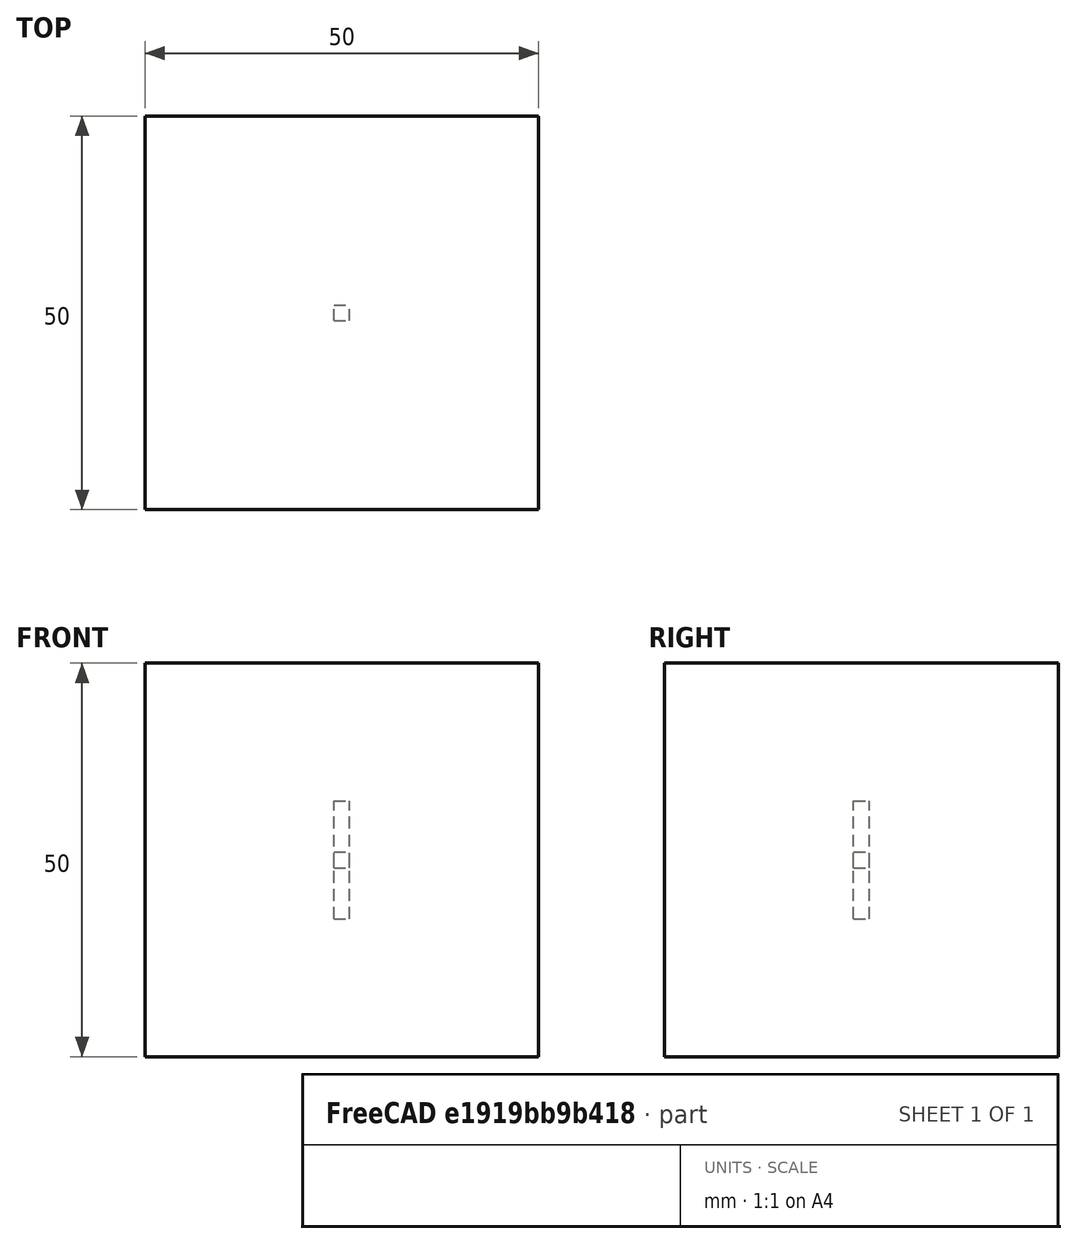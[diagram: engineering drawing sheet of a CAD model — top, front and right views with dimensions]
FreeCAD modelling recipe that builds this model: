
FCSTD DOCUMENT  (FreeCAD 0.20R29177 (Git))
Label: simple_array_expanded
License: All rights reserved
LicenseURL: http://en.wikipedia.org/wiki/All_rights_reserved
objects: App::DocumentObjectGroupPython×1269, App::Part×10, App::Link×6, App::FeaturePython×4, Part::FeaturePython×3
note: 3 computed .brp shape members not serialized (recipe doc carries the construction recipe); baked Part::Feature solids carry a one-line shape summary decoded from their .brp

FEATURE [App::DocumentObjectGroupPython] Constants  # scripted group (container) (typed FeaturePython)
FEATURE [App::DocumentObjectGroupPython] Variables  # scripted group (container) (typed FeaturePython)
FEATURE [App::DocumentObjectGroupPython] Quantities  # scripted group (container) (typed FeaturePython)
FEATURE [App::DocumentObjectGroupPython] Isotopes  # scripted group (container) (typed FeaturePython)
FEATURE [App::DocumentObjectGroupPython] Elements  # scripted group (container) (typed FeaturePython)
FEATURE [App::DocumentObjectGroupPython] G4_CESIUM_IODIDE  label="G4_CESIUM_IODIDE : 1.000"  # scripted group (container) (typed FeaturePython)
  n = 1
FEATURE [App::DocumentObjectGroupPython] LYSO  # scripted group (container) (typed FeaturePython)
  ABSLENGTH = ABSLENGTHLAR
  Dunit = g/cm3
  Dvalue = 7.1
  FASTCOMPONENT = SCINTLAR
  Group = -> [G4_CESIUM_IODIDE]
  RAYLEIGH = RAYLEIGHLAR
  REEMISSIONPROB = SCINTLAR
  RESOLUTIONSCALE = RS
  RINDEX = RINDEXLAR
  SCINTILLATIONCOMPONENT1 = SCINTLAR
  SCINTILLATIONCOMPONENT2 = SCINTLAR
  SCINTILLATIONTIMECONSTANT1 = FTC
  SCINTILLATIONTIMECONSTANT2 = STC
  SCINTILLATIONYIELD = SY
  SCINTILLATIONYIELD1 = RY1
  SCINTILLATIONYIELD2 = RY2
  SLOWCOMPONENT = SCINTLAR
  YIELDRATIO = YR
  conduct = 2
  density = 1
  expand = 3
  name = LYSO
  specific = 4
FEATURE [App::DocumentObjectGroupPython] G4_AIR  label="G4_AIR : 1.000"  # scripted group (container) (typed FeaturePython)
  n = 1
FEATURE [App::DocumentObjectGroupPython] Air  # scripted group (container) (typed FeaturePython)
  Dunit = mg/cm3
  Dvalue = 1.29
  Group = -> [G4_AIR]
  RINDEX = AirRINDEX
  conduct = 2
  density = 1
  expand = 3
  name = Air
  specific = 4
FEATURE [App::DocumentObjectGroupPython] G4_SILICON_DIOXIDE  label="G4_SILICON_DIOXIDE : 1.000"  # scripted group (container) (typed FeaturePython)
  n = 1
FEATURE [App::DocumentObjectGroupPython] Glass  # scripted group (container) (typed FeaturePython)
  Dunit = g/cm3
  Dvalue = 2.32
  Group = -> [G4_SILICON_DIOXIDE]
  RINDEX = RINDEXLAR
  conduct = 2
  density = 1
  expand = 3
  name = Glass
  specific = 4
FEATURE [App::DocumentObjectGroupPython] SY  # scripted group (container) (typed FeaturePython)
  coldim = 1
  values = 100000
FEATURE [App::DocumentObjectGroupPython] RS  # scripted group (container) (typed FeaturePython)
  coldim = 1
  values = 1
FEATURE [App::DocumentObjectGroupPython] FTC  # scripted group (container) (typed FeaturePython)
  coldim = 1
  values = 21.5*ns
FEATURE [App::DocumentObjectGroupPython] STC  # scripted group (container) (typed FeaturePython)
  coldim = 1
  values = 43.8*ns
FEATURE [App::DocumentObjectGroupPython] RY1  # scripted group (container) (typed FeaturePython)
  coldim = 1
  values = 95
FEATURE [App::DocumentObjectGroupPython] RY2  # scripted group (container) (typed FeaturePython)
  coldim = 1
  values = 5
FEATURE [App::DocumentObjectGroupPython] YR  # scripted group (container) (typed FeaturePython)
  coldim = 1
  values = 0.8
FEATURE [App::DocumentObjectGroupPython] SCINTLAR  # scripted group (container) (typed FeaturePython)
  coldim = 2
  values = <blob: 2358 chars omitted>
FEATURE [App::DocumentObjectGroupPython] RINDEXLAR  # scripted group (container) (typed FeaturePython)
  coldim = 2
  values = <blob: 9384 chars omitted>
FEATURE [App::DocumentObjectGroupPython] ABSLENGTHLAR  # scripted group (container) (typed FeaturePython)
  coldim = 2
  values = 7.74901*eV 10.0*m 7.77525*eV 10.0*m 7.80167*eV 10.0*m 7.82827*eV 10.0*m 7.85506*eV 10.0*m 7.88202*eV 10.0*m 7.90917*eV 10.0*m 7.93651*eV 10.0*m 7.96404*eV 10.0*m 7.99176*eV 10.0*m 8.01968*eV 10.0*m 8.04779*eV 10.0*m 8.07609*eV 10.0*m 8.1046*eV 10.0*m 8.13331*eV 10.0*m 8.16222*eV 10.0*m 8.19134*eV 10.0*m 8.22067*eV 10.0*m 8.25021*eV 10.0*m 8.27996*eV 10.0*m 8.30993*eV 10.0*m 8.34012*eV 10.0*m 8.37052*eV 10.0*m 8.40115*eV 10.0*m 8.432*eV 10.0*m 8.46308*eV 10.0*m 8.4944*eV 10.0*m 8.52594*eV 10.0*m 8.55772*eV 10.0*m 8.58973*eV 10.0*m 8.62199*eV 10.0*m 8.65449*eV 10.0*m 8.68723*eV 10.0*m 8.72023*eV 10.0*m 8.75347*eV 10.0*m 8.78697*eV 10.0*m 8.82073*eV 10.0*m 8.85475*eV 10.0*m 8.88903*eV 10.0*m 8.92358*eV 10.0*m 8.9584*eV 10.0*m 8.99349*eV 10.0*m 9.02885*eV 10.0*m 9.0645*eV 10.0*m 9.10043*eV 10.0*m 9.13664*eV 10.0*m 9.17314*eV 10.0*m 9.20994*eV 10.0*m 9.24703*eV 10.0*m 9.28442*eV 10.0*m 9.32212*eV 10.0*m 9.36012*eV 10.0*m 9.39844*eV 10.0*m 9.43707*eV 10.0*m 9.47602*eV 10.0*m 9.51529*eV 10.0*m 9.55489*eV 10.0*m 9.59481*eV 10.0*m 9.63508*eV 10.0*m 9.67568*eV 10.0*m 9.71663*eV 10.0*m 9.75792*eV 10.0*m 9.79957*eV 10.0*m 9.84158*eV 10.0*m 9.88394*eV 10.0*m 9.92668*eV 10.0*m 9.96978*eV 10.0*m 10.0133*eV 10.0*m 10.0571*eV 10.0*m 10.1014*eV 10.0*m 10.146*eV 10.0*m 10.191*eV 10.0*m 10.2365*eV 10.0*m 10.2823*eV 10.0*m 10.3286*eV 10.0*m 10.3752*eV 10.0*m 10.4223*eV 10.0*m 10.4699*eV 10.0*m 10.5178*eV 10.0*m 10.5662*eV 10.0*m 10.6151*eV 10.0*m 10.6644*eV 10.0*m 10.7142*eV 10.0*m 10.7644*eV 10.0*m 10.8151*eV 10.0*m 10.8663*eV 10.0*m 10.9179*eV 10.0*m 10.9701*eV 10.0*m 11.0228*eV 10.0*m 11.076*eV 10.0*m 11.1296*eV 10.0*m 11.1839*eV 10.0*m 11.2386*eV 10.0*m 11.2939*eV 10.0*m 11.3497*eV 10.0*m 11.4061*eV 10.0*m 11.463*eV 10.0*m 11.5206*eV 10.0*m 11.5787*eV 10.0*m 11.6373*eV 10.0*m
FEATURE [App::DocumentObjectGroupPython] RAYLEIGHLAR  # scripted group (container) (typed FeaturePython)
  coldim = 2
  values = 7.74901*eV 90.0*cm 7.77525*eV 90.0*cm 7.80167*eV 90.0*cm 7.82827*eV 90.0*cm 7.85506*eV 90.0*cm 7.88202*eV 90.0*cm 7.90917*eV 90.0*cm 7.93651*eV 90.0*cm 7.96404*eV 90.0*cm 7.99176*eV 90.0*cm 8.01968*eV 90.0*cm 8.04779*eV 90.0*cm 8.07609*eV 90.0*cm 8.1046*eV 90.0*cm 8.13331*eV 90.0*cm 8.16222*eV 90.0*cm 8.19134*eV 90.0*cm 8.22067*eV 90.0*cm 8.25021*eV 90.0*cm 8.27996*eV 90.0*cm 8.30993*eV 90.0*cm 8.34012*eV 90.0*cm 8.37052*eV 90.0*cm 8.40115*eV 90.0*cm 8.432*eV 90.0*cm 8.46308*eV 90.0*cm 8.4944*eV 90.0*cm 8.52594*eV 90.0*cm 8.55772*eV 90.0*cm 8.58973*eV 90.0*cm 8.62199*eV 90.0*cm 8.65449*eV 90.0*cm 8.68723*eV 90.0*cm 8.72023*eV 90.0*cm 8.75347*eV 90.0*cm 8.78697*eV 90.0*cm 8.82073*eV 90.0*cm 8.85475*eV 90.0*cm 8.88903*eV 90.0*cm 8.92358*eV 90.0*cm 8.9584*eV 90.0*cm 8.99349*eV 90.0*cm 9.02885*eV 90.0*cm 9.0645*eV 90.0*cm 9.10043*eV 90.0*cm 9.13664*eV 90.0*cm 9.17314*eV 90.0*cm 9.20994*eV 90.0*cm 9.24703*eV 90.0*cm 9.28442*eV 90.0*cm 9.32212*eV 90.0*cm 9.36012*eV 90.0*cm 9.39844*eV 90.0*cm 9.43707*eV 90.0*cm 9.47602*eV 90.0*cm 9.51529*eV 90.0*cm 9.55489*eV 90.0*cm 9.59481*eV 90.0*cm 9.63508*eV 90.0*cm 9.67568*eV 90.0*cm 9.71663*eV 90.0*cm 9.75792*eV 90.0*cm 9.79957*eV 90.0*cm 9.84158*eV 90.0*cm 9.88394*eV 90.0*cm 9.92668*eV 90.0*cm 9.96978*eV 90.0*cm 10.0133*eV 90.0*cm 10.0571*eV 90.0*cm 10.1014*eV 90.0*cm 10.146*eV 90.0*cm 10.191*eV 90.0*cm 10.2365*eV 90.0*cm 10.2823*eV 90.0*cm 10.3286*eV 90.0*cm 10.3752*eV 90.0*cm 10.4223*eV 90.0*cm 10.4699*eV 90.0*cm 10.5178*eV 90.0*cm 10.5662*eV 90.0*cm 10.6151*eV 90.0*cm 10.6644*eV 90.0*cm 10.7142*eV 90.0*cm 10.7644*eV 90.0*cm 10.8151*eV 90.0*cm 10.8663*eV 90.0*cm 10.9179*eV 90.0*cm 10.9701*eV 90.0*cm 11.0228*eV 90.0*cm 11.076*eV 90.0*cm 11.1296*eV 90.0*cm 11.1839*eV 90.0*cm 11.2386*eV 90.0*cm 11.2939*eV 90.0*cm 11.3497*eV 90.0*cm 11.4061*eV 90.0*cm 11.463*eV 90.0*cm 11.5206*eV 90.0*cm 11.5787*eV 90.0*cm 11.6373*eV 90.0*cm
FEATURE [App::DocumentObjectGroupPython] REFLECTIVITY  # scripted group (container) (typed FeaturePython)
  coldim = 2
  values = 2.034*eV 0.98 2.068*eV 0.98 2.103*eV 0.98 2.139*eV 0.98 2.177*eV 0.98 2.216*eV 0.98 2.256*eV 0.98 2.298*eV 0.98 2.341*eV 0.98 2.386*eV 0.98 2.433*eV 0.98 2.481*eV 0.98 2.532*eV 0.98 2.585*eV 0.98 2.64*eV 0.98 2.697*eV 0.98 2.757*eV 0.98 2.82*eV 0.98 2.885*eV 0.98 2.954*eV 0.98 3.026*eV 0.98 3.102*eV 0.98 3.181*eV 0.98 3.265*eV 0.98 3.353*eV 0.98 3.446*eV 0.98 3.545*eV 0.98 3.649*eV 0.98 3.76*eV 0.98 3.877*eV 0.98 4.002*eV 0.98 4.136*eV 0.98 5.0*eV 0.98 6.0*eV 0.98 7.0*eV 0.98 8.0*eV 0.98 9.0*eV 0.98 9.0*eV 0.98 10.0*eV 0.98 11.0*eV 0.98 11.6*eV 0.98
FEATURE [App::DocumentObjectGroupPython] EFFICIENCY  # scripted group (container) (typed FeaturePython)
  coldim = 2
  values = 2.034*eV 1 2.068*eV 1 2.103*eV 1 2.139*eV 1 2.177*eV 1 2.216*eV 1 2.256*eV 1 2.298*eV 1 2.341*eV 1 2.386*eV 1 2.433*eV 1 2.481*eV 1 2.532*eV 1 2.585*eV 1 2.64*eV 1 2.697*eV 1 2.757*eV 1 2.82*eV 1 2.885*eV 1 2.954*eV 1 3.026*eV 1 3.102*eV 1 3.181*eV  1 3.265*eV 1 3.353*eV 1 3.446*eV 1 3.545*eV 1 3.649*eV 1 3.76*eV 1 3.877*eV 1 4.002*eV 1 4.136*eV 1 5.0*eV 1 6.0*eV 1 7.0*eV 1 8.0*eV 1 9.0*eV 1 9.0*eV 1 10.0*eV 1 11.0*eV 1 11.6*eV 1
FEATURE [App::DocumentObjectGroupPython] AirRINDEX  # scripted group (container) (typed FeaturePython)
  coldim = 2
  values = 2.034*eV 1 2.068*eV 1 2.103*eV 1 2.139*eV 1 2.177*eV 1 2.216*eV 1 2.256*eV 1 2.298*eV 1 2.341*eV 1 2.386*eV 1 2.433*eV 1 2.481*eV 1 2.532*eV 1 2.585*eV 1 2.64*eV 1 2.697*eV 1 2.757*eV 1 2.82*eV 1 2.885*eV 1 2.954*eV 1 3.026*eV 1 3.102*eV 1 3.181*eV 1 3.265*eV 1 3.353*eV 1 3.446*eV 1 3.545*eV 1 3.649*eV 1 3.76*eV 1 3.877*eV 1 4.002*eV 1 4.136*eV 1 5.0*eV 1 6.0*eV 1 7.0*eV 1 8.0*eV 1 9.0*eV 1 10.0*eV 1 11.0*eV 1 11.6*eV 1
FEATURE [App::DocumentObjectGroupPython] Matrix  # scripted group (container) (typed FeaturePython)
  Group = -> [SY,RS,FTC,STC,RY1,RY2,YR,SCINTLAR,RINDEXLAR,ABSLENGTHLAR,RAYLEIGHLAR,REFLECTIVITY,EFFICIENCY,AirRINDEX]
FEATURE [App::DocumentObjectGroupPython] ScintWrap  # scripted group (container) (typed FeaturePython)
  EFFICIENCY = EFFICIENCY
  REFLECTIVITY = REFLECTIVITY
  finish = 39
  model = 0
  type = 2
  value = 1
FEATURE [App::DocumentObjectGroupPython] Surfaces  # scripted group (container) (typed FeaturePython)
  Group = -> [ScintWrap]
FEATURE [App::DocumentObjectGroupPython] Opticals  # scripted group (container) (typed FeaturePython)
  Group = -> [Matrix,Surfaces]
FEATURE [App::DocumentObjectGroupPython] G4Isotopes  # scripted group (container) (typed FeaturePython)
FEATURE [App::DocumentObjectGroupPython] H_element  # scripted group (container) (typed FeaturePython)
  Z = 1
  atom_value = 1.008
  formula = H
  name = H_element
FEATURE [App::DocumentObjectGroupPython] He_element  # scripted group (container) (typed FeaturePython)
  Z = 2
  atom_value = 4.0026
  formula = He
  name = He_element
FEATURE [App::DocumentObjectGroupPython] Li_element  # scripted group (container) (typed FeaturePython)
  Z = 3
  atom_value = 6.94
  formula = Li
  name = Li_element
FEATURE [App::DocumentObjectGroupPython] Be_element  # scripted group (container) (typed FeaturePython)
  Z = 4
  atom_value = 9.01218
  formula = Be
  name = Be_element
FEATURE [App::DocumentObjectGroupPython] B_element  # scripted group (container) (typed FeaturePython)
  Z = 5
  atom_value = 10.81
  formula = B
  name = B_element
FEATURE [App::DocumentObjectGroupPython] C_element  # scripted group (container) (typed FeaturePython)
  Z = 6
  atom_value = 12.011
  formula = C
  name = C_element
FEATURE [App::DocumentObjectGroupPython] N_element  # scripted group (container) (typed FeaturePython)
  Z = 7
  atom_value = 14.007
  formula = N
  name = N_element
FEATURE [App::DocumentObjectGroupPython] O_element  # scripted group (container) (typed FeaturePython)
  Z = 8
  atom_value = 15.999
  formula = O
  name = O_element
FEATURE [App::DocumentObjectGroupPython] F_element  # scripted group (container) (typed FeaturePython)
  Z = 9
  atom_value = 18.9984
  formula = F
  name = F_element
FEATURE [App::DocumentObjectGroupPython] Ne_element  # scripted group (container) (typed FeaturePython)
  Z = 10
  atom_value = 20.1797
  formula = Ne
  name = Ne_element
FEATURE [App::DocumentObjectGroupPython] Na_element  # scripted group (container) (typed FeaturePython)
  Z = 11
  atom_value = 22.9898
  formula = Na
  name = Na_element
FEATURE [App::DocumentObjectGroupPython] Mg_element  # scripted group (container) (typed FeaturePython)
  Z = 12
  atom_value = 24.305
  formula = Mg
  name = Mg_element
FEATURE [App::DocumentObjectGroupPython] Al_element  # scripted group (container) (typed FeaturePython)
  Z = 13
  atom_value = 26.9815
  formula = Al
  name = Al_element
FEATURE [App::DocumentObjectGroupPython] Si_element  # scripted group (container) (typed FeaturePython)
  Z = 14
  atom_value = 28.085
  formula = Si
  name = Si_element
FEATURE [App::DocumentObjectGroupPython] P_element  # scripted group (container) (typed FeaturePython)
  Z = 15
  atom_value = 30.9738
  formula = P
  name = P_element
FEATURE [App::DocumentObjectGroupPython] S_element  # scripted group (container) (typed FeaturePython)
  Z = 16
  atom_value = 32.06
  formula = S
  name = S_element
FEATURE [App::DocumentObjectGroupPython] Cl_element  # scripted group (container) (typed FeaturePython)
  Z = 17
  atom_value = 35.45
  formula = Cl
  name = Cl_element
FEATURE [App::DocumentObjectGroupPython] Ar_element  # scripted group (container) (typed FeaturePython)
  Z = 18
  atom_value = 39.95
  formula = Ar
  name = Ar_element
FEATURE [App::DocumentObjectGroupPython] K_element  # scripted group (container) (typed FeaturePython)
  Z = 19
  atom_value = 39.0983
  formula = K
  name = K_element
FEATURE [App::DocumentObjectGroupPython] Ca_element  # scripted group (container) (typed FeaturePython)
  Z = 20
  atom_value = 40.078
  formula = Ca
  name = Ca_element
FEATURE [App::DocumentObjectGroupPython] Sc_element  # scripted group (container) (typed FeaturePython)
  Z = 21
  atom_value = 44.9559
  formula = Sc
  name = Sc_element
FEATURE [App::DocumentObjectGroupPython] Ti_element  # scripted group (container) (typed FeaturePython)
  Z = 22
  atom_value = 47.867
  formula = Ti
  name = Ti_element
FEATURE [App::DocumentObjectGroupPython] V_element  # scripted group (container) (typed FeaturePython)
  Z = 23
  atom_value = 50.9415
  formula = V
  name = V_element
FEATURE [App::DocumentObjectGroupPython] Cr_element  # scripted group (container) (typed FeaturePython)
  Z = 24
  atom_value = 51.9961
  formula = Cr
  name = Cr_element
FEATURE [App::DocumentObjectGroupPython] Mn_element  # scripted group (container) (typed FeaturePython)
  Z = 25
  atom_value = 54.938
  formula = Mn
  name = Mn_element
FEATURE [App::DocumentObjectGroupPython] Fe_element  # scripted group (container) (typed FeaturePython)
  Z = 26
  atom_value = 55.845
  formula = Fe
  name = Fe_element
FEATURE [App::DocumentObjectGroupPython] Co_element  # scripted group (container) (typed FeaturePython)
  Z = 27
  atom_value = 58.9332
  formula = Co
  name = Co_element
FEATURE [App::DocumentObjectGroupPython] Ni_element  # scripted group (container) (typed FeaturePython)
  Z = 28
  atom_value = 58.6934
  formula = Ni
  name = Ni_element
FEATURE [App::DocumentObjectGroupPython] Cu_element  # scripted group (container) (typed FeaturePython)
  Z = 29
  atom_value = 63.546
  formula = Cu
  name = Cu_element
FEATURE [App::DocumentObjectGroupPython] Zn_element  # scripted group (container) (typed FeaturePython)
  Z = 30
  atom_value = 65.38
  formula = Zn
  name = Zn_element
FEATURE [App::DocumentObjectGroupPython] Ga_element  # scripted group (container) (typed FeaturePython)
  Z = 31
  atom_value = 69.723
  formula = Ga
  name = Ga_element
FEATURE [App::DocumentObjectGroupPython] Ge_element  # scripted group (container) (typed FeaturePython)
  Z = 32
  atom_value = 72.63
  formula = Ge
  name = Ge_element
FEATURE [App::DocumentObjectGroupPython] As_element  # scripted group (container) (typed FeaturePython)
  Z = 33
  atom_value = 74.9216
  formula = As
  name = As_element
FEATURE [App::DocumentObjectGroupPython] Se_element  # scripted group (container) (typed FeaturePython)
  Z = 34
  atom_value = 78.971
  formula = Se
  name = Se_element
FEATURE [App::DocumentObjectGroupPython] Br_element  # scripted group (container) (typed FeaturePython)
  Z = 35
  atom_value = 79.904
  formula = Br
  name = Br_element
FEATURE [App::DocumentObjectGroupPython] Kr_element  # scripted group (container) (typed FeaturePython)
  Z = 36
  atom_value = 83.798
  formula = Kr
  name = Kr_element
FEATURE [App::DocumentObjectGroupPython] Rb_element  # scripted group (container) (typed FeaturePython)
  Z = 37
  atom_value = 85.4678
  formula = Rb
  name = Rb_element
FEATURE [App::DocumentObjectGroupPython] Sr_element  # scripted group (container) (typed FeaturePython)
  Z = 38
  atom_value = 87.62
  formula = Sr
  name = Sr_element
FEATURE [App::DocumentObjectGroupPython] Y_element  # scripted group (container) (typed FeaturePython)
  Z = 39
  atom_value = 88.9058
  formula = Y
  name = Y_element
FEATURE [App::DocumentObjectGroupPython] Zr_element  # scripted group (container) (typed FeaturePython)
  Z = 40
  atom_value = 91.224
  formula = Zr
  name = Zr_element
FEATURE [App::DocumentObjectGroupPython] Nb_element  # scripted group (container) (typed FeaturePython)
  Z = 41
  atom_value = 92.9064
  formula = Nb
  name = Nb_element
FEATURE [App::DocumentObjectGroupPython] Mo_element  # scripted group (container) (typed FeaturePython)
  Z = 42
  atom_value = 95.95
  formula = Mo
  name = Mo_element
FEATURE [App::DocumentObjectGroupPython] Tc_element  # scripted group (container) (typed FeaturePython)
  Z = 43
  atom_value = 97
  formula = Tc
  name = Tc_element
FEATURE [App::DocumentObjectGroupPython] Ru_element  # scripted group (container) (typed FeaturePython)
  Z = 44
  atom_value = 101.07
  formula = Ru
  name = Ru_element
FEATURE [App::DocumentObjectGroupPython] Rh_element  # scripted group (container) (typed FeaturePython)
  Z = 45
  atom_value = 102.905
  formula = Rh
  name = Rh_element
FEATURE [App::DocumentObjectGroupPython] Pd_element  # scripted group (container) (typed FeaturePython)
  Z = 46
  atom_value = 106.42
  formula = Pd
  name = Pd_element
FEATURE [App::DocumentObjectGroupPython] Ag_element  # scripted group (container) (typed FeaturePython)
  Z = 47
  atom_value = 107.868
  formula = Ag
  name = Ag_element
FEATURE [App::DocumentObjectGroupPython] Cd_element  # scripted group (container) (typed FeaturePython)
  Z = 48
  atom_value = 112.414
  formula = Cd
  name = Cd_element
FEATURE [App::DocumentObjectGroupPython] In_element  # scripted group (container) (typed FeaturePython)
  Z = 49
  atom_value = 114.818
  formula = In
  name = In_element
FEATURE [App::DocumentObjectGroupPython] Sn_element  # scripted group (container) (typed FeaturePython)
  Z = 50
  atom_value = 118.71
  formula = Sn
  name = Sn_element
FEATURE [App::DocumentObjectGroupPython] Sb_element  # scripted group (container) (typed FeaturePython)
  Z = 51
  atom_value = 121.76
  formula = Sb
  name = Sb_element
FEATURE [App::DocumentObjectGroupPython] Te_element  # scripted group (container) (typed FeaturePython)
  Z = 52
  atom_value = 127.6
  formula = Te
  name = Te_element
FEATURE [App::DocumentObjectGroupPython] I_element  # scripted group (container) (typed FeaturePython)
  Z = 53
  atom_value = 126.904
  formula = I
  name = I_element
FEATURE [App::DocumentObjectGroupPython] Xe_element  # scripted group (container) (typed FeaturePython)
  Z = 54
  atom_value = 131.293
  formula = Xe
  name = Xe_element
FEATURE [App::DocumentObjectGroupPython] Cs_element  # scripted group (container) (typed FeaturePython)
  Z = 55
  atom_value = 132.905
  formula = Cs
  name = Cs_element
FEATURE [App::DocumentObjectGroupPython] Ba_element  # scripted group (container) (typed FeaturePython)
  Z = 56
  atom_value = 137.327
  formula = Ba
  name = Ba_element
FEATURE [App::DocumentObjectGroupPython] La_element  # scripted group (container) (typed FeaturePython)
  Z = 57
  atom_value = 138.905
  formula = La
  name = La_element
FEATURE [App::DocumentObjectGroupPython] Ce_element  # scripted group (container) (typed FeaturePython)
  Z = 58
  atom_value = 140.116
  formula = Ce
  name = Ce_element
FEATURE [App::DocumentObjectGroupPython] Pr_element  # scripted group (container) (typed FeaturePython)
  Z = 59
  atom_value = 140.908
  formula = Pr
  name = Pr_element
FEATURE [App::DocumentObjectGroupPython] Nd_element  # scripted group (container) (typed FeaturePython)
  Z = 60
  atom_value = 144.242
  formula = Nd
  name = Nd_element
FEATURE [App::DocumentObjectGroupPython] Pm_element  # scripted group (container) (typed FeaturePython)
  Z = 61
  atom_value = 145
  formula = Pm
  name = Pm_element
FEATURE [App::DocumentObjectGroupPython] Sm_element  # scripted group (container) (typed FeaturePython)
  Z = 62
  atom_value = 150.36
  formula = Sm
  name = Sm_element
FEATURE [App::DocumentObjectGroupPython] Eu_element  # scripted group (container) (typed FeaturePython)
  Z = 63
  atom_value = 151.964
  formula = Eu
  name = Eu_element
FEATURE [App::DocumentObjectGroupPython] Gd_element  # scripted group (container) (typed FeaturePython)
  Z = 64
  atom_value = 157.25
  formula = Gd
  name = Gd_element
FEATURE [App::DocumentObjectGroupPython] Tb_element  # scripted group (container) (typed FeaturePython)
  Z = 65
  atom_value = 158.925
  formula = Tb
  name = Tb_element
FEATURE [App::DocumentObjectGroupPython] Dy_element  # scripted group (container) (typed FeaturePython)
  Z = 66
  atom_value = 162.5
  formula = Dy
  name = Dy_element
FEATURE [App::DocumentObjectGroupPython] Ho_element  # scripted group (container) (typed FeaturePython)
  Z = 67
  atom_value = 164.93
  formula = Ho
  name = Ho_element
FEATURE [App::DocumentObjectGroupPython] Er_element  # scripted group (container) (typed FeaturePython)
  Z = 68
  atom_value = 167.259
  formula = Er
  name = Er_element
FEATURE [App::DocumentObjectGroupPython] Tm_element  # scripted group (container) (typed FeaturePython)
  Z = 69
  atom_value = 168.934
  formula = Tm
  name = Tm_element
FEATURE [App::DocumentObjectGroupPython] Yb_element  # scripted group (container) (typed FeaturePython)
  Z = 70
  atom_value = 173.045
  formula = Yb
  name = Yb_element
FEATURE [App::DocumentObjectGroupPython] Lu_element  # scripted group (container) (typed FeaturePython)
  Z = 71
  atom_value = 174.967
  formula = Lu
  name = Lu_element
FEATURE [App::DocumentObjectGroupPython] Hf_element  # scripted group (container) (typed FeaturePython)
  Z = 72
  atom_value = 178.49
  formula = Hf
  name = Hf_element
FEATURE [App::DocumentObjectGroupPython] Ta_element  # scripted group (container) (typed FeaturePython)
  Z = 73
  atom_value = 180.948
  formula = Ta
  name = Ta_element
FEATURE [App::DocumentObjectGroupPython] W_element  # scripted group (container) (typed FeaturePython)
  Z = 74
  atom_value = 183.84
  formula = W
  name = W_element
FEATURE [App::DocumentObjectGroupPython] Re_element  # scripted group (container) (typed FeaturePython)
  Z = 75
  atom_value = 186.207
  formula = Re
  name = Re_element
FEATURE [App::DocumentObjectGroupPython] Os_element  # scripted group (container) (typed FeaturePython)
  Z = 76
  atom_value = 190.23
  formula = Os
  name = Os_element
FEATURE [App::DocumentObjectGroupPython] Ir_element  # scripted group (container) (typed FeaturePython)
  Z = 77
  atom_value = 192.217
  formula = Ir
  name = Ir_element
FEATURE [App::DocumentObjectGroupPython] Pt_element  # scripted group (container) (typed FeaturePython)
  Z = 78
  atom_value = 195.084
  formula = Pt
  name = Pt_element
FEATURE [App::DocumentObjectGroupPython] Au_element  # scripted group (container) (typed FeaturePython)
  Z = 79
  atom_value = 196.967
  formula = Au
  name = Au_element
FEATURE [App::DocumentObjectGroupPython] Hg_element  # scripted group (container) (typed FeaturePython)
  Z = 80
  atom_value = 200.592
  formula = Hg
  name = Hg_element
FEATURE [App::DocumentObjectGroupPython] Tl_element  # scripted group (container) (typed FeaturePython)
  Z = 81
  atom_value = 204.38
  formula = Tl
  name = Tl_element
FEATURE [App::DocumentObjectGroupPython] Pb_element  # scripted group (container) (typed FeaturePython)
  Z = 82
  atom_value = 207.2
  formula = Pb
  name = Pb_element
FEATURE [App::DocumentObjectGroupPython] Bi_element  # scripted group (container) (typed FeaturePython)
  Z = 83
  atom_value = 208.98
  formula = Bi
  name = Bi_element
FEATURE [App::DocumentObjectGroupPython] Po_element  # scripted group (container) (typed FeaturePython)
  Z = 84
  atom_value = 209
  formula = Po
  name = Po_element
FEATURE [App::DocumentObjectGroupPython] At_element  # scripted group (container) (typed FeaturePython)
  Z = 85
  atom_value = 210
  formula = At
  name = At_element
FEATURE [App::DocumentObjectGroupPython] Rn_element  # scripted group (container) (typed FeaturePython)
  Z = 86
  atom_value = 222
  formula = Rn
  name = Rn_element
FEATURE [App::DocumentObjectGroupPython] Fr_element  # scripted group (container) (typed FeaturePython)
  Z = 87
  atom_value = 223
  formula = Fr
  name = Fr_element
FEATURE [App::DocumentObjectGroupPython] Ra_element  # scripted group (container) (typed FeaturePython)
  Z = 88
  atom_value = 226
  formula = Ra
  name = Ra_element
FEATURE [App::DocumentObjectGroupPython] Ac_element  # scripted group (container) (typed FeaturePython)
  Z = 89
  atom_value = 227
  formula = Ac
  name = Ac_element
FEATURE [App::DocumentObjectGroupPython] Th_element  # scripted group (container) (typed FeaturePython)
  Z = 90
  atom_value = 232.038
  formula = Th
  name = Th_element
FEATURE [App::DocumentObjectGroupPython] Pa_element  # scripted group (container) (typed FeaturePython)
  Z = 91
  atom_value = 231.036
  formula = Pa
  name = Pa_element
FEATURE [App::DocumentObjectGroupPython] U_element  # scripted group (container) (typed FeaturePython)
  Z = 92
  atom_value = 238.029
  formula = U
  name = U_element
FEATURE [App::DocumentObjectGroupPython] Np_element  # scripted group (container) (typed FeaturePython)
  Z = 93
  atom_value = 237
  formula = Np
  name = Np_element
FEATURE [App::DocumentObjectGroupPython] Pu_element  # scripted group (container) (typed FeaturePython)
  Z = 94
  atom_value = 244
  formula = Pu
  name = Pu_element
FEATURE [App::DocumentObjectGroupPython] Am_element  # scripted group (container) (typed FeaturePython)
  Z = 95
  atom_value = 243
  formula = Am
  name = Am_element
FEATURE [App::DocumentObjectGroupPython] Cm_element  # scripted group (container) (typed FeaturePython)
  Z = 96
  atom_value = 247
  formula = Cm
  name = Cm_element
FEATURE [App::DocumentObjectGroupPython] Bk_element  # scripted group (container) (typed FeaturePython)
  Z = 97
  atom_value = 247
  formula = Bk
  name = Bk_element
FEATURE [App::DocumentObjectGroupPython] Cf_element  # scripted group (container) (typed FeaturePython)
  Z = 98
  atom_value = 251
  formula = Cf
  name = Cf_element
FEATURE [App::DocumentObjectGroupPython] G4Elements  # scripted group (container) (typed FeaturePython)
  Group = -> [H_element,He_element,Li_element,Be_element,B_element,C_element,N_element,O_element,F_element,Ne_element,Na_element,Mg_element,Al_element,Si_element,P_element,S_element,Cl_element,Ar_element,K_element,Ca_element,Sc_element,Ti_element,V_element,Cr_element,Mn_element,Fe_element,Co_element,Ni_element,Cu_element,Zn_element,Ga_element,Ge_element,As_element,Se_element,Br_element,Kr_element,Rb_element,+61 more]
FEATURE [App::DocumentObjectGroupPython] H_element001  label="H_element : 0.101"  # scripted group (container) (typed FeaturePython)
  n = 0.101327
FEATURE [App::DocumentObjectGroupPython] C_element001  label="C_element : 0.775"  # scripted group (container) (typed FeaturePython)
  n = 0.7755
FEATURE [App::DocumentObjectGroupPython] N_element001  label="N_element : 0.035"  # scripted group (container) (typed FeaturePython)
  n = 0.035057
FEATURE [App::DocumentObjectGroupPython] O_element001  label="O_element : 0.052"  # scripted group (container) (typed FeaturePython)
  n = 0.0523159
FEATURE [App::DocumentObjectGroupPython] F_element001  label="F_element : 0.017"  # scripted group (container) (typed FeaturePython)
  n = 0.017422
FEATURE [App::DocumentObjectGroupPython] Ca_element001  label="Ca_element : 0.018"  # scripted group (container) (typed FeaturePython)
  n = 0.018378
FEATURE [App::DocumentObjectGroupPython] G4_A_150_TISSUE  label="G4_A-150_TISSUE"  # scripted group (container) (typed FeaturePython)
  Dunit = g/cm3
  Dvalue = 1.127
  Group = -> [H_element001,C_element001,N_element001,O_element001,F_element001,Ca_element001]
  conduct = 2
  density = 1
  expand = 3
  formula = G4_A-150_TISSUE
  name = G4_A-150_TISSUE
  specific = 4
FEATURE [App::DocumentObjectGroupPython] C_element002  label="C_element : 3"  # scripted group (container) (typed FeaturePython)
  n = 3
  ref = C_element
FEATURE [App::DocumentObjectGroupPython] H_element002  label="H_element : 6"  # scripted group (container) (typed FeaturePython)
  n = 6
  ref = H_element
FEATURE [App::DocumentObjectGroupPython] O_element002  label="O_element : 1"  # scripted group (container) (typed FeaturePython)
  n = 1
  ref = O_element
FEATURE [App::DocumentObjectGroupPython] G4_ACETONE  # scripted group (container) (typed FeaturePython)
  Dunit = g/cm3
  Dvalue = 0.7899
  Group = -> [C_element002,H_element002,O_element002]
  conduct = 2
  density = 1
  expand = 3
  formula = G4_ACETONE
  name = G4_ACETONE
  specific = 4
FEATURE [App::DocumentObjectGroupPython] C_element003  label="C_element : 2"  # scripted group (container) (typed FeaturePython)
  n = 2
  ref = C_element
FEATURE [App::DocumentObjectGroupPython] H_element003  label="H_element : 2"  # scripted group (container) (typed FeaturePython)
  n = 2
  ref = H_element
FEATURE [App::DocumentObjectGroupPython] G4_ACETYLENE  # scripted group (container) (typed FeaturePython)
  Dunit = g/cm3
  Dvalue = 0.0010967
  Group = -> [C_element003,H_element003]
  conduct = 2
  density = 1
  expand = 3
  formula = G4_ACETYLENE
  name = G4_ACETYLENE
  specific = 4
FEATURE [App::DocumentObjectGroupPython] C_element004  label="C_element : 5"  # scripted group (container) (typed FeaturePython)
  n = 5
  ref = C_element
FEATURE [App::DocumentObjectGroupPython] H_element004  label="H_element : 5"  # scripted group (container) (typed FeaturePython)
  n = 5
  ref = H_element
FEATURE [App::DocumentObjectGroupPython] N_element002  label="N_element : 5"  # scripted group (container) (typed FeaturePython)
  n = 5
  ref = N_element
FEATURE [App::DocumentObjectGroupPython] G4_ADENINE  # scripted group (container) (typed FeaturePython)
  Dunit = g/cm3
  Dvalue = 1.6
  Group = -> [C_element004,H_element004,N_element002]
  conduct = 2
  density = 1
  expand = 3
  formula = G4_ADENINE
  name = G4_ADENINE
  specific = 4
FEATURE [App::DocumentObjectGroupPython] H_element005  label="H_element : 0.114"  # scripted group (container) (typed FeaturePython)
  n = 0.114
FEATURE [App::DocumentObjectGroupPython] C_element005  label="C_element : 0.598"  # scripted group (container) (typed FeaturePython)
  n = 0.598
FEATURE [App::DocumentObjectGroupPython] N_element003  label="N_element : 0.007"  # scripted group (container) (typed FeaturePython)
  n = 0.007
FEATURE [App::DocumentObjectGroupPython] O_element003  label="O_element : 0.278"  # scripted group (container) (typed FeaturePython)
  n = 0.278
FEATURE [App::DocumentObjectGroupPython] Na_element001  label="Na_element : 0.001"  # scripted group (container) (typed FeaturePython)
  n = 0.001
FEATURE [App::DocumentObjectGroupPython] S_element001  label="S_element : 0.001"  # scripted group (container) (typed FeaturePython)
  n = 0.001
FEATURE [App::DocumentObjectGroupPython] Cl_element001  label="Cl_element : 0.001"  # scripted group (container) (typed FeaturePython)
  n = 0.001
FEATURE [App::DocumentObjectGroupPython] G4_ADIPOSE_TISSUE_ICRP  # scripted group (container) (typed FeaturePython)
  Dunit = g/cm3
  Dvalue = 0.95
  Group = -> [H_element005,C_element005,N_element003,O_element003,Na_element001,S_element001,Cl_element001]
  conduct = 2
  density = 1
  expand = 3
  formula = G4_ADIPOSE_TISSUE_ICRP
  name = G4_ADIPOSE_TISSUE_ICRP
  specific = 4
FEATURE [App::DocumentObjectGroupPython] C_element006  label="C_element : 0.000"  # scripted group (container) (typed FeaturePython)
  n = 0.000124
FEATURE [App::DocumentObjectGroupPython] N_element004  label="N_element : 0.755"  # scripted group (container) (typed FeaturePython)
  n = 0.755268
FEATURE [App::DocumentObjectGroupPython] O_element004  label="O_element : 0.232"  # scripted group (container) (typed FeaturePython)
  n = 0.231781
FEATURE [App::DocumentObjectGroupPython] Ar_element001  label="Ar_element : 0.013"  # scripted group (container) (typed FeaturePython)
  n = 0.012827
FEATURE [App::DocumentObjectGroupPython] G4_AIR001  label="G4_AIR"  # scripted group (container) (typed FeaturePython)
  Dunit = g/cm3
  Dvalue = 0.00120479
  Group = -> [C_element006,N_element004,O_element004,Ar_element001]
  conduct = 2
  density = 1
  expand = 3
  formula = G4_AIR
  name = G4_AIR
  specific = 4
FEATURE [App::DocumentObjectGroupPython] C_element007  label="C_element : 006"  # scripted group (container) (typed FeaturePython)
  n = 3
  ref = C_element
FEATURE [App::DocumentObjectGroupPython] H_element006  label="H_element : 7"  # scripted group (container) (typed FeaturePython)
  n = 7
  ref = H_element
FEATURE [App::DocumentObjectGroupPython] N_element005  label="N_element : 1"  # scripted group (container) (typed FeaturePython)
  n = 1
  ref = N_element
FEATURE [App::DocumentObjectGroupPython] O_element005  label="O_element : 2"  # scripted group (container) (typed FeaturePython)
  n = 2
  ref = O_element
FEATURE [App::DocumentObjectGroupPython] G4_ALANINE  # scripted group (container) (typed FeaturePython)
  Dunit = g/cm3
  Dvalue = 1.42
  Group = -> [C_element007,H_element006,N_element005,O_element005]
  conduct = 2
  density = 1
  expand = 3
  formula = G4_ALANINE
  name = G4_ALANINE
  specific = 4
FEATURE [App::DocumentObjectGroupPython] Al_element001  label="Al_element : 2"  # scripted group (container) (typed FeaturePython)
  n = 2
  ref = Al_element
FEATURE [App::DocumentObjectGroupPython] O_element006  label="O_element : 3"  # scripted group (container) (typed FeaturePython)
  n = 3
  ref = O_element
FEATURE [App::DocumentObjectGroupPython] G4_ALUMINUM_OXIDE  # scripted group (container) (typed FeaturePython)
  Dunit = g/cm3
  Dvalue = 3.97
  Group = -> [Al_element001,O_element006]
  conduct = 2
  density = 1
  expand = 3
  formula = G4_ALUMINUM_OXIDE
  name = G4_ALUMINUM_OXIDE
  specific = 4
FEATURE [App::DocumentObjectGroupPython] H_element007  label="H_element : 0.106"  # scripted group (container) (typed FeaturePython)
  n = 0.10593
FEATURE [App::DocumentObjectGroupPython] C_element008  label="C_element : 0.789"  # scripted group (container) (typed FeaturePython)
  n = 0.788974
FEATURE [App::DocumentObjectGroupPython] O_element007  label="O_element : 0.105"  # scripted group (container) (typed FeaturePython)
  n = 0.105096
FEATURE [App::DocumentObjectGroupPython] G4_AMBER  # scripted group (container) (typed FeaturePython)
  Dunit = g/cm3
  Dvalue = 1.1
  Group = -> [H_element007,C_element008,O_element007]
  conduct = 2
  density = 1
  expand = 3
  formula = G4_AMBER
  name = G4_AMBER
  specific = 4
FEATURE [App::DocumentObjectGroupPython] N_element006  label="N_element : 006"  # scripted group (container) (typed FeaturePython)
  n = 1
  ref = N_element
FEATURE [App::DocumentObjectGroupPython] H_element008  label="H_element : 3"  # scripted group (container) (typed FeaturePython)
  n = 3
  ref = H_element
FEATURE [App::DocumentObjectGroupPython] G4_AMMONIA  # scripted group (container) (typed FeaturePython)
  Dunit = g/cm3
  Dvalue = 0.000826019
  Group = -> [N_element006,H_element008]
  conduct = 2
  density = 1
  expand = 3
  formula = G4_AMMONIA
  name = G4_AMMONIA
  specific = 4
FEATURE [App::DocumentObjectGroupPython] C_element009  label="C_element : 6"  # scripted group (container) (typed FeaturePython)
  n = 6
  ref = C_element
FEATURE [App::DocumentObjectGroupPython] H_element009  label="H_element : 008"  # scripted group (container) (typed FeaturePython)
  n = 7
  ref = H_element
FEATURE [App::DocumentObjectGroupPython] N_element007  label="N_element : 007"  # scripted group (container) (typed FeaturePython)
  n = 1
  ref = N_element
FEATURE [App::DocumentObjectGroupPython] G4_ANILINE  # scripted group (container) (typed FeaturePython)
  Dunit = g/cm3
  Dvalue = 1.0235
  Group = -> [C_element009,H_element009,N_element007]
  conduct = 2
  density = 1
  expand = 3
  formula = G4_ANILINE
  name = G4_ANILINE
  specific = 4
FEATURE [App::DocumentObjectGroupPython] C_element010  label="C_element : 14"  # scripted group (container) (typed FeaturePython)
  n = 14
  ref = C_element
FEATURE [App::DocumentObjectGroupPython] H_element010  label="H_element : 10"  # scripted group (container) (typed FeaturePython)
  n = 10
  ref = H_element
FEATURE [App::DocumentObjectGroupPython] G4_ANTHRACENE  # scripted group (container) (typed FeaturePython)
  Dunit = g/cm3
  Dvalue = 1.283
  Group = -> [C_element010,H_element010]
  conduct = 2
  density = 1
  expand = 3
  formula = G4_ANTHRACENE
  name = G4_ANTHRACENE
  specific = 4
FEATURE [App::DocumentObjectGroupPython] H_element011  label="H_element : 0.065"  # scripted group (container) (typed FeaturePython)
  n = 0.0654709
FEATURE [App::DocumentObjectGroupPython] C_element011  label="C_element : 0.537"  # scripted group (container) (typed FeaturePython)
  n = 0.536944
FEATURE [App::DocumentObjectGroupPython] N_element008  label="N_element : 0.021"  # scripted group (container) (typed FeaturePython)
  n = 0.0215
FEATURE [App::DocumentObjectGroupPython] O_element008  label="O_element : 0.032"  # scripted group (container) (typed FeaturePython)
  n = 0.032085
FEATURE [App::DocumentObjectGroupPython] F_element002  label="F_element : 0.167"  # scripted group (container) (typed FeaturePython)
  n = 0.167411
FEATURE [App::DocumentObjectGroupPython] Ca_element002  label="Ca_element : 0.177"  # scripted group (container) (typed FeaturePython)
  n = 0.176589
FEATURE [App::DocumentObjectGroupPython] G4_B_100_BONE  label="G4_B-100_BONE"  # scripted group (container) (typed FeaturePython)
  Dunit = g/cm3
  Dvalue = 1.45
  Group = -> [H_element011,C_element011,N_element008,O_element008,F_element002,Ca_element002]
  conduct = 2
  density = 1
  expand = 3
  formula = G4_B-100_BONE
  name = G4_B-100_BONE
  specific = 4
FEATURE [App::DocumentObjectGroupPython] H_element012  label="H_element : 0.057"  # scripted group (container) (typed FeaturePython)
  n = 0.057441
FEATURE [App::DocumentObjectGroupPython] C_element012  label="C_element : 0.790"  # scripted group (container) (typed FeaturePython)
  n = 0.774591
FEATURE [App::DocumentObjectGroupPython] O_element009  label="O_element : 0.168"  # scripted group (container) (typed FeaturePython)
  n = 0.167968
FEATURE [App::DocumentObjectGroupPython] G4_BAKELITE  # scripted group (container) (typed FeaturePython)
  Dunit = g/cm3
  Dvalue = 1.25
  Group = -> [H_element012,C_element012,O_element009]
  conduct = 2
  density = 1
  expand = 3
  formula = G4_BAKELITE
  name = G4_BAKELITE
  specific = 4
FEATURE [App::DocumentObjectGroupPython] Ba_element001  label="Ba_element : 1"  # scripted group (container) (typed FeaturePython)
  n = 1
  ref = Ba_element
FEATURE [App::DocumentObjectGroupPython] F_element003  label="F_element : 2"  # scripted group (container) (typed FeaturePython)
  n = 2
  ref = F_element
FEATURE [App::DocumentObjectGroupPython] G4_BARIUM_FLUORIDE  # scripted group (container) (typed FeaturePython)
  Dunit = g/cm3
  Dvalue = 4.89
  Group = -> [Ba_element001,F_element003]
  conduct = 2
  density = 1
  expand = 3
  formula = G4_BARIUM_FLUORIDE
  name = G4_BARIUM_FLUORIDE
  specific = 4
FEATURE [App::DocumentObjectGroupPython] Ba_element002  label="Ba_element : 002"  # scripted group (container) (typed FeaturePython)
  n = 1
  ref = Ba_element
FEATURE [App::DocumentObjectGroupPython] S_element002  label="S_element : 1"  # scripted group (container) (typed FeaturePython)
  n = 1
  ref = S_element
FEATURE [App::DocumentObjectGroupPython] O_element010  label="O_element : 4"  # scripted group (container) (typed FeaturePython)
  n = 4
  ref = O_element
FEATURE [App::DocumentObjectGroupPython] G4_BARIUM_SULFATE  # scripted group (container) (typed FeaturePython)
  Dunit = g/cm3
  Dvalue = 4.5
  Group = -> [Ba_element002,S_element002,O_element010]
  conduct = 2
  density = 1
  expand = 3
  formula = G4_BARIUM_SULFATE
  name = G4_BARIUM_SULFATE
  specific = 4
FEATURE [App::DocumentObjectGroupPython] C_element013  label="C_element : 007"  # scripted group (container) (typed FeaturePython)
  n = 6
  ref = C_element
FEATURE [App::DocumentObjectGroupPython] H_element013  label="H_element : 009"  # scripted group (container) (typed FeaturePython)
  n = 6
  ref = H_element
FEATURE [App::DocumentObjectGroupPython] G4_BENZENE  # scripted group (container) (typed FeaturePython)
  Dunit = g/cm3
  Dvalue = 0.87865
  Group = -> [C_element013,H_element013]
  conduct = 2
  density = 1
  expand = 3
  formula = G4_BENZENE
  name = G4_BENZENE
  specific = 4
FEATURE [App::DocumentObjectGroupPython] Be_element001  label="Be_element : 1"  # scripted group (container) (typed FeaturePython)
  n = 1
  ref = Be_element
FEATURE [App::DocumentObjectGroupPython] O_element011  label="O_element : 005"  # scripted group (container) (typed FeaturePython)
  n = 1
  ref = O_element
FEATURE [App::DocumentObjectGroupPython] G4_BERYLLIUM_OXIDE  # scripted group (container) (typed FeaturePython)
  Dunit = g/cm3
  Dvalue = 3.01
  Group = -> [Be_element001,O_element011]
  conduct = 2
  density = 1
  expand = 3
  formula = G4_BERYLLIUM_OXIDE
  name = G4_BERYLLIUM_OXIDE
  specific = 4
FEATURE [App::DocumentObjectGroupPython] Bi_element001  label="Bi_element : 4"  # scripted group (container) (typed FeaturePython)
  n = 4
  ref = Bi_element
FEATURE [App::DocumentObjectGroupPython] Ge_element001  label="Ge_element : 3"  # scripted group (container) (typed FeaturePython)
  n = 3
  ref = Ge_element
FEATURE [App::DocumentObjectGroupPython] O_element012  label="O_element : 12"  # scripted group (container) (typed FeaturePython)
  n = 12
  ref = O_element
FEATURE [App::DocumentObjectGroupPython] G4_BGO  # scripted group (container) (typed FeaturePython)
  Dunit = g/cm3
  Dvalue = 7.13
  Group = -> [Bi_element001,Ge_element001,O_element012]
  conduct = 2
  density = 1
  expand = 3
  formula = G4_BGO
  name = G4_BGO
  specific = 4
FEATURE [App::DocumentObjectGroupPython] H_element014  label="H_element : 0.102"  # scripted group (container) (typed FeaturePython)
  n = 0.102
FEATURE [App::DocumentObjectGroupPython] C_element014  label="C_element : 0.110"  # scripted group (container) (typed FeaturePython)
  n = 0.11
FEATURE [App::DocumentObjectGroupPython] N_element009  label="N_element : 0.033"  # scripted group (container) (typed FeaturePython)
  n = 0.033
FEATURE [App::DocumentObjectGroupPython] O_element013  label="O_element : 0.745"  # scripted group (container) (typed FeaturePython)
  n = 0.745
FEATURE [App::DocumentObjectGroupPython] Na_element002  label="Na_element : 0.002"  # scripted group (container) (typed FeaturePython)
  n = 0.001
FEATURE [App::DocumentObjectGroupPython] P_element001  label="P_element : 0.001"  # scripted group (container) (typed FeaturePython)
  n = 0.001
FEATURE [App::DocumentObjectGroupPython] S_element003  label="S_element : 0.002"  # scripted group (container) (typed FeaturePython)
  n = 0.002
FEATURE [App::DocumentObjectGroupPython] Cl_element002  label="Cl_element : 0.003"  # scripted group (container) (typed FeaturePython)
  n = 0.003
FEATURE [App::DocumentObjectGroupPython] K_element001  label="K_element : 0.002"  # scripted group (container) (typed FeaturePython)
  n = 0.002
FEATURE [App::DocumentObjectGroupPython] Fe_element001  label="Fe_element : 0.001"  # scripted group (container) (typed FeaturePython)
  n = 0.001
FEATURE [App::DocumentObjectGroupPython] G4_BLOOD_ICRP  # scripted group (container) (typed FeaturePython)
  Dunit = g/cm3
  Dvalue = 1.06
  Group = -> [H_element014,C_element014,N_element009,O_element013,Na_element002,P_element001,S_element003,Cl_element002,K_element001,Fe_element001]
  conduct = 2
  density = 1
  expand = 3
  formula = G4_BLOOD_ICRP
  name = G4_BLOOD_ICRP
  specific = 4
FEATURE [App::DocumentObjectGroupPython] H_element015  label="H_element : 0.064"  # scripted group (container) (typed FeaturePython)
  n = 0.064
FEATURE [App::DocumentObjectGroupPython] C_element015  label="C_element : 0.278"  # scripted group (container) (typed FeaturePython)
  n = 0.278
FEATURE [App::DocumentObjectGroupPython] N_element010  label="N_element : 0.027"  # scripted group (container) (typed FeaturePython)
  n = 0.027
FEATURE [App::DocumentObjectGroupPython] O_element014  label="O_element : 0.410"  # scripted group (container) (typed FeaturePython)
  n = 0.41
FEATURE [App::DocumentObjectGroupPython] Mg_element001  label="Mg_element : 0.002"  # scripted group (container) (typed FeaturePython)
  n = 0.002
FEATURE [App::DocumentObjectGroupPython] P_element002  label="P_element : 0.070"  # scripted group (container) (typed FeaturePython)
  n = 0.07
FEATURE [App::DocumentObjectGroupPython] S_element004  label="S_element : 0.003"  # scripted group (container) (typed FeaturePython)
  n = 0.002
FEATURE [App::DocumentObjectGroupPython] Ca_element003  label="Ca_element : 0.147"  # scripted group (container) (typed FeaturePython)
  n = 0.147
FEATURE [App::DocumentObjectGroupPython] G4_BONE_COMPACT_ICRU  # scripted group (container) (typed FeaturePython)
  Dunit = g/cm3
  Dvalue = 1.85
  Group = -> [H_element015,C_element015,N_element010,O_element014,Mg_element001,P_element002,S_element004,Ca_element003]
  conduct = 2
  density = 1
  expand = 3
  formula = G4_BONE_COMPACT_ICRU
  name = G4_BONE_COMPACT_ICRU
  specific = 4
FEATURE [App::DocumentObjectGroupPython] H_element016  label="H_element : 0.034"  # scripted group (container) (typed FeaturePython)
  n = 0.034
FEATURE [App::DocumentObjectGroupPython] C_element016  label="C_element : 0.155"  # scripted group (container) (typed FeaturePython)
  n = 0.155
FEATURE [App::DocumentObjectGroupPython] N_element011  label="N_element : 0.042"  # scripted group (container) (typed FeaturePython)
  n = 0.042
FEATURE [App::DocumentObjectGroupPython] O_element015  label="O_element : 0.435"  # scripted group (container) (typed FeaturePython)
  n = 0.435
FEATURE [App::DocumentObjectGroupPython] Na_element003  label="Na_element : 0.003"  # scripted group (container) (typed FeaturePython)
  n = 0.001
FEATURE [App::DocumentObjectGroupPython] Mg_element002  label="Mg_element : 0.003"  # scripted group (container) (typed FeaturePython)
  n = 0.002
FEATURE [App::DocumentObjectGroupPython] P_element003  label="P_element : 0.103"  # scripted group (container) (typed FeaturePython)
  n = 0.103
FEATURE [App::DocumentObjectGroupPython] S_element005  label="S_element : 0.004"  # scripted group (container) (typed FeaturePython)
  n = 0.003
FEATURE [App::DocumentObjectGroupPython] Ca_element004  label="Ca_element : 0.225"  # scripted group (container) (typed FeaturePython)
  n = 0.225
FEATURE [App::DocumentObjectGroupPython] G4_BONE_CORTICAL_ICRP  # scripted group (container) (typed FeaturePython)
  Dunit = g/cm3
  Dvalue = 1.92
  Group = -> [H_element016,C_element016,N_element011,O_element015,Na_element003,Mg_element002,P_element003,S_element005,Ca_element004]
  conduct = 2
  density = 1
  expand = 3
  formula = G4_BONE_CORTICAL_ICRP
  name = G4_BONE_CORTICAL_ICRP
  specific = 4
FEATURE [App::DocumentObjectGroupPython] B_element001  label="B_element : 4"  # scripted group (container) (typed FeaturePython)
  n = 4
  ref = B_element
FEATURE [App::DocumentObjectGroupPython] C_element017  label="C_element : 1"  # scripted group (container) (typed FeaturePython)
  n = 1
  ref = C_element
FEATURE [App::DocumentObjectGroupPython] G4_BORON_CARBIDE  # scripted group (container) (typed FeaturePython)
  Dunit = g/cm3
  Dvalue = 2.52
  Group = -> [B_element001,C_element017]
  conduct = 2
  density = 1
  expand = 3
  formula = G4_BORON_CARBIDE
  name = G4_BORON_CARBIDE
  specific = 4
FEATURE [App::DocumentObjectGroupPython] B_element002  label="B_element : 2"  # scripted group (container) (typed FeaturePython)
  n = 2
  ref = B_element
FEATURE [App::DocumentObjectGroupPython] O_element016  label="O_element : 006"  # scripted group (container) (typed FeaturePython)
  n = 3
  ref = O_element
FEATURE [App::DocumentObjectGroupPython] G4_BORON_OXIDE  # scripted group (container) (typed FeaturePython)
  Dunit = g/cm3
  Dvalue = 1.812
  Group = -> [B_element002,O_element016]
  conduct = 2
  density = 1
  expand = 3
  formula = G4_BORON_OXIDE
  name = G4_BORON_OXIDE
  specific = 4
FEATURE [App::DocumentObjectGroupPython] H_element017  label="H_element : 0.107"  # scripted group (container) (typed FeaturePython)
  n = 0.107
FEATURE [App::DocumentObjectGroupPython] C_element018  label="C_element : 0.145"  # scripted group (container) (typed FeaturePython)
  n = 0.145
FEATURE [App::DocumentObjectGroupPython] N_element012  label="N_element : 0.022"  # scripted group (container) (typed FeaturePython)
  n = 0.022
FEATURE [App::DocumentObjectGroupPython] O_element017  label="O_element : 0.712"  # scripted group (container) (typed FeaturePython)
  n = 0.712
FEATURE [App::DocumentObjectGroupPython] Na_element004  label="Na_element : 0.004"  # scripted group (container) (typed FeaturePython)
  n = 0.002
FEATURE [App::DocumentObjectGroupPython] P_element004  label="P_element : 0.004"  # scripted group (container) (typed FeaturePython)
  n = 0.004
FEATURE [App::DocumentObjectGroupPython] S_element006  label="S_element : 0.005"  # scripted group (container) (typed FeaturePython)
  n = 0.002
FEATURE [App::DocumentObjectGroupPython] Cl_element003  label="Cl_element : 0.004"  # scripted group (container) (typed FeaturePython)
  n = 0.003
FEATURE [App::DocumentObjectGroupPython] K_element002  label="K_element : 0.003"  # scripted group (container) (typed FeaturePython)
  n = 0.003
FEATURE [App::DocumentObjectGroupPython] G4_BRAIN_ICRP  # scripted group (container) (typed FeaturePython)
  Dunit = g/cm3
  Dvalue = 1.04
  Group = -> [H_element017,C_element018,N_element012,O_element017,Na_element004,P_element004,S_element006,Cl_element003,K_element002]
  conduct = 2
  density = 1
  expand = 3
  formula = G4_BRAIN_ICRP
  name = G4_BRAIN_ICRP
  specific = 4
FEATURE [App::DocumentObjectGroupPython] C_element019  label="C_element : 4"  # scripted group (container) (typed FeaturePython)
  n = 4
  ref = C_element
FEATURE [App::DocumentObjectGroupPython] H_element018  label="H_element : 010"  # scripted group (container) (typed FeaturePython)
  n = 10
  ref = H_element
FEATURE [App::DocumentObjectGroupPython] G4_BUTANE  # scripted group (container) (typed FeaturePython)
  Dunit = g/cm3
  Dvalue = 0.00249343
  Group = -> [C_element019,H_element018]
  conduct = 2
  density = 1
  expand = 3
  formula = G4_BUTANE
  name = G4_BUTANE
  specific = 4
FEATURE [App::DocumentObjectGroupPython] C_element020  label="C_element : 008"  # scripted group (container) (typed FeaturePython)
  n = 4
  ref = C_element
FEATURE [App::DocumentObjectGroupPython] H_element019  label="H_element : 011"  # scripted group (container) (typed FeaturePython)
  n = 10
  ref = H_element
FEATURE [App::DocumentObjectGroupPython] O_element018  label="O_element : 007"  # scripted group (container) (typed FeaturePython)
  n = 1
  ref = O_element
FEATURE [App::DocumentObjectGroupPython] G4_N_BUTYL_ALCOHOL  label="G4_N-BUTYL_ALCOHOL"  # scripted group (container) (typed FeaturePython)
  Dunit = g/cm3
  Dvalue = 0.8098
  Group = -> [C_element020,H_element019,O_element018]
  conduct = 2
  density = 1
  expand = 3
  formula = G4_N-BUTYL_ALCOHOL
  name = G4_N-BUTYL_ALCOHOL
  specific = 4
FEATURE [App::DocumentObjectGroupPython] H_element020  label="H_element : 0.025"  # scripted group (container) (typed FeaturePython)
  n = 0.02468
FEATURE [App::DocumentObjectGroupPython] C_element021  label="C_element : 0.502"  # scripted group (container) (typed FeaturePython)
  n = 0.501611
FEATURE [App::DocumentObjectGroupPython] O_element019  label="O_element : 0.005"  # scripted group (container) (typed FeaturePython)
  n = 0.004527
FEATURE [App::DocumentObjectGroupPython] F_element004  label="F_element : 0.465"  # scripted group (container) (typed FeaturePython)
  n = 0.465209
FEATURE [App::DocumentObjectGroupPython] Si_element001  label="Si_element : 0.004"  # scripted group (container) (typed FeaturePython)
  n = 0.003973
FEATURE [App::DocumentObjectGroupPython] G4_C_552  label="G4_C-552"  # scripted group (container) (typed FeaturePython)
  Dunit = g/cm3
  Dvalue = 1.76
  Group = -> [H_element020,C_element021,O_element019,F_element004,Si_element001]
  conduct = 2
  density = 1
  expand = 3
  formula = G4_C-552
  name = G4_C-552
  specific = 4
FEATURE [App::DocumentObjectGroupPython] Cd_element001  label="Cd_element : 1"  # scripted group (container) (typed FeaturePython)
  n = 1
  ref = Cd_element
FEATURE [App::DocumentObjectGroupPython] Te_element001  label="Te_element : 1"  # scripted group (container) (typed FeaturePython)
  n = 1
  ref = Te_element
FEATURE [App::DocumentObjectGroupPython] G4_CADMIUM_TELLURIDE  # scripted group (container) (typed FeaturePython)
  Dunit = g/cm3
  Dvalue = 6.2
  Group = -> [Cd_element001,Te_element001]
  conduct = 2
  density = 1
  expand = 3
  formula = G4_CADMIUM_TELLURIDE
  name = G4_CADMIUM_TELLURIDE
  specific = 4
FEATURE [App::DocumentObjectGroupPython] Cd_element002  label="Cd_element : 002"  # scripted group (container) (typed FeaturePython)
  n = 1
  ref = Cd_element
FEATURE [App::DocumentObjectGroupPython] W_element001  label="W_element : 1"  # scripted group (container) (typed FeaturePython)
  n = 1
  ref = W_element
FEATURE [App::DocumentObjectGroupPython] O_element020  label="O_element : 008"  # scripted group (container) (typed FeaturePython)
  n = 4
  ref = O_element
FEATURE [App::DocumentObjectGroupPython] G4_CADMIUM_TUNGSTATE  # scripted group (container) (typed FeaturePython)
  Dunit = g/cm3
  Dvalue = 7.9
  Group = -> [Cd_element002,W_element001,O_element020]
  conduct = 2
  density = 1
  expand = 3
  formula = G4_CADMIUM_TUNGSTATE
  name = G4_CADMIUM_TUNGSTATE
  specific = 4
FEATURE [App::DocumentObjectGroupPython] Ca_element005  label="Ca_element : 1"  # scripted group (container) (typed FeaturePython)
  n = 1
  ref = Ca_element
FEATURE [App::DocumentObjectGroupPython] C_element022  label="C_element : 009"  # scripted group (container) (typed FeaturePython)
  n = 1
  ref = C_element
FEATURE [App::DocumentObjectGroupPython] O_element021  label="O_element : 009"  # scripted group (container) (typed FeaturePython)
  n = 3
  ref = O_element
FEATURE [App::DocumentObjectGroupPython] G4_CALCIUM_CARBONATE  # scripted group (container) (typed FeaturePython)
  Dunit = g/cm3
  Dvalue = 2.8
  Group = -> [Ca_element005,C_element022,O_element021]
  conduct = 2
  density = 1
  expand = 3
  formula = G4_CALCIUM_CARBONATE
  name = G4_CALCIUM_CARBONATE
  specific = 4
FEATURE [App::DocumentObjectGroupPython] Ca_element006  label="Ca_element : 002"  # scripted group (container) (typed FeaturePython)
  n = 1
  ref = Ca_element
FEATURE [App::DocumentObjectGroupPython] F_element005  label="F_element : 003"  # scripted group (container) (typed FeaturePython)
  n = 2
  ref = F_element
FEATURE [App::DocumentObjectGroupPython] G4_CALCIUM_FLUORIDE  # scripted group (container) (typed FeaturePython)
  Dunit = g/cm3
  Dvalue = 3.18
  Group = -> [Ca_element006,F_element005]
  conduct = 2
  density = 1
  expand = 3
  formula = G4_CALCIUM_FLUORIDE
  name = G4_CALCIUM_FLUORIDE
  specific = 4
FEATURE [App::DocumentObjectGroupPython] Ca_element007  label="Ca_element : 003"  # scripted group (container) (typed FeaturePython)
  n = 1
  ref = Ca_element
FEATURE [App::DocumentObjectGroupPython] O_element022  label="O_element : 010"  # scripted group (container) (typed FeaturePython)
  n = 1
  ref = O_element
FEATURE [App::DocumentObjectGroupPython] G4_CALCIUM_OXIDE  # scripted group (container) (typed FeaturePython)
  Dunit = g/cm3
  Dvalue = 3.3
  Group = -> [Ca_element007,O_element022]
  conduct = 2
  density = 1
  expand = 3
  formula = G4_CALCIUM_OXIDE
  name = G4_CALCIUM_OXIDE
  specific = 4
FEATURE [App::DocumentObjectGroupPython] Ca_element008  label="Ca_element : 004"  # scripted group (container) (typed FeaturePython)
  n = 1
  ref = Ca_element
FEATURE [App::DocumentObjectGroupPython] S_element007  label="S_element : 002"  # scripted group (container) (typed FeaturePython)
  n = 1
  ref = S_element
FEATURE [App::DocumentObjectGroupPython] O_element023  label="O_element : 011"  # scripted group (container) (typed FeaturePython)
  n = 4
  ref = O_element
FEATURE [App::DocumentObjectGroupPython] G4_CALCIUM_SULFATE  # scripted group (container) (typed FeaturePython)
  Dunit = g/cm3
  Dvalue = 2.96
  Group = -> [Ca_element008,S_element007,O_element023]
  conduct = 2
  density = 1
  expand = 3
  formula = G4_CALCIUM_SULFATE
  name = G4_CALCIUM_SULFATE
  specific = 4
FEATURE [App::DocumentObjectGroupPython] Ca_element009  label="Ca_element : 005"  # scripted group (container) (typed FeaturePython)
  n = 1
  ref = Ca_element
FEATURE [App::DocumentObjectGroupPython] W_element002  label="W_element : 002"  # scripted group (container) (typed FeaturePython)
  n = 1
  ref = W_element
FEATURE [App::DocumentObjectGroupPython] O_element024  label="O_element : 012"  # scripted group (container) (typed FeaturePython)
  n = 4
  ref = O_element
FEATURE [App::DocumentObjectGroupPython] G4_CALCIUM_TUNGSTATE  # scripted group (container) (typed FeaturePython)
  Dunit = g/cm3
  Dvalue = 6.062
  Group = -> [Ca_element009,W_element002,O_element024]
  conduct = 2
  density = 1
  expand = 3
  formula = G4_CALCIUM_TUNGSTATE
  name = G4_CALCIUM_TUNGSTATE
  specific = 4
FEATURE [App::DocumentObjectGroupPython] C_element023  label="C_element : 010"  # scripted group (container) (typed FeaturePython)
  n = 1
  ref = C_element
FEATURE [App::DocumentObjectGroupPython] O_element025  label="O_element : 013"  # scripted group (container) (typed FeaturePython)
  n = 2
  ref = O_element
FEATURE [App::DocumentObjectGroupPython] G4_CARBON_DIOXIDE  # scripted group (container) (typed FeaturePython)
  Dunit = g/cm3
  Dvalue = 0.00184212
  Group = -> [C_element023,O_element025]
  conduct = 2
  density = 1
  expand = 3
  formula = G4_CARBON_DIOXIDE
  name = G4_CARBON_DIOXIDE
  specific = 4
FEATURE [App::DocumentObjectGroupPython] C_element024  label="C_element : 011"  # scripted group (container) (typed FeaturePython)
  n = 1
  ref = C_element
FEATURE [App::DocumentObjectGroupPython] Cl_element004  label="Cl_element : 4"  # scripted group (container) (typed FeaturePython)
  n = 4
  ref = Cl_element
FEATURE [App::DocumentObjectGroupPython] G4_CARBON_TETRACHLORIDE  # scripted group (container) (typed FeaturePython)
  Dunit = g/cm3
  Dvalue = 1.594
  Group = -> [C_element024,Cl_element004]
  conduct = 2
  density = 1
  expand = 3
  formula = G4_CARBON_TETRACHLORIDE
  name = G4_CARBON_TETRACHLORIDE
  specific = 4
FEATURE [App::DocumentObjectGroupPython] C_element025  label="C_element : 012"  # scripted group (container) (typed FeaturePython)
  n = 6
  ref = C_element
FEATURE [App::DocumentObjectGroupPython] H_element021  label="H_element : 012"  # scripted group (container) (typed FeaturePython)
  n = 10
  ref = H_element
FEATURE [App::DocumentObjectGroupPython] O_element026  label="O_element : 5"  # scripted group (container) (typed FeaturePython)
  n = 5
  ref = O_element
FEATURE [App::DocumentObjectGroupPython] G4_CELLULOSE_CELLOPHANE  # scripted group (container) (typed FeaturePython)
  Dunit = g/cm3
  Dvalue = 1.42
  Group = -> [C_element025,H_element021,O_element026]
  conduct = 2
  density = 1
  expand = 3
  formula = G4_CELLULOSE_CELLOPHANE
  name = G4_CELLULOSE_CELLOPHANE
  specific = 4
FEATURE [App::DocumentObjectGroupPython] H_element022  label="H_element : 0.067"  # scripted group (container) (typed FeaturePython)
  n = 0.067125
FEATURE [App::DocumentObjectGroupPython] C_element026  label="C_element : 0.545"  # scripted group (container) (typed FeaturePython)
  n = 0.545403
FEATURE [App::DocumentObjectGroupPython] O_element027  label="O_element : 0.387"  # scripted group (container) (typed FeaturePython)
  n = 0.387472
FEATURE [App::DocumentObjectGroupPython] G4_CELLULOSE_BUTYRATE  # scripted group (container) (typed FeaturePython)
  Dunit = g/cm3
  Dvalue = 1.2
  Group = -> [H_element022,C_element026,O_element027]
  conduct = 2
  density = 1
  expand = 3
  formula = G4_CELLULOSE_BUTYRATE
  name = G4_CELLULOSE_BUTYRATE
  specific = 4
FEATURE [App::DocumentObjectGroupPython] H_element023  label="H_element : 0.029"  # scripted group (container) (typed FeaturePython)
  n = 0.029216
FEATURE [App::DocumentObjectGroupPython] C_element027  label="C_element : 0.271"  # scripted group (container) (typed FeaturePython)
  n = 0.271296
FEATURE [App::DocumentObjectGroupPython] N_element013  label="N_element : 0.121"  # scripted group (container) (typed FeaturePython)
  n = 0.121276
FEATURE [App::DocumentObjectGroupPython] O_element028  label="O_element : 0.578"  # scripted group (container) (typed FeaturePython)
  n = 0.578212
FEATURE [App::DocumentObjectGroupPython] G4_CELLULOSE_NITRATE  # scripted group (container) (typed FeaturePython)
  Dunit = g/cm3
  Dvalue = 1.49
  Group = -> [H_element023,C_element027,N_element013,O_element028]
  conduct = 2
  density = 1
  expand = 3
  formula = G4_CELLULOSE_NITRATE
  name = G4_CELLULOSE_NITRATE
  specific = 4
FEATURE [App::DocumentObjectGroupPython] H_element024  label="H_element : 0.108"  # scripted group (container) (typed FeaturePython)
  n = 0.107596
FEATURE [App::DocumentObjectGroupPython] N_element014  label="N_element : 0.001"  # scripted group (container) (typed FeaturePython)
  n = 0.0008
FEATURE [App::DocumentObjectGroupPython] O_element029  label="O_element : 0.875"  # scripted group (container) (typed FeaturePython)
  n = 0.874976
FEATURE [App::DocumentObjectGroupPython] S_element008  label="S_element : 0.015"  # scripted group (container) (typed FeaturePython)
  n = 0.014627
FEATURE [App::DocumentObjectGroupPython] Ce_element001  label="Ce_element : 0.002"  # scripted group (container) (typed FeaturePython)
  n = 0.002001
FEATURE [App::DocumentObjectGroupPython] G4_CERIC_SULFATE  # scripted group (container) (typed FeaturePython)
  Dunit = g/cm3
  Dvalue = 1.03
  Group = -> [H_element024,N_element014,O_element029,S_element008,Ce_element001]
  conduct = 2
  density = 1
  expand = 3
  formula = G4_CERIC_SULFATE
  name = G4_CERIC_SULFATE
  specific = 4
FEATURE [App::DocumentObjectGroupPython] Cs_element001  label="Cs_element : 1"  # scripted group (container) (typed FeaturePython)
  n = 1
  ref = Cs_element
FEATURE [App::DocumentObjectGroupPython] F_element006  label="F_element : 1"  # scripted group (container) (typed FeaturePython)
  n = 1
  ref = F_element
FEATURE [App::DocumentObjectGroupPython] G4_CESIUM_FLUORIDE  # scripted group (container) (typed FeaturePython)
  Dunit = g/cm3
  Dvalue = 4.115
  Group = -> [Cs_element001,F_element006]
  conduct = 2
  density = 1
  expand = 3
  formula = G4_CESIUM_FLUORIDE
  name = G4_CESIUM_FLUORIDE
  specific = 4
FEATURE [App::DocumentObjectGroupPython] Cs_element002  label="Cs_element : 002"  # scripted group (container) (typed FeaturePython)
  n = 1
  ref = Cs_element
FEATURE [App::DocumentObjectGroupPython] I_element001  label="I_element : 1"  # scripted group (container) (typed FeaturePython)
  n = 1
  ref = I_element
FEATURE [App::DocumentObjectGroupPython] G4_CESIUM_IODIDE001  label="G4_CESIUM_IODIDE"  # scripted group (container) (typed FeaturePython)
  Dunit = g/cm3
  Dvalue = 4.51
  Group = -> [Cs_element002,I_element001]
  conduct = 2
  density = 1
  expand = 3
  formula = G4_CESIUM_IODIDE
  name = G4_CESIUM_IODIDE
  specific = 4
FEATURE [App::DocumentObjectGroupPython] C_element028  label="C_element : 013"  # scripted group (container) (typed FeaturePython)
  n = 6
  ref = C_element
FEATURE [App::DocumentObjectGroupPython] H_element025  label="H_element : 013"  # scripted group (container) (typed FeaturePython)
  n = 5
  ref = H_element
FEATURE [App::DocumentObjectGroupPython] Cl_element005  label="Cl_element : 1"  # scripted group (container) (typed FeaturePython)
  n = 1
  ref = Cl_element
FEATURE [App::DocumentObjectGroupPython] G4_CHLOROBENZENE  # scripted group (container) (typed FeaturePython)
  Dunit = g/cm3
  Dvalue = 1.1058
  Group = -> [C_element028,H_element025,Cl_element005]
  conduct = 2
  density = 1
  expand = 3
  formula = G4_CHLOROBENZENE
  name = G4_CHLOROBENZENE
  specific = 4
FEATURE [App::DocumentObjectGroupPython] C_element029  label="C_element : 014"  # scripted group (container) (typed FeaturePython)
  n = 1
  ref = C_element
FEATURE [App::DocumentObjectGroupPython] H_element026  label="H_element : 1"  # scripted group (container) (typed FeaturePython)
  n = 1
  ref = H_element
FEATURE [App::DocumentObjectGroupPython] Cl_element006  label="Cl_element : 3"  # scripted group (container) (typed FeaturePython)
  n = 3
  ref = Cl_element
FEATURE [App::DocumentObjectGroupPython] G4_CHLOROFORM  # scripted group (container) (typed FeaturePython)
  Dunit = g/cm3
  Dvalue = 1.4832
  Group = -> [C_element029,H_element026,Cl_element006]
  conduct = 2
  density = 1
  expand = 3
  formula = G4_CHLOROFORM
  name = G4_CHLOROFORM
  specific = 4
FEATURE [App::DocumentObjectGroupPython] H_element027  label="H_element : 0.010"  # scripted group (container) (typed FeaturePython)
  n = 0.01
FEATURE [App::DocumentObjectGroupPython] C_element030  label="C_element : 0.001"  # scripted group (container) (typed FeaturePython)
  n = 0.001
FEATURE [App::DocumentObjectGroupPython] O_element030  label="O_element : 0.529"  # scripted group (container) (typed FeaturePython)
  n = 0.529107
FEATURE [App::DocumentObjectGroupPython] Na_element005  label="Na_element : 0.016"  # scripted group (container) (typed FeaturePython)
  n = 0.016
FEATURE [App::DocumentObjectGroupPython] Mg_element003  label="Mg_element : 0.004"  # scripted group (container) (typed FeaturePython)
  n = 0.002
FEATURE [App::DocumentObjectGroupPython] Al_element002  label="Al_element : 0.034"  # scripted group (container) (typed FeaturePython)
  n = 0.033872
FEATURE [App::DocumentObjectGroupPython] Si_element002  label="Si_element : 0.337"  # scripted group (container) (typed FeaturePython)
  n = 0.337021
FEATURE [App::DocumentObjectGroupPython] K_element003  label="K_element : 0.013"  # scripted group (container) (typed FeaturePython)
  n = 0.013
FEATURE [App::DocumentObjectGroupPython] Ca_element010  label="Ca_element : 0.044"  # scripted group (container) (typed FeaturePython)
  n = 0.044
FEATURE [App::DocumentObjectGroupPython] Fe_element002  label="Fe_element : 0.014"  # scripted group (container) (typed FeaturePython)
  n = 0.014
FEATURE [App::DocumentObjectGroupPython] G4_CONCRETE  # scripted group (container) (typed FeaturePython)
  Dunit = g/cm3
  Dvalue = 2.3
  Group = -> [H_element027,C_element030,O_element030,Na_element005,Mg_element003,Al_element002,Si_element002,K_element003,Ca_element010,Fe_element002]
  conduct = 2
  density = 1
  expand = 3
  formula = G4_CONCRETE
  name = G4_CONCRETE
  specific = 4
FEATURE [App::DocumentObjectGroupPython] C_element031  label="C_element : 015"  # scripted group (container) (typed FeaturePython)
  n = 6
  ref = C_element
FEATURE [App::DocumentObjectGroupPython] H_element028  label="H_element : 12"  # scripted group (container) (typed FeaturePython)
  n = 12
  ref = H_element
FEATURE [App::DocumentObjectGroupPython] G4_CYCLOHEXANE  # scripted group (container) (typed FeaturePython)
  Dunit = g/cm3
  Dvalue = 0.779
  Group = -> [C_element031,H_element028]
  conduct = 2
  density = 1
  expand = 3
  formula = G4_CYCLOHEXANE
  name = G4_CYCLOHEXANE
  specific = 4
FEATURE [App::DocumentObjectGroupPython] C_element032  label="C_element : 016"  # scripted group (container) (typed FeaturePython)
  n = 6
  ref = C_element
FEATURE [App::DocumentObjectGroupPython] H_element029  label="H_element : 4"  # scripted group (container) (typed FeaturePython)
  n = 4
  ref = H_element
FEATURE [App::DocumentObjectGroupPython] Cl_element007  label="Cl_element : 2"  # scripted group (container) (typed FeaturePython)
  n = 2
  ref = Cl_element
FEATURE [App::DocumentObjectGroupPython] G4_1_2_DICHLOROBENZENE  label="G4_1.2-DICHLOROBENZENE"  # scripted group (container) (typed FeaturePython)
  Dunit = g/cm3
  Dvalue = 1.3048
  Group = -> [C_element032,H_element029,Cl_element007]
  conduct = 2
  density = 1
  expand = 3
  formula = G4_1.2-DICHLOROBENZENE
  name = G4_1.2-DICHLOROBENZENE
  specific = 4
FEATURE [App::DocumentObjectGroupPython] C_element033  label="C_element : 017"  # scripted group (container) (typed FeaturePython)
  n = 4
  ref = C_element
FEATURE [App::DocumentObjectGroupPython] H_element030  label="H_element : 8"  # scripted group (container) (typed FeaturePython)
  n = 8
  ref = H_element
FEATURE [App::DocumentObjectGroupPython] O_element031  label="O_element : 014"  # scripted group (container) (typed FeaturePython)
  n = 1
  ref = O_element
FEATURE [App::DocumentObjectGroupPython] Cl_element008  label="Cl_element : 005"  # scripted group (container) (typed FeaturePython)
  n = 2
  ref = Cl_element
FEATURE [App::DocumentObjectGroupPython] G4_DICHLORODIETHYL_ETHER  # scripted group (container) (typed FeaturePython)
  Dunit = g/cm3
  Dvalue = 1.2199
  Group = -> [C_element033,H_element030,O_element031,Cl_element008]
  conduct = 2
  density = 1
  expand = 3
  formula = G4_DICHLORODIETHYL_ETHER
  name = G4_DICHLORODIETHYL_ETHER
  specific = 4
FEATURE [App::DocumentObjectGroupPython] C_element034  label="C_element : 018"  # scripted group (container) (typed FeaturePython)
  n = 2
  ref = C_element
FEATURE [App::DocumentObjectGroupPython] H_element031  label="H_element : 014"  # scripted group (container) (typed FeaturePython)
  n = 4
  ref = H_element
FEATURE [App::DocumentObjectGroupPython] Cl_element009  label="Cl_element : 006"  # scripted group (container) (typed FeaturePython)
  n = 2
  ref = Cl_element
FEATURE [App::DocumentObjectGroupPython] G4_1_2_DICHLOROETHANE  label="G4_1.2-DICHLOROETHANE"  # scripted group (container) (typed FeaturePython)
  Dunit = g/cm3
  Dvalue = 1.2351
  Group = -> [C_element034,H_element031,Cl_element009]
  conduct = 2
  density = 1
  expand = 3
  formula = G4_1.2-DICHLOROETHANE
  name = G4_1.2-DICHLOROETHANE
  specific = 4
FEATURE [App::DocumentObjectGroupPython] C_element035  label="C_element : 019"  # scripted group (container) (typed FeaturePython)
  n = 4
  ref = C_element
FEATURE [App::DocumentObjectGroupPython] H_element032  label="H_element : 015"  # scripted group (container) (typed FeaturePython)
  n = 10
  ref = H_element
FEATURE [App::DocumentObjectGroupPython] O_element032  label="O_element : 015"  # scripted group (container) (typed FeaturePython)
  n = 1
  ref = O_element
FEATURE [App::DocumentObjectGroupPython] G4_DIETHYL_ETHER  # scripted group (container) (typed FeaturePython)
  Dunit = g/cm3
  Dvalue = 0.71378
  Group = -> [C_element035,H_element032,O_element032]
  conduct = 2
  density = 1
  expand = 3
  formula = G4_DIETHYL_ETHER
  name = G4_DIETHYL_ETHER
  specific = 4
FEATURE [App::DocumentObjectGroupPython] C_element036  label="C_element : 020"  # scripted group (container) (typed FeaturePython)
  n = 3
  ref = C_element
FEATURE [App::DocumentObjectGroupPython] H_element033  label="H_element : 016"  # scripted group (container) (typed FeaturePython)
  n = 7
  ref = H_element
FEATURE [App::DocumentObjectGroupPython] N_element015  label="N_element : 008"  # scripted group (container) (typed FeaturePython)
  n = 1
  ref = N_element
FEATURE [App::DocumentObjectGroupPython] O_element033  label="O_element : 016"  # scripted group (container) (typed FeaturePython)
  n = 1
  ref = O_element
FEATURE [App::DocumentObjectGroupPython] G4_N_N_DIMETHYL_FORMAMIDE  label="G4_N.N-DIMETHYL_FORMAMIDE"  # scripted group (container) (typed FeaturePython)
  Dunit = g/cm3
  Dvalue = 0.9487
  Group = -> [C_element036,H_element033,N_element015,O_element033]
  conduct = 2
  density = 1
  expand = 3
  formula = G4_N.N-DIMETHYL_FORMAMIDE
  name = G4_N.N-DIMETHYL_FORMAMIDE
  specific = 4
FEATURE [App::DocumentObjectGroupPython] C_element037  label="C_element : 021"  # scripted group (container) (typed FeaturePython)
  n = 2
  ref = C_element
FEATURE [App::DocumentObjectGroupPython] H_element034  label="H_element : 017"  # scripted group (container) (typed FeaturePython)
  n = 6
  ref = H_element
FEATURE [App::DocumentObjectGroupPython] O_element034  label="O_element : 017"  # scripted group (container) (typed FeaturePython)
  n = 1
  ref = O_element
FEATURE [App::DocumentObjectGroupPython] S_element009  label="S_element : 003"  # scripted group (container) (typed FeaturePython)
  n = 1
  ref = S_element
FEATURE [App::DocumentObjectGroupPython] G4_DIMETHYL_SULFOXIDE  # scripted group (container) (typed FeaturePython)
  Dunit = g/cm3
  Dvalue = 1.1014
  Group = -> [C_element037,H_element034,O_element034,S_element009]
  conduct = 2
  density = 1
  expand = 3
  formula = G4_DIMETHYL_SULFOXIDE
  name = G4_DIMETHYL_SULFOXIDE
  specific = 4
FEATURE [App::DocumentObjectGroupPython] C_element038  label="C_element : 022"  # scripted group (container) (typed FeaturePython)
  n = 2
  ref = C_element
FEATURE [App::DocumentObjectGroupPython] H_element035  label="H_element : 018"  # scripted group (container) (typed FeaturePython)
  n = 6
  ref = H_element
FEATURE [App::DocumentObjectGroupPython] G4_ETHANE  # scripted group (container) (typed FeaturePython)
  Dunit = g/cm3
  Dvalue = 0.00125324
  Group = -> [C_element038,H_element035]
  conduct = 2
  density = 1
  expand = 3
  formula = G4_ETHANE
  name = G4_ETHANE
  specific = 4
FEATURE [App::DocumentObjectGroupPython] C_element039  label="C_element : 023"  # scripted group (container) (typed FeaturePython)
  n = 2
  ref = C_element
FEATURE [App::DocumentObjectGroupPython] H_element036  label="H_element : 019"  # scripted group (container) (typed FeaturePython)
  n = 6
  ref = H_element
FEATURE [App::DocumentObjectGroupPython] O_element035  label="O_element : 018"  # scripted group (container) (typed FeaturePython)
  n = 1
  ref = O_element
FEATURE [App::DocumentObjectGroupPython] G4_ETHYL_ALCOHOL  # scripted group (container) (typed FeaturePython)
  Dunit = g/cm3
  Dvalue = 0.7893
  Group = -> [C_element039,H_element036,O_element035]
  conduct = 2
  density = 1
  expand = 3
  formula = G4_ETHYL_ALCOHOL
  name = G4_ETHYL_ALCOHOL
  specific = 4
FEATURE [App::DocumentObjectGroupPython] H_element037  label="H_element : 0.090"  # scripted group (container) (typed FeaturePython)
  n = 0.090027
FEATURE [App::DocumentObjectGroupPython] C_element040  label="C_element : 0.585"  # scripted group (container) (typed FeaturePython)
  n = 0.585182
FEATURE [App::DocumentObjectGroupPython] O_element036  label="O_element : 0.325"  # scripted group (container) (typed FeaturePython)
  n = 0.324791
FEATURE [App::DocumentObjectGroupPython] G4_ETHYL_CELLULOSE  # scripted group (container) (typed FeaturePython)
  Dunit = g/cm3
  Dvalue = 1.13
  Group = -> [H_element037,C_element040,O_element036]
  conduct = 2
  density = 1
  expand = 3
  formula = G4_ETHYL_CELLULOSE
  name = G4_ETHYL_CELLULOSE
  specific = 4
FEATURE [App::DocumentObjectGroupPython] C_element041  label="C_element : 024"  # scripted group (container) (typed FeaturePython)
  n = 2
  ref = C_element
FEATURE [App::DocumentObjectGroupPython] H_element038  label="H_element : 020"  # scripted group (container) (typed FeaturePython)
  n = 4
  ref = H_element
FEATURE [App::DocumentObjectGroupPython] G4_ETHYLENE  # scripted group (container) (typed FeaturePython)
  Dunit = g/cm3
  Dvalue = 0.00117497
  Group = -> [C_element041,H_element038]
  conduct = 2
  density = 1
  expand = 3
  formula = G4_ETHYLENE
  name = G4_ETHYLENE
  specific = 4
FEATURE [App::DocumentObjectGroupPython] H_element039  label="H_element : 0.096"  # scripted group (container) (typed FeaturePython)
  n = 0.096
FEATURE [App::DocumentObjectGroupPython] C_element042  label="C_element : 0.195"  # scripted group (container) (typed FeaturePython)
  n = 0.195
FEATURE [App::DocumentObjectGroupPython] N_element016  label="N_element : 0.057"  # scripted group (container) (typed FeaturePython)
  n = 0.057
FEATURE [App::DocumentObjectGroupPython] O_element037  label="O_element : 0.646"  # scripted group (container) (typed FeaturePython)
  n = 0.646
FEATURE [App::DocumentObjectGroupPython] Na_element006  label="Na_element : 0.017"  # scripted group (container) (typed FeaturePython)
  n = 0.001
FEATURE [App::DocumentObjectGroupPython] P_element005  label="P_element : 0.104"  # scripted group (container) (typed FeaturePython)
  n = 0.001
FEATURE [App::DocumentObjectGroupPython] S_element010  label="S_element : 0.016"  # scripted group (container) (typed FeaturePython)
  n = 0.003
FEATURE [App::DocumentObjectGroupPython] Cl_element010  label="Cl_element : 0.005"  # scripted group (container) (typed FeaturePython)
  n = 0.001
FEATURE [App::DocumentObjectGroupPython] G4_EYE_LENS_ICRP  # scripted group (container) (typed FeaturePython)
  Dunit = g/cm3
  Dvalue = 1.07
  Group = -> [H_element039,C_element042,N_element016,O_element037,Na_element006,P_element005,S_element010,Cl_element010]
  conduct = 2
  density = 1
  expand = 3
  formula = G4_EYE_LENS_ICRP
  name = G4_EYE_LENS_ICRP
  specific = 4
FEATURE [App::DocumentObjectGroupPython] Fe_element003  label="Fe_element : 2"  # scripted group (container) (typed FeaturePython)
  n = 2
  ref = Fe_element
FEATURE [App::DocumentObjectGroupPython] O_element038  label="O_element : 019"  # scripted group (container) (typed FeaturePython)
  n = 3
  ref = O_element
FEATURE [App::DocumentObjectGroupPython] G4_FERRIC_OXIDE  # scripted group (container) (typed FeaturePython)
  Dunit = g/cm3
  Dvalue = 5.2
  Group = -> [Fe_element003,O_element038]
  conduct = 2
  density = 1
  expand = 3
  formula = G4_FERRIC_OXIDE
  name = G4_FERRIC_OXIDE
  specific = 4
FEATURE [App::DocumentObjectGroupPython] Fe_element004  label="Fe_element : 1"  # scripted group (container) (typed FeaturePython)
  n = 1
  ref = Fe_element
FEATURE [App::DocumentObjectGroupPython] B_element003  label="B_element : 1"  # scripted group (container) (typed FeaturePython)
  n = 1
  ref = B_element
FEATURE [App::DocumentObjectGroupPython] G4_FERROBORIDE  # scripted group (container) (typed FeaturePython)
  Dunit = g/cm3
  Dvalue = 7.15
  Group = -> [Fe_element004,B_element003]
  conduct = 2
  density = 1
  expand = 3
  formula = G4_FERROBORIDE
  name = G4_FERROBORIDE
  specific = 4
FEATURE [App::DocumentObjectGroupPython] Fe_element005  label="Fe_element : 003"  # scripted group (container) (typed FeaturePython)
  n = 1
  ref = Fe_element
FEATURE [App::DocumentObjectGroupPython] O_element039  label="O_element : 020"  # scripted group (container) (typed FeaturePython)
  n = 1
  ref = O_element
FEATURE [App::DocumentObjectGroupPython] G4_FERROUS_OXIDE  # scripted group (container) (typed FeaturePython)
  Dunit = g/cm3
  Dvalue = 5.7
  Group = -> [Fe_element005,O_element039]
  conduct = 2
  density = 1
  expand = 3
  formula = G4_FERROUS_OXIDE
  name = G4_FERROUS_OXIDE
  specific = 4
FEATURE [App::DocumentObjectGroupPython] H_element040  label="H_element : 0.115"  # scripted group (container) (typed FeaturePython)
  n = 0.108259
FEATURE [App::DocumentObjectGroupPython] N_element017  label="N_element : 0.000"  # scripted group (container) (typed FeaturePython)
  n = 2.7e-05
FEATURE [App::DocumentObjectGroupPython] O_element040  label="O_element : 0.879"  # scripted group (container) (typed FeaturePython)
  n = 0.878636
FEATURE [App::DocumentObjectGroupPython] Na_element007  label="Na_element : 0.000"  # scripted group (container) (typed FeaturePython)
  n = 2.2e-05
FEATURE [App::DocumentObjectGroupPython] S_element011  label="S_element : 0.013"  # scripted group (container) (typed FeaturePython)
  n = 0.012968
FEATURE [App::DocumentObjectGroupPython] Cl_element011  label="Cl_element : 0.000"  # scripted group (container) (typed FeaturePython)
  n = 3.4e-05
FEATURE [App::DocumentObjectGroupPython] Fe_element006  label="Fe_element : 0.000"  # scripted group (container) (typed FeaturePython)
  n = 5.4e-05
FEATURE [App::DocumentObjectGroupPython] G4_FERROUS_SULFATE  # scripted group (container) (typed FeaturePython)
  Dunit = g/cm3
  Dvalue = 1.024
  Group = -> [H_element040,N_element017,O_element040,Na_element007,S_element011,Cl_element011,Fe_element006]
  conduct = 2
  density = 1
  expand = 3
  formula = G4_FERROUS_SULFATE
  name = G4_FERROUS_SULFATE
  specific = 4
FEATURE [App::DocumentObjectGroupPython] C_element043  label="C_element : 0.099"  # scripted group (container) (typed FeaturePython)
  n = 0.099335
FEATURE [App::DocumentObjectGroupPython] F_element007  label="F_element : 0.314"  # scripted group (container) (typed FeaturePython)
  n = 0.314247
FEATURE [App::DocumentObjectGroupPython] Cl_element012  label="Cl_element : 0.586"  # scripted group (container) (typed FeaturePython)
  n = 0.586418
FEATURE [App::DocumentObjectGroupPython] G4_FREON_12  label="G4_FREON-12"  # scripted group (container) (typed FeaturePython)
  Dunit = g/cm3
  Dvalue = 1.12
  Group = -> [C_element043,F_element007,Cl_element012]
  conduct = 2
  density = 1
  expand = 3
  formula = G4_FREON-12
  name = G4_FREON-12
  specific = 4
FEATURE [App::DocumentObjectGroupPython] C_element044  label="C_element : 0.057"  # scripted group (container) (typed FeaturePython)
  n = 0.057245
FEATURE [App::DocumentObjectGroupPython] F_element008  label="F_element : 0.181"  # scripted group (container) (typed FeaturePython)
  n = 0.181096
FEATURE [App::DocumentObjectGroupPython] Br_element001  label="Br_element : 0.762"  # scripted group (container) (typed FeaturePython)
  n = 0.761659
FEATURE [App::DocumentObjectGroupPython] G4_FREON_12B2  label="G4_FREON-12B2"  # scripted group (container) (typed FeaturePython)
  Dunit = g/cm3
  Dvalue = 1.8
  Group = -> [C_element044,F_element008,Br_element001]
  conduct = 2
  density = 1
  expand = 3
  formula = G4_FREON-12B2
  name = G4_FREON-12B2
  specific = 4
FEATURE [App::DocumentObjectGroupPython] C_element045  label="C_element : 0.115"  # scripted group (container) (typed FeaturePython)
  n = 0.114983
FEATURE [App::DocumentObjectGroupPython] F_element009  label="F_element : 0.546"  # scripted group (container) (typed FeaturePython)
  n = 0.545621
FEATURE [App::DocumentObjectGroupPython] Cl_element013  label="Cl_element : 0.339"  # scripted group (container) (typed FeaturePython)
  n = 0.339396
FEATURE [App::DocumentObjectGroupPython] G4_FREON_13  label="G4_FREON-13"  # scripted group (container) (typed FeaturePython)
  Dunit = g/cm3
  Dvalue = 0.95
  Group = -> [C_element045,F_element009,Cl_element013]
  conduct = 2
  density = 1
  expand = 3
  formula = G4_FREON-13
  name = G4_FREON-13
  specific = 4
FEATURE [App::DocumentObjectGroupPython] C_element046  label="C_element : 025"  # scripted group (container) (typed FeaturePython)
  n = 1
  ref = C_element
FEATURE [App::DocumentObjectGroupPython] F_element010  label="F_element : 3"  # scripted group (container) (typed FeaturePython)
  n = 3
  ref = F_element
FEATURE [App::DocumentObjectGroupPython] Br_element002  label="Br_element : 1"  # scripted group (container) (typed FeaturePython)
  n = 1
  ref = Br_element
FEATURE [App::DocumentObjectGroupPython] G4_FREON_13B1  label="G4_FREON-13B1"  # scripted group (container) (typed FeaturePython)
  Dunit = g/cm3
  Dvalue = 1.5
  Group = -> [C_element046,F_element010,Br_element002]
  conduct = 2
  density = 1
  expand = 3
  formula = G4_FREON-13B1
  name = G4_FREON-13B1
  specific = 4
FEATURE [App::DocumentObjectGroupPython] C_element047  label="C_element : 0.061"  # scripted group (container) (typed FeaturePython)
  n = 0.061309
FEATURE [App::DocumentObjectGroupPython] F_element011  label="F_element : 0.291"  # scripted group (container) (typed FeaturePython)
  n = 0.290924
FEATURE [App::DocumentObjectGroupPython] I_element002  label="I_element : 0.648"  # scripted group (container) (typed FeaturePython)
  n = 0.647767
FEATURE [App::DocumentObjectGroupPython] G4_FREON_13I1  label="G4_FREON-13I1"  # scripted group (container) (typed FeaturePython)
  Dunit = g/cm3
  Dvalue = 1.8
  Group = -> [C_element047,F_element011,I_element002]
  conduct = 2
  density = 1
  expand = 3
  formula = G4_FREON-13I1
  name = G4_FREON-13I1
  specific = 4
FEATURE [App::DocumentObjectGroupPython] Gd_element001  label="Gd_element : 2"  # scripted group (container) (typed FeaturePython)
  n = 2
  ref = Gd_element
FEATURE [App::DocumentObjectGroupPython] O_element041  label="O_element : 021"  # scripted group (container) (typed FeaturePython)
  n = 2
  ref = O_element
FEATURE [App::DocumentObjectGroupPython] S_element012  label="S_element : 004"  # scripted group (container) (typed FeaturePython)
  n = 1
  ref = S_element
FEATURE [App::DocumentObjectGroupPython] G4_GADOLINIUM_OXYSULFIDE  # scripted group (container) (typed FeaturePython)
  Dunit = g/cm3
  Dvalue = 7.44
  Group = -> [Gd_element001,O_element041,S_element012]
  conduct = 2
  density = 1
  expand = 3
  formula = G4_GADOLINIUM_OXYSULFIDE
  name = G4_GADOLINIUM_OXYSULFIDE
  specific = 4
FEATURE [App::DocumentObjectGroupPython] Ga_element001  label="Ga_element : 1"  # scripted group (container) (typed FeaturePython)
  n = 1
  ref = Ga_element
FEATURE [App::DocumentObjectGroupPython] As_element001  label="As_element : 1"  # scripted group (container) (typed FeaturePython)
  n = 1
  ref = As_element
FEATURE [App::DocumentObjectGroupPython] G4_GALLIUM_ARSENIDE  # scripted group (container) (typed FeaturePython)
  Dunit = g/cm3
  Dvalue = 5.31
  Group = -> [Ga_element001,As_element001]
  conduct = 2
  density = 1
  expand = 3
  formula = G4_GALLIUM_ARSENIDE
  name = G4_GALLIUM_ARSENIDE
  specific = 4
FEATURE [App::DocumentObjectGroupPython] H_element041  label="H_element : 0.081"  # scripted group (container) (typed FeaturePython)
  n = 0.08118
FEATURE [App::DocumentObjectGroupPython] C_element048  label="C_element : 0.416"  # scripted group (container) (typed FeaturePython)
  n = 0.41606
FEATURE [App::DocumentObjectGroupPython] N_element018  label="N_element : 0.111"  # scripted group (container) (typed FeaturePython)
  n = 0.11124
FEATURE [App::DocumentObjectGroupPython] O_element042  label="O_element : 0.381"  # scripted group (container) (typed FeaturePython)
  n = 0.38064
FEATURE [App::DocumentObjectGroupPython] S_element013  label="S_element : 0.011"  # scripted group (container) (typed FeaturePython)
  n = 0.01088
FEATURE [App::DocumentObjectGroupPython] G4_GEL_PHOTO_EMULSION  # scripted group (container) (typed FeaturePython)
  Dunit = g/cm3
  Dvalue = 1.2914
  Group = -> [H_element041,C_element048,N_element018,O_element042,S_element013]
  conduct = 2
  density = 1
  expand = 3
  formula = G4_GEL_PHOTO_EMULSION
  name = G4_GEL_PHOTO_EMULSION
  specific = 4
FEATURE [App::DocumentObjectGroupPython] B_element004  label="B_element : 0.040"  # scripted group (container) (typed FeaturePython)
  n = 0.0400639
FEATURE [App::DocumentObjectGroupPython] O_element043  label="O_element : 0.540"  # scripted group (container) (typed FeaturePython)
  n = 0.539561
FEATURE [App::DocumentObjectGroupPython] Na_element008  label="Na_element : 0.028"  # scripted group (container) (typed FeaturePython)
  n = 0.0281909
FEATURE [App::DocumentObjectGroupPython] Al_element003  label="Al_element : 0.012"  # scripted group (container) (typed FeaturePython)
  n = 0.011644
FEATURE [App::DocumentObjectGroupPython] Si_element003  label="Si_element : 0.377"  # scripted group (container) (typed FeaturePython)
  n = 0.377219
FEATURE [App::DocumentObjectGroupPython] K_element004  label="K_element : 0.014"  # scripted group (container) (typed FeaturePython)
  n = 0.00332099
FEATURE [App::DocumentObjectGroupPython] G4_Pyrex_Glass  # scripted group (container) (typed FeaturePython)
  Dunit = g/cm3
  Dvalue = 2.23
  Group = -> [B_element004,O_element043,Na_element008,Al_element003,Si_element003,K_element004]
  conduct = 2
  density = 1
  expand = 3
  formula = G4_Pyrex_Glass
  name = G4_Pyrex_Glass
  specific = 4
FEATURE [App::DocumentObjectGroupPython] O_element044  label="O_element : 0.156"  # scripted group (container) (typed FeaturePython)
  n = 0.156453
FEATURE [App::DocumentObjectGroupPython] Si_element004  label="Si_element : 0.081"  # scripted group (container) (typed FeaturePython)
  n = 0.080866
FEATURE [App::DocumentObjectGroupPython] Ti_element001  label="Ti_element : 0.008"  # scripted group (container) (typed FeaturePython)
  n = 0.008092
FEATURE [App::DocumentObjectGroupPython] As_element002  label="As_element : 0.003"  # scripted group (container) (typed FeaturePython)
  n = 0.002651
FEATURE [App::DocumentObjectGroupPython] Pb_element001  label="Pb_element : 0.752"  # scripted group (container) (typed FeaturePython)
  n = 0.751938
FEATURE [App::DocumentObjectGroupPython] G4_GLASS_LEAD  # scripted group (container) (typed FeaturePython)
  Dunit = g/cm3
  Dvalue = 6.22
  Group = -> [O_element044,Si_element004,Ti_element001,As_element002,Pb_element001]
  conduct = 2
  density = 1
  expand = 3
  formula = G4_GLASS_LEAD
  name = G4_GLASS_LEAD
  specific = 4
FEATURE [App::DocumentObjectGroupPython] O_element045  label="O_element : 0.460"  # scripted group (container) (typed FeaturePython)
  n = 0.4598
FEATURE [App::DocumentObjectGroupPython] Na_element009  label="Na_element : 0.096"  # scripted group (container) (typed FeaturePython)
  n = 0.0964411
FEATURE [App::DocumentObjectGroupPython] Si_element005  label="Si_element : 0.378"  # scripted group (container) (typed FeaturePython)
  n = 0.336553
FEATURE [App::DocumentObjectGroupPython] Ca_element011  label="Ca_element : 0.107"  # scripted group (container) (typed FeaturePython)
  n = 0.107205
FEATURE [App::DocumentObjectGroupPython] G4_GLASS_PLATE  # scripted group (container) (typed FeaturePython)
  Dunit = g/cm3
  Dvalue = 2.4
  Group = -> [O_element045,Na_element009,Si_element005,Ca_element011]
  conduct = 2
  density = 1
  expand = 3
  formula = G4_GLASS_PLATE
  name = G4_GLASS_PLATE
  specific = 4
FEATURE [App::DocumentObjectGroupPython] C_element049  label="C_element : 026"  # scripted group (container) (typed FeaturePython)
  n = 5
  ref = C_element
FEATURE [App::DocumentObjectGroupPython] H_element042  label="H_element : 021"  # scripted group (container) (typed FeaturePython)
  n = 10
  ref = H_element
FEATURE [App::DocumentObjectGroupPython] N_element019  label="N_element : 2"  # scripted group (container) (typed FeaturePython)
  n = 2
  ref = N_element
FEATURE [App::DocumentObjectGroupPython] O_element046  label="O_element : 022"  # scripted group (container) (typed FeaturePython)
  n = 3
  ref = O_element
FEATURE [App::DocumentObjectGroupPython] G4_GLUTAMINE  # scripted group (container) (typed FeaturePython)
  Dunit = g/cm3
  Dvalue = 1.46
  Group = -> [C_element049,H_element042,N_element019,O_element046]
  conduct = 2
  density = 1
  expand = 3
  formula = G4_GLUTAMINE
  name = G4_GLUTAMINE
  specific = 4
FEATURE [App::DocumentObjectGroupPython] C_element050  label="C_element : 027"  # scripted group (container) (typed FeaturePython)
  n = 3
  ref = C_element
FEATURE [App::DocumentObjectGroupPython] H_element043  label="H_element : 022"  # scripted group (container) (typed FeaturePython)
  n = 8
  ref = H_element
FEATURE [App::DocumentObjectGroupPython] O_element047  label="O_element : 023"  # scripted group (container) (typed FeaturePython)
  n = 3
  ref = O_element
FEATURE [App::DocumentObjectGroupPython] G4_GLYCEROL  # scripted group (container) (typed FeaturePython)
  Dunit = g/cm3
  Dvalue = 1.2613
  Group = -> [C_element050,H_element043,O_element047]
  conduct = 2
  density = 1
  expand = 3
  formula = G4_GLYCEROL
  name = G4_GLYCEROL
  specific = 4
FEATURE [App::DocumentObjectGroupPython] C_element051  label="C_element : 028"  # scripted group (container) (typed FeaturePython)
  n = 5
  ref = C_element
FEATURE [App::DocumentObjectGroupPython] H_element044  label="H_element : 023"  # scripted group (container) (typed FeaturePython)
  n = 5
  ref = H_element
FEATURE [App::DocumentObjectGroupPython] N_element020  label="N_element : 009"  # scripted group (container) (typed FeaturePython)
  n = 5
  ref = N_element
FEATURE [App::DocumentObjectGroupPython] O_element048  label="O_element : 024"  # scripted group (container) (typed FeaturePython)
  n = 1
  ref = O_element
FEATURE [App::DocumentObjectGroupPython] G4_GUANINE  # scripted group (container) (typed FeaturePython)
  Dunit = g/cm3
  Dvalue = 2.2
  Group = -> [C_element051,H_element044,N_element020,O_element048]
  conduct = 2
  density = 1
  expand = 3
  formula = G4_GUANINE
  name = G4_GUANINE
  specific = 4
FEATURE [App::DocumentObjectGroupPython] Ca_element012  label="Ca_element : 006"  # scripted group (container) (typed FeaturePython)
  n = 1
  ref = Ca_element
FEATURE [App::DocumentObjectGroupPython] S_element014  label="S_element : 005"  # scripted group (container) (typed FeaturePython)
  n = 1
  ref = S_element
FEATURE [App::DocumentObjectGroupPython] O_element049  label="O_element : 6"  # scripted group (container) (typed FeaturePython)
  n = 6
  ref = O_element
FEATURE [App::DocumentObjectGroupPython] H_element045  label="H_element : 024"  # scripted group (container) (typed FeaturePython)
  n = 4
  ref = H_element
FEATURE [App::DocumentObjectGroupPython] G4_GYPSUM  # scripted group (container) (typed FeaturePython)
  Dunit = g/cm3
  Dvalue = 2.32
  Group = -> [Ca_element012,S_element014,O_element049,H_element045]
  conduct = 2
  density = 1
  expand = 3
  formula = G4_GYPSUM
  name = G4_GYPSUM
  specific = 4
FEATURE [App::DocumentObjectGroupPython] C_element052  label="C_element : 7"  # scripted group (container) (typed FeaturePython)
  n = 7
  ref = C_element
FEATURE [App::DocumentObjectGroupPython] H_element046  label="H_element : 16"  # scripted group (container) (typed FeaturePython)
  n = 16
  ref = H_element
FEATURE [App::DocumentObjectGroupPython] G4_N_HEPTANE  label="G4_N-HEPTANE"  # scripted group (container) (typed FeaturePython)
  Dunit = g/cm3
  Dvalue = 0.68376
  Group = -> [C_element052,H_element046]
  conduct = 2
  density = 1
  expand = 3
  formula = G4_N-HEPTANE
  name = G4_N-HEPTANE
  specific = 4
FEATURE [App::DocumentObjectGroupPython] C_element053  label="C_element : 029"  # scripted group (container) (typed FeaturePython)
  n = 6
  ref = C_element
FEATURE [App::DocumentObjectGroupPython] H_element047  label="H_element : 14"  # scripted group (container) (typed FeaturePython)
  n = 14
  ref = H_element
FEATURE [App::DocumentObjectGroupPython] G4_N_HEXANE  label="G4_N-HEXANE"  # scripted group (container) (typed FeaturePython)
  Dunit = g/cm3
  Dvalue = 0.6603
  Group = -> [C_element053,H_element047]
  conduct = 2
  density = 1
  expand = 3
  formula = G4_N-HEXANE
  name = G4_N-HEXANE
  specific = 4
FEATURE [App::DocumentObjectGroupPython] C_element054  label="C_element : 22"  # scripted group (container) (typed FeaturePython)
  n = 22
  ref = C_element
FEATURE [App::DocumentObjectGroupPython] H_element048  label="H_element : 025"  # scripted group (container) (typed FeaturePython)
  n = 10
  ref = H_element
FEATURE [App::DocumentObjectGroupPython] N_element021  label="N_element : 010"  # scripted group (container) (typed FeaturePython)
  n = 2
  ref = N_element
FEATURE [App::DocumentObjectGroupPython] O_element050  label="O_element : 025"  # scripted group (container) (typed FeaturePython)
  n = 5
  ref = O_element
FEATURE [App::DocumentObjectGroupPython] G4_KAPTON  # scripted group (container) (typed FeaturePython)
  Dunit = g/cm3
  Dvalue = 1.42
  Group = -> [C_element054,H_element048,N_element021,O_element050]
  conduct = 2
  density = 1
  expand = 3
  formula = G4_KAPTON
  name = G4_KAPTON
  specific = 4
FEATURE [App::DocumentObjectGroupPython] La_element001  label="La_element : 1"  # scripted group (container) (typed FeaturePython)
  n = 1
  ref = La_element
FEATURE [App::DocumentObjectGroupPython] Br_element003  label="Br_element : 002"  # scripted group (container) (typed FeaturePython)
  n = 1
  ref = Br_element
FEATURE [App::DocumentObjectGroupPython] O_element051  label="O_element : 026"  # scripted group (container) (typed FeaturePython)
  n = 1
  ref = O_element
FEATURE [App::DocumentObjectGroupPython] G4_LANTHANUM_OXYBROMIDE  # scripted group (container) (typed FeaturePython)
  Dunit = g/cm3
  Dvalue = 6.28
  Group = -> [La_element001,Br_element003,O_element051]
  conduct = 2
  density = 1
  expand = 3
  formula = G4_LANTHANUM_OXYBROMIDE
  name = G4_LANTHANUM_OXYBROMIDE
  specific = 4
FEATURE [App::DocumentObjectGroupPython] La_element002  label="La_element : 2"  # scripted group (container) (typed FeaturePython)
  n = 2
  ref = La_element
FEATURE [App::DocumentObjectGroupPython] O_element052  label="O_element : 027"  # scripted group (container) (typed FeaturePython)
  n = 2
  ref = O_element
FEATURE [App::DocumentObjectGroupPython] S_element015  label="S_element : 006"  # scripted group (container) (typed FeaturePython)
  n = 1
  ref = S_element
FEATURE [App::DocumentObjectGroupPython] G4_LANTHANUM_OXYSULFIDE  # scripted group (container) (typed FeaturePython)
  Dunit = g/cm3
  Dvalue = 5.86
  Group = -> [La_element002,O_element052,S_element015]
  conduct = 2
  density = 1
  expand = 3
  formula = G4_LANTHANUM_OXYSULFIDE
  name = G4_LANTHANUM_OXYSULFIDE
  specific = 4
FEATURE [App::DocumentObjectGroupPython] O_element053  label="O_element : 0.072"  # scripted group (container) (typed FeaturePython)
  n = 0.071682
FEATURE [App::DocumentObjectGroupPython] Pb_element002  label="Pb_element : 0.928"  # scripted group (container) (typed FeaturePython)
  n = 0.928318
FEATURE [App::DocumentObjectGroupPython] G4_LEAD_OXIDE  # scripted group (container) (typed FeaturePython)
  Dunit = g/cm3
  Dvalue = 9.53
  Group = -> [O_element053,Pb_element002]
  conduct = 2
  density = 1
  expand = 3
  formula = G4_LEAD_OXIDE
  name = G4_LEAD_OXIDE
  specific = 4
FEATURE [App::DocumentObjectGroupPython] Li_element001  label="Li_element : 1"  # scripted group (container) (typed FeaturePython)
  n = 1
  ref = Li_element
FEATURE [App::DocumentObjectGroupPython] N_element022  label="N_element : 011"  # scripted group (container) (typed FeaturePython)
  n = 1
  ref = N_element
FEATURE [App::DocumentObjectGroupPython] H_element049  label="H_element : 026"  # scripted group (container) (typed FeaturePython)
  n = 2
  ref = H_element
FEATURE [App::DocumentObjectGroupPython] G4_LITHIUM_AMIDE  # scripted group (container) (typed FeaturePython)
  Dunit = g/cm3
  Dvalue = 1.178
  Group = -> [Li_element001,N_element022,H_element049]
  conduct = 2
  density = 1
  expand = 3
  formula = G4_LITHIUM_AMIDE
  name = G4_LITHIUM_AMIDE
  specific = 4
FEATURE [App::DocumentObjectGroupPython] Li_element002  label="Li_element : 2"  # scripted group (container) (typed FeaturePython)
  n = 2
  ref = Li_element
FEATURE [App::DocumentObjectGroupPython] C_element055  label="C_element : 030"  # scripted group (container) (typed FeaturePython)
  n = 1
  ref = C_element
FEATURE [App::DocumentObjectGroupPython] O_element054  label="O_element : 028"  # scripted group (container) (typed FeaturePython)
  n = 3
  ref = O_element
FEATURE [App::DocumentObjectGroupPython] G4_LITHIUM_CARBONATE  # scripted group (container) (typed FeaturePython)
  Dunit = g/cm3
  Dvalue = 2.11
  Group = -> [Li_element002,C_element055,O_element054]
  conduct = 2
  density = 1
  expand = 3
  formula = G4_LITHIUM_CARBONATE
  name = G4_LITHIUM_CARBONATE
  specific = 4
FEATURE [App::DocumentObjectGroupPython] Li_element003  label="Li_element : 003"  # scripted group (container) (typed FeaturePython)
  n = 1
  ref = Li_element
FEATURE [App::DocumentObjectGroupPython] F_element012  label="F_element : 004"  # scripted group (container) (typed FeaturePython)
  n = 1
  ref = F_element
FEATURE [App::DocumentObjectGroupPython] G4_LITHIUM_FLUORIDE  # scripted group (container) (typed FeaturePython)
  Dunit = g/cm3
  Dvalue = 2.635
  Group = -> [Li_element003,F_element012]
  conduct = 2
  density = 1
  expand = 3
  formula = G4_LITHIUM_FLUORIDE
  name = G4_LITHIUM_FLUORIDE
  specific = 4
FEATURE [App::DocumentObjectGroupPython] Li_element004  label="Li_element : 004"  # scripted group (container) (typed FeaturePython)
  n = 1
  ref = Li_element
FEATURE [App::DocumentObjectGroupPython] H_element050  label="H_element : 027"  # scripted group (container) (typed FeaturePython)
  n = 1
  ref = H_element
FEATURE [App::DocumentObjectGroupPython] G4_LITHIUM_HYDRIDE  # scripted group (container) (typed FeaturePython)
  Dunit = g/cm3
  Dvalue = 0.82
  Group = -> [Li_element004,H_element050]
  conduct = 2
  density = 1
  expand = 3
  formula = G4_LITHIUM_HYDRIDE
  name = G4_LITHIUM_HYDRIDE
  specific = 4
FEATURE [App::DocumentObjectGroupPython] Li_element005  label="Li_element : 005"  # scripted group (container) (typed FeaturePython)
  n = 1
  ref = Li_element
FEATURE [App::DocumentObjectGroupPython] I_element003  label="I_element : 002"  # scripted group (container) (typed FeaturePython)
  n = 1
  ref = I_element
FEATURE [App::DocumentObjectGroupPython] G4_LITHIUM_IODIDE  # scripted group (container) (typed FeaturePython)
  Dunit = g/cm3
  Dvalue = 3.494
  Group = -> [Li_element005,I_element003]
  conduct = 2
  density = 1
  expand = 3
  formula = G4_LITHIUM_IODIDE
  name = G4_LITHIUM_IODIDE
  specific = 4
FEATURE [App::DocumentObjectGroupPython] Li_element006  label="Li_element : 006"  # scripted group (container) (typed FeaturePython)
  n = 2
  ref = Li_element
FEATURE [App::DocumentObjectGroupPython] O_element055  label="O_element : 029"  # scripted group (container) (typed FeaturePython)
  n = 1
  ref = O_element
FEATURE [App::DocumentObjectGroupPython] G4_LITHIUM_OXIDE  # scripted group (container) (typed FeaturePython)
  Dunit = g/cm3
  Dvalue = 2.013
  Group = -> [Li_element006,O_element055]
  conduct = 2
  density = 1
  expand = 3
  formula = G4_LITHIUM_OXIDE
  name = G4_LITHIUM_OXIDE
  specific = 4
FEATURE [App::DocumentObjectGroupPython] Li_element007  label="Li_element : 007"  # scripted group (container) (typed FeaturePython)
  n = 2
  ref = Li_element
FEATURE [App::DocumentObjectGroupPython] B_element005  label="B_element : 005"  # scripted group (container) (typed FeaturePython)
  n = 4
  ref = B_element
FEATURE [App::DocumentObjectGroupPython] O_element056  label="O_element : 7"  # scripted group (container) (typed FeaturePython)
  n = 7
  ref = O_element
FEATURE [App::DocumentObjectGroupPython] G4_LITHIUM_TETRABORATE  # scripted group (container) (typed FeaturePython)
  Dunit = g/cm3
  Dvalue = 2.44
  Group = -> [Li_element007,B_element005,O_element056]
  conduct = 2
  density = 1
  expand = 3
  formula = G4_LITHIUM_TETRABORATE
  name = G4_LITHIUM_TETRABORATE
  specific = 4
FEATURE [App::DocumentObjectGroupPython] H_element051  label="H_element : 0.105"  # scripted group (container) (typed FeaturePython)
  n = 0.105
FEATURE [App::DocumentObjectGroupPython] C_element056  label="C_element : 0.083"  # scripted group (container) (typed FeaturePython)
  n = 0.083
FEATURE [App::DocumentObjectGroupPython] N_element023  label="N_element : 0.023"  # scripted group (container) (typed FeaturePython)
  n = 0.023
FEATURE [App::DocumentObjectGroupPython] O_element057  label="O_element : 0.779"  # scripted group (container) (typed FeaturePython)
  n = 0.779
FEATURE [App::DocumentObjectGroupPython] Na_element010  label="Na_element : 0.097"  # scripted group (container) (typed FeaturePython)
  n = 0.002
FEATURE [App::DocumentObjectGroupPython] P_element006  label="P_element : 0.105"  # scripted group (container) (typed FeaturePython)
  n = 0.001
FEATURE [App::DocumentObjectGroupPython] S_element016  label="S_element : 0.017"  # scripted group (container) (typed FeaturePython)
  n = 0.002
FEATURE [App::DocumentObjectGroupPython] Cl_element014  label="Cl_element : 0.587"  # scripted group (container) (typed FeaturePython)
  n = 0.003
FEATURE [App::DocumentObjectGroupPython] K_element005  label="K_element : 0.015"  # scripted group (container) (typed FeaturePython)
  n = 0.002
FEATURE [App::DocumentObjectGroupPython] G4_LUNG_ICRP  # scripted group (container) (typed FeaturePython)
  Dunit = g/cm3
  Dvalue = 1.04
  Group = -> [H_element051,C_element056,N_element023,O_element057,Na_element010,P_element006,S_element016,Cl_element014,K_element005]
  conduct = 2
  density = 1
  expand = 3
  formula = G4_LUNG_ICRP
  name = G4_LUNG_ICRP
  specific = 4
FEATURE [App::DocumentObjectGroupPython] H_element052  label="H_element : 0.116"  # scripted group (container) (typed FeaturePython)
  n = 0.114318
FEATURE [App::DocumentObjectGroupPython] C_element057  label="C_element : 0.656"  # scripted group (container) (typed FeaturePython)
  n = 0.655824
FEATURE [App::DocumentObjectGroupPython] O_element058  label="O_element : 0.092"  # scripted group (container) (typed FeaturePython)
  n = 0.0921831
FEATURE [App::DocumentObjectGroupPython] Mg_element004  label="Mg_element : 0.135"  # scripted group (container) (typed FeaturePython)
  n = 0.134792
FEATURE [App::DocumentObjectGroupPython] Ca_element013  label="Ca_element : 0.003"  # scripted group (container) (typed FeaturePython)
  n = 0.002883
FEATURE [App::DocumentObjectGroupPython] G4_M3_WAX  # scripted group (container) (typed FeaturePython)
  Dunit = g/cm3
  Dvalue = 1.05
  Group = -> [H_element052,C_element057,O_element058,Mg_element004,Ca_element013]
  conduct = 2
  density = 1
  expand = 3
  formula = G4_M3_WAX
  name = G4_M3_WAX
  specific = 4
FEATURE [App::DocumentObjectGroupPython] Mg_element005  label="Mg_element : 1"  # scripted group (container) (typed FeaturePython)
  n = 1
  ref = Mg_element
FEATURE [App::DocumentObjectGroupPython] C_element058  label="C_element : 031"  # scripted group (container) (typed FeaturePython)
  n = 1
  ref = C_element
FEATURE [App::DocumentObjectGroupPython] O_element059  label="O_element : 030"  # scripted group (container) (typed FeaturePython)
  n = 3
  ref = O_element
FEATURE [App::DocumentObjectGroupPython] G4_MAGNESIUM_CARBONATE  # scripted group (container) (typed FeaturePython)
  Dunit = g/cm3
  Dvalue = 2.958
  Group = -> [Mg_element005,C_element058,O_element059]
  conduct = 2
  density = 1
  expand = 3
  formula = G4_MAGNESIUM_CARBONATE
  name = G4_MAGNESIUM_CARBONATE
  specific = 4
FEATURE [App::DocumentObjectGroupPython] Mg_element006  label="Mg_element : 002"  # scripted group (container) (typed FeaturePython)
  n = 1
  ref = Mg_element
FEATURE [App::DocumentObjectGroupPython] F_element013  label="F_element : 005"  # scripted group (container) (typed FeaturePython)
  n = 2
  ref = F_element
FEATURE [App::DocumentObjectGroupPython] G4_MAGNESIUM_FLUORIDE  # scripted group (container) (typed FeaturePython)
  Dunit = g/cm3
  Dvalue = 3
  Group = -> [Mg_element006,F_element013]
  conduct = 2
  density = 1
  expand = 3
  formula = G4_MAGNESIUM_FLUORIDE
  name = G4_MAGNESIUM_FLUORIDE
  specific = 4
FEATURE [App::DocumentObjectGroupPython] Mg_element007  label="Mg_element : 003"  # scripted group (container) (typed FeaturePython)
  n = 1
  ref = Mg_element
FEATURE [App::DocumentObjectGroupPython] O_element060  label="O_element : 031"  # scripted group (container) (typed FeaturePython)
  n = 1
  ref = O_element
FEATURE [App::DocumentObjectGroupPython] G4_MAGNESIUM_OXIDE  # scripted group (container) (typed FeaturePython)
  Dunit = g/cm3
  Dvalue = 3.58
  Group = -> [Mg_element007,O_element060]
  conduct = 2
  density = 1
  expand = 3
  formula = G4_MAGNESIUM_OXIDE
  name = G4_MAGNESIUM_OXIDE
  specific = 4
FEATURE [App::DocumentObjectGroupPython] Mg_element008  label="Mg_element : 004"  # scripted group (container) (typed FeaturePython)
  n = 1
  ref = Mg_element
FEATURE [App::DocumentObjectGroupPython] B_element006  label="B_element : 006"  # scripted group (container) (typed FeaturePython)
  n = 4
  ref = B_element
FEATURE [App::DocumentObjectGroupPython] O_element061  label="O_element : 032"  # scripted group (container) (typed FeaturePython)
  n = 7
  ref = O_element
FEATURE [App::DocumentObjectGroupPython] G4_MAGNESIUM_TETRABORATE  # scripted group (container) (typed FeaturePython)
  Dunit = g/cm3
  Dvalue = 2.53
  Group = -> [Mg_element008,B_element006,O_element061]
  conduct = 2
  density = 1
  expand = 3
  formula = G4_MAGNESIUM_TETRABORATE
  name = G4_MAGNESIUM_TETRABORATE
  specific = 4
FEATURE [App::DocumentObjectGroupPython] Hg_element001  label="Hg_element : 1"  # scripted group (container) (typed FeaturePython)
  n = 1
  ref = Hg_element
FEATURE [App::DocumentObjectGroupPython] I_element004  label="I_element : 2"  # scripted group (container) (typed FeaturePython)
  n = 2
  ref = I_element
FEATURE [App::DocumentObjectGroupPython] G4_MERCURIC_IODIDE  # scripted group (container) (typed FeaturePython)
  Dunit = g/cm3
  Dvalue = 6.36
  Group = -> [Hg_element001,I_element004]
  conduct = 2
  density = 1
  expand = 3
  formula = G4_MERCURIC_IODIDE
  name = G4_MERCURIC_IODIDE
  specific = 4
FEATURE [App::DocumentObjectGroupPython] C_element059  label="C_element : 032"  # scripted group (container) (typed FeaturePython)
  n = 1
  ref = C_element
FEATURE [App::DocumentObjectGroupPython] H_element053  label="H_element : 028"  # scripted group (container) (typed FeaturePython)
  n = 4
  ref = H_element
FEATURE [App::DocumentObjectGroupPython] G4_METHANE  # scripted group (container) (typed FeaturePython)
  Dunit = g/cm3
  Dvalue = 0.000667151
  Group = -> [C_element059,H_element053]
  conduct = 2
  density = 1
  expand = 3
  formula = G4_METHANE
  name = G4_METHANE
  specific = 4
FEATURE [App::DocumentObjectGroupPython] C_element060  label="C_element : 033"  # scripted group (container) (typed FeaturePython)
  n = 1
  ref = C_element
FEATURE [App::DocumentObjectGroupPython] H_element054  label="H_element : 029"  # scripted group (container) (typed FeaturePython)
  n = 4
  ref = H_element
FEATURE [App::DocumentObjectGroupPython] O_element062  label="O_element : 033"  # scripted group (container) (typed FeaturePython)
  n = 1
  ref = O_element
FEATURE [App::DocumentObjectGroupPython] G4_METHANOL  # scripted group (container) (typed FeaturePython)
  Dunit = g/cm3
  Dvalue = 0.7914
  Group = -> [C_element060,H_element054,O_element062]
  conduct = 2
  density = 1
  expand = 3
  formula = G4_METHANOL
  name = G4_METHANOL
  specific = 4
FEATURE [App::DocumentObjectGroupPython] H_element055  label="H_element : 0.134"  # scripted group (container) (typed FeaturePython)
  n = 0.13404
FEATURE [App::DocumentObjectGroupPython] C_element061  label="C_element : 0.778"  # scripted group (container) (typed FeaturePython)
  n = 0.77796
FEATURE [App::DocumentObjectGroupPython] O_element063  label="O_element : 0.035"  # scripted group (container) (typed FeaturePython)
  n = 0.03502
FEATURE [App::DocumentObjectGroupPython] Mg_element009  label="Mg_element : 0.039"  # scripted group (container) (typed FeaturePython)
  n = 0.038594
FEATURE [App::DocumentObjectGroupPython] Ti_element002  label="Ti_element : 0.014"  # scripted group (container) (typed FeaturePython)
  n = 0.014386
FEATURE [App::DocumentObjectGroupPython] G4_MIX_D_WAX  # scripted group (container) (typed FeaturePython)
  Dunit = g/cm3
  Dvalue = 0.99
  Group = -> [H_element055,C_element061,O_element063,Mg_element009,Ti_element002]
  conduct = 2
  density = 1
  expand = 3
  formula = G4_MIX_D_WAX
  name = G4_MIX_D_WAX
  specific = 4
FEATURE [App::DocumentObjectGroupPython] H_element056  label="H_element : 0.135"  # scripted group (container) (typed FeaturePython)
  n = 0.081192
FEATURE [App::DocumentObjectGroupPython] C_element062  label="C_element : 0.583"  # scripted group (container) (typed FeaturePython)
  n = 0.583442
FEATURE [App::DocumentObjectGroupPython] N_element024  label="N_element : 0.018"  # scripted group (container) (typed FeaturePython)
  n = 0.017798
FEATURE [App::DocumentObjectGroupPython] O_element064  label="O_element : 0.186"  # scripted group (container) (typed FeaturePython)
  n = 0.186381
FEATURE [App::DocumentObjectGroupPython] Mg_element010  label="Mg_element : 0.130"  # scripted group (container) (typed FeaturePython)
  n = 0.130287
FEATURE [App::DocumentObjectGroupPython] Cl_element015  label="Cl_element : 0.588"  # scripted group (container) (typed FeaturePython)
  n = 0.0009
FEATURE [App::DocumentObjectGroupPython] G4_MS20_TISSUE  # scripted group (container) (typed FeaturePython)
  Dunit = g/cm3
  Dvalue = 1
  Group = -> [H_element056,C_element062,N_element024,O_element064,Mg_element010,Cl_element015]
  conduct = 2
  density = 1
  expand = 3
  formula = G4_MS20_TISSUE
  name = G4_MS20_TISSUE
  specific = 4
FEATURE [App::DocumentObjectGroupPython] H_element057  label="H_element : 0.136"  # scripted group (container) (typed FeaturePython)
  n = 0.102
FEATURE [App::DocumentObjectGroupPython] C_element063  label="C_element : 0.143"  # scripted group (container) (typed FeaturePython)
  n = 0.143
FEATURE [App::DocumentObjectGroupPython] N_element025  label="N_element : 0.034"  # scripted group (container) (typed FeaturePython)
  n = 0.034
FEATURE [App::DocumentObjectGroupPython] O_element065  label="O_element : 0.710"  # scripted group (container) (typed FeaturePython)
  n = 0.71
FEATURE [App::DocumentObjectGroupPython] Na_element011  label="Na_element : 0.098"  # scripted group (container) (typed FeaturePython)
  n = 0.001
FEATURE [App::DocumentObjectGroupPython] P_element007  label="P_element : 0.002"  # scripted group (container) (typed FeaturePython)
  n = 0.002
FEATURE [App::DocumentObjectGroupPython] S_element017  label="S_element : 0.018"  # scripted group (container) (typed FeaturePython)
  n = 0.003
FEATURE [App::DocumentObjectGroupPython] Cl_element016  label="Cl_element : 0.589"  # scripted group (container) (typed FeaturePython)
  n = 0.001
FEATURE [App::DocumentObjectGroupPython] K_element006  label="K_element : 0.004"  # scripted group (container) (typed FeaturePython)
  n = 0.004
FEATURE [App::DocumentObjectGroupPython] G4_MUSCLE_SKELETAL_ICRP  # scripted group (container) (typed FeaturePython)
  Dunit = g/cm3
  Dvalue = 1.05
  Group = -> [H_element057,C_element063,N_element025,O_element065,Na_element011,P_element007,S_element017,Cl_element016,K_element006]
  conduct = 2
  density = 1
  expand = 3
  formula = G4_MUSCLE_SKELETAL_ICRP
  name = G4_MUSCLE_SKELETAL_ICRP
  specific = 4
FEATURE [App::DocumentObjectGroupPython] H_element058  label="H_element : 0.137"  # scripted group (container) (typed FeaturePython)
  n = 0.102102
FEATURE [App::DocumentObjectGroupPython] C_element064  label="C_element : 0.123"  # scripted group (container) (typed FeaturePython)
  n = 0.123123
FEATURE [App::DocumentObjectGroupPython] N_element026  label="N_element : 0.756"  # scripted group (container) (typed FeaturePython)
  n = 0.035035
FEATURE [App::DocumentObjectGroupPython] O_element066  label="O_element : 0.730"  # scripted group (container) (typed FeaturePython)
  n = 0.72973
FEATURE [App::DocumentObjectGroupPython] Na_element012  label="Na_element : 0.099"  # scripted group (container) (typed FeaturePython)
  n = 0.001001
FEATURE [App::DocumentObjectGroupPython] P_element008  label="P_element : 0.106"  # scripted group (container) (typed FeaturePython)
  n = 0.002002
FEATURE [App::DocumentObjectGroupPython] S_element018  label="S_element : 0.019"  # scripted group (container) (typed FeaturePython)
  n = 0.004004
FEATURE [App::DocumentObjectGroupPython] K_element007  label="K_element : 0.016"  # scripted group (container) (typed FeaturePython)
  n = 0.003003
FEATURE [App::DocumentObjectGroupPython] G4_MUSCLE_STRIATED_ICRU  # scripted group (container) (typed FeaturePython)
  Dunit = g/cm3
  Dvalue = 1.04
  Group = -> [H_element058,C_element064,N_element026,O_element066,Na_element012,P_element008,S_element018,K_element007]
  conduct = 2
  density = 1
  expand = 3
  formula = G4_MUSCLE_STRIATED_ICRU
  name = G4_MUSCLE_STRIATED_ICRU
  specific = 4
FEATURE [App::DocumentObjectGroupPython] H_element059  label="H_element : 0.098"  # scripted group (container) (typed FeaturePython)
  n = 0.0982341
FEATURE [App::DocumentObjectGroupPython] C_element065  label="C_element : 0.156"  # scripted group (container) (typed FeaturePython)
  n = 0.156214
FEATURE [App::DocumentObjectGroupPython] N_element027  label="N_element : 0.757"  # scripted group (container) (typed FeaturePython)
  n = 0.035451
FEATURE [App::DocumentObjectGroupPython] O_element067  label="O_element : 0.880"  # scripted group (container) (typed FeaturePython)
  n = 0.710101
FEATURE [App::DocumentObjectGroupPython] G4_MUSCLE_WITH_SUCROSE  # scripted group (container) (typed FeaturePython)
  Dunit = g/cm3
  Dvalue = 1.11
  Group = -> [H_element059,C_element065,N_element027,O_element067]
  conduct = 2
  density = 1
  expand = 3
  formula = G4_MUSCLE_WITH_SUCROSE
  name = G4_MUSCLE_WITH_SUCROSE
  specific = 4
FEATURE [App::DocumentObjectGroupPython] H_element060  label="H_element : 0.138"  # scripted group (container) (typed FeaturePython)
  n = 0.101969
FEATURE [App::DocumentObjectGroupPython] C_element066  label="C_element : 0.120"  # scripted group (container) (typed FeaturePython)
  n = 0.120058
FEATURE [App::DocumentObjectGroupPython] N_element028  label="N_element : 0.758"  # scripted group (container) (typed FeaturePython)
  n = 0.035451
FEATURE [App::DocumentObjectGroupPython] O_element068  label="O_element : 0.743"  # scripted group (container) (typed FeaturePython)
  n = 0.742522
FEATURE [App::DocumentObjectGroupPython] G4_MUSCLE_WITHOUT_SUCROSE  # scripted group (container) (typed FeaturePython)
  Dunit = g/cm3
  Dvalue = 1.07
  Group = -> [H_element060,C_element066,N_element028,O_element068]
  conduct = 2
  density = 1
  expand = 3
  formula = G4_MUSCLE_WITHOUT_SUCROSE
  name = G4_MUSCLE_WITHOUT_SUCROSE
  specific = 4
FEATURE [App::DocumentObjectGroupPython] C_element067  label="C_element : 10"  # scripted group (container) (typed FeaturePython)
  n = 10
  ref = C_element
FEATURE [App::DocumentObjectGroupPython] H_element061  label="H_element : 030"  # scripted group (container) (typed FeaturePython)
  n = 8
  ref = H_element
FEATURE [App::DocumentObjectGroupPython] G4_NAPHTHALENE  # scripted group (container) (typed FeaturePython)
  Dunit = g/cm3
  Dvalue = 1.145
  Group = -> [C_element067,H_element061]
  conduct = 2
  density = 1
  expand = 3
  formula = G4_NAPHTHALENE
  name = G4_NAPHTHALENE
  specific = 4
FEATURE [App::DocumentObjectGroupPython] C_element068  label="C_element : 034"  # scripted group (container) (typed FeaturePython)
  n = 6
  ref = C_element
FEATURE [App::DocumentObjectGroupPython] H_element062  label="H_element : 031"  # scripted group (container) (typed FeaturePython)
  n = 5
  ref = H_element
FEATURE [App::DocumentObjectGroupPython] N_element029  label="N_element : 012"  # scripted group (container) (typed FeaturePython)
  n = 1
  ref = N_element
FEATURE [App::DocumentObjectGroupPython] O_element069  label="O_element : 034"  # scripted group (container) (typed FeaturePython)
  n = 2
  ref = O_element
FEATURE [App::DocumentObjectGroupPython] G4_NITROBENZENE  # scripted group (container) (typed FeaturePython)
  Dunit = g/cm3
  Dvalue = 1.19867
  Group = -> [C_element068,H_element062,N_element029,O_element069]
  conduct = 2
  density = 1
  expand = 3
  formula = G4_NITROBENZENE
  name = G4_NITROBENZENE
  specific = 4
FEATURE [App::DocumentObjectGroupPython] N_element030  label="N_element : 013"  # scripted group (container) (typed FeaturePython)
  n = 2
  ref = N_element
FEATURE [App::DocumentObjectGroupPython] O_element070  label="O_element : 035"  # scripted group (container) (typed FeaturePython)
  n = 1
  ref = O_element
FEATURE [App::DocumentObjectGroupPython] G4_NITROUS_OXIDE  # scripted group (container) (typed FeaturePython)
  Dunit = g/cm3
  Dvalue = 0.00183094
  Group = -> [N_element030,O_element070]
  conduct = 2
  density = 1
  expand = 3
  formula = G4_NITROUS_OXIDE
  name = G4_NITROUS_OXIDE
  specific = 4
FEATURE [App::DocumentObjectGroupPython] H_element063  label="H_element : 0.104"  # scripted group (container) (typed FeaturePython)
  n = 0.103509
FEATURE [App::DocumentObjectGroupPython] C_element069  label="C_element : 0.648"  # scripted group (container) (typed FeaturePython)
  n = 0.648416
FEATURE [App::DocumentObjectGroupPython] N_element031  label="N_element : 0.100"  # scripted group (container) (typed FeaturePython)
  n = 0.0995361
FEATURE [App::DocumentObjectGroupPython] O_element071  label="O_element : 0.149"  # scripted group (container) (typed FeaturePython)
  n = 0.148539
FEATURE [App::DocumentObjectGroupPython] G4_NYLON_8062  label="G4_NYLON-8062"  # scripted group (container) (typed FeaturePython)
  Dunit = g/cm3
  Dvalue = 1.08
  Group = -> [H_element063,C_element069,N_element031,O_element071]
  conduct = 2
  density = 1
  expand = 3
  formula = G4_NYLON-8062
  name = G4_NYLON-8062
  specific = 4
FEATURE [App::DocumentObjectGroupPython] C_element070  label="C_element : 035"  # scripted group (container) (typed FeaturePython)
  n = 6
  ref = C_element
FEATURE [App::DocumentObjectGroupPython] H_element064  label="H_element : 11"  # scripted group (container) (typed FeaturePython)
  n = 11
  ref = H_element
FEATURE [App::DocumentObjectGroupPython] N_element032  label="N_element : 014"  # scripted group (container) (typed FeaturePython)
  n = 1
  ref = N_element
FEATURE [App::DocumentObjectGroupPython] O_element072  label="O_element : 036"  # scripted group (container) (typed FeaturePython)
  n = 1
  ref = O_element
FEATURE [App::DocumentObjectGroupPython] G4_NYLON_6_6  label="G4_NYLON-6-6"  # scripted group (container) (typed FeaturePython)
  Dunit = g/cm3
  Dvalue = 1.14
  Group = -> [C_element070,H_element064,N_element032,O_element072]
  conduct = 2
  density = 1
  expand = 3
  formula = G4_NYLON-6-6
  name = G4_NYLON-6-6
  specific = 4
FEATURE [App::DocumentObjectGroupPython] H_element065  label="H_element : 0.139"  # scripted group (container) (typed FeaturePython)
  n = 0.107062
FEATURE [App::DocumentObjectGroupPython] C_element071  label="C_element : 0.680"  # scripted group (container) (typed FeaturePython)
  n = 0.680449
FEATURE [App::DocumentObjectGroupPython] N_element033  label="N_element : 0.099"  # scripted group (container) (typed FeaturePython)
  n = 0.099189
FEATURE [App::DocumentObjectGroupPython] O_element073  label="O_element : 0.113"  # scripted group (container) (typed FeaturePython)
  n = 0.1133
FEATURE [App::DocumentObjectGroupPython] G4_NYLON_6_10  label="G4_NYLON-6-10"  # scripted group (container) (typed FeaturePython)
  Dunit = g/cm3
  Dvalue = 1.14
  Group = -> [H_element065,C_element071,N_element033,O_element073]
  conduct = 2
  density = 1
  expand = 3
  formula = G4_NYLON-6-10
  name = G4_NYLON-6-10
  specific = 4
FEATURE [App::DocumentObjectGroupPython] H_element066  label="H_element : 0.140"  # scripted group (container) (typed FeaturePython)
  n = 0.115476
FEATURE [App::DocumentObjectGroupPython] C_element072  label="C_element : 0.721"  # scripted group (container) (typed FeaturePython)
  n = 0.720818
FEATURE [App::DocumentObjectGroupPython] N_element034  label="N_element : 0.076"  # scripted group (container) (typed FeaturePython)
  n = 0.0764169
FEATURE [App::DocumentObjectGroupPython] O_element074  label="O_element : 0.087"  # scripted group (container) (typed FeaturePython)
  n = 0.0872889
FEATURE [App::DocumentObjectGroupPython] G4_NYLON_11_RILSAN  label="G4_NYLON-11_RILSAN"  # scripted group (container) (typed FeaturePython)
  Dunit = g/cm3
  Dvalue = 1.425
  Group = -> [H_element066,C_element072,N_element034,O_element074]
  conduct = 2
  density = 1
  expand = 3
  formula = G4_NYLON-11_RILSAN
  name = G4_NYLON-11_RILSAN
  specific = 4
FEATURE [App::DocumentObjectGroupPython] C_element073  label="C_element : 8"  # scripted group (container) (typed FeaturePython)
  n = 8
  ref = C_element
FEATURE [App::DocumentObjectGroupPython] H_element067  label="H_element : 18"  # scripted group (container) (typed FeaturePython)
  n = 18
  ref = H_element
FEATURE [App::DocumentObjectGroupPython] G4_OCTANE  # scripted group (container) (typed FeaturePython)
  Dunit = g/cm3
  Dvalue = 0.7026
  Group = -> [C_element073,H_element067]
  conduct = 2
  density = 1
  expand = 3
  formula = G4_OCTANE
  name = G4_OCTANE
  specific = 4
FEATURE [App::DocumentObjectGroupPython] C_element074  label="C_element : 25"  # scripted group (container) (typed FeaturePython)
  n = 25
  ref = C_element
FEATURE [App::DocumentObjectGroupPython] H_element068  label="H_element : 52"  # scripted group (container) (typed FeaturePython)
  n = 52
  ref = H_element
FEATURE [App::DocumentObjectGroupPython] G4_PARAFFIN  # scripted group (container) (typed FeaturePython)
  Dunit = g/cm3
  Dvalue = 0.93
  Group = -> [C_element074,H_element068]
  conduct = 2
  density = 1
  expand = 3
  formula = G4_PARAFFIN
  name = G4_PARAFFIN
  specific = 4
FEATURE [App::DocumentObjectGroupPython] C_element075  label="C_element : 036"  # scripted group (container) (typed FeaturePython)
  n = 5
  ref = C_element
FEATURE [App::DocumentObjectGroupPython] H_element069  label="H_element : 032"  # scripted group (container) (typed FeaturePython)
  n = 12
  ref = H_element
FEATURE [App::DocumentObjectGroupPython] G4_N_PENTANE  label="G4_N-PENTANE"  # scripted group (container) (typed FeaturePython)
  Dunit = g/cm3
  Dvalue = 0.6262
  Group = -> [C_element075,H_element069]
  conduct = 2
  density = 1
  expand = 3
  formula = G4_N-PENTANE
  name = G4_N-PENTANE
  specific = 4
FEATURE [App::DocumentObjectGroupPython] H_element070  label="H_element : 0.014"  # scripted group (container) (typed FeaturePython)
  n = 0.0141
FEATURE [App::DocumentObjectGroupPython] C_element076  label="C_element : 0.072"  # scripted group (container) (typed FeaturePython)
  n = 0.072261
FEATURE [App::DocumentObjectGroupPython] N_element035  label="N_element : 0.019"  # scripted group (container) (typed FeaturePython)
  n = 0.01932
FEATURE [App::DocumentObjectGroupPython] O_element075  label="O_element : 0.066"  # scripted group (container) (typed FeaturePython)
  n = 0.066101
FEATURE [App::DocumentObjectGroupPython] S_element019  label="S_element : 0.020"  # scripted group (container) (typed FeaturePython)
  n = 0.00189
FEATURE [App::DocumentObjectGroupPython] Br_element004  label="Br_element : 0.349"  # scripted group (container) (typed FeaturePython)
  n = 0.349103
FEATURE [App::DocumentObjectGroupPython] Ag_element001  label="Ag_element : 0.474"  # scripted group (container) (typed FeaturePython)
  n = 0.474105
FEATURE [App::DocumentObjectGroupPython] I_element005  label="I_element : 0.003"  # scripted group (container) (typed FeaturePython)
  n = 0.00312
FEATURE [App::DocumentObjectGroupPython] G4_PHOTO_EMULSION  # scripted group (container) (typed FeaturePython)
  Dunit = g/cm3
  Dvalue = 3.815
  Group = -> [H_element070,C_element076,N_element035,O_element075,S_element019,Br_element004,Ag_element001,I_element005]
  conduct = 2
  density = 1
  expand = 3
  formula = G4_PHOTO_EMULSION
  name = G4_PHOTO_EMULSION
  specific = 4
FEATURE [App::DocumentObjectGroupPython] C_element077  label="C_element : 9"  # scripted group (container) (typed FeaturePython)
  n = 9
  ref = C_element
FEATURE [App::DocumentObjectGroupPython] H_element071  label="H_element : 033"  # scripted group (container) (typed FeaturePython)
  n = 10
  ref = H_element
FEATURE [App::DocumentObjectGroupPython] G4_PLASTIC_SC_VINYLTOLUENE  # scripted group (container) (typed FeaturePython)
  Dunit = g/cm3
  Dvalue = 1.032
  Group = -> [C_element077,H_element071]
  conduct = 2
  density = 1
  expand = 3
  formula = G4_PLASTIC_SC_VINYLTOLUENE
  name = G4_PLASTIC_SC_VINYLTOLUENE
  specific = 4
FEATURE [App::DocumentObjectGroupPython] Pu_element001  label="Pu_element : 1"  # scripted group (container) (typed FeaturePython)
  n = 1
  ref = Pu_element
FEATURE [App::DocumentObjectGroupPython] O_element076  label="O_element : 037"  # scripted group (container) (typed FeaturePython)
  n = 2
  ref = O_element
FEATURE [App::DocumentObjectGroupPython] G4_PLUTONIUM_DIOXIDE  # scripted group (container) (typed FeaturePython)
  Dunit = g/cm3
  Dvalue = 11.46
  Group = -> [Pu_element001,O_element076]
  conduct = 2
  density = 1
  expand = 3
  formula = G4_PLUTONIUM_DIOXIDE
  name = G4_PLUTONIUM_DIOXIDE
  specific = 4
FEATURE [App::DocumentObjectGroupPython] C_element078  label="C_element : 037"  # scripted group (container) (typed FeaturePython)
  n = 3
  ref = C_element
FEATURE [App::DocumentObjectGroupPython] H_element072  label="H_element : 034"  # scripted group (container) (typed FeaturePython)
  n = 3
  ref = H_element
FEATURE [App::DocumentObjectGroupPython] N_element036  label="N_element : 015"  # scripted group (container) (typed FeaturePython)
  n = 1
  ref = N_element
FEATURE [App::DocumentObjectGroupPython] G4_POLYACRYLONITRILE  # scripted group (container) (typed FeaturePython)
  Dunit = g/cm3
  Dvalue = 1.17
  Group = -> [C_element078,H_element072,N_element036]
  conduct = 2
  density = 1
  expand = 3
  formula = G4_POLYACRYLONITRILE
  name = G4_POLYACRYLONITRILE
  specific = 4
FEATURE [App::DocumentObjectGroupPython] C_element079  label="C_element : 16"  # scripted group (container) (typed FeaturePython)
  n = 16
  ref = C_element
FEATURE [App::DocumentObjectGroupPython] H_element073  label="H_element : 035"  # scripted group (container) (typed FeaturePython)
  n = 14
  ref = H_element
FEATURE [App::DocumentObjectGroupPython] O_element077  label="O_element : 038"  # scripted group (container) (typed FeaturePython)
  n = 3
  ref = O_element
FEATURE [App::DocumentObjectGroupPython] G4_POLYCARBONATE  # scripted group (container) (typed FeaturePython)
  Dunit = g/cm3
  Dvalue = 1.2
  Group = -> [C_element079,H_element073,O_element077]
  conduct = 2
  density = 1
  expand = 3
  formula = G4_POLYCARBONATE
  name = G4_POLYCARBONATE
  specific = 4
FEATURE [App::DocumentObjectGroupPython] C_element080  label="C_element : 038"  # scripted group (container) (typed FeaturePython)
  n = 8
  ref = C_element
FEATURE [App::DocumentObjectGroupPython] H_element074  label="H_element : 036"  # scripted group (container) (typed FeaturePython)
  n = 7
  ref = H_element
FEATURE [App::DocumentObjectGroupPython] Cl_element017  label="Cl_element : 007"  # scripted group (container) (typed FeaturePython)
  n = 1
  ref = Cl_element
FEATURE [App::DocumentObjectGroupPython] G4_POLYCHLOROSTYRENE  # scripted group (container) (typed FeaturePython)
  Dunit = g/cm3
  Dvalue = 1.3
  Group = -> [C_element080,H_element074,Cl_element017]
  conduct = 2
  density = 1
  expand = 3
  formula = G4_POLYCHLOROSTYRENE
  name = G4_POLYCHLOROSTYRENE
  specific = 4
FEATURE [App::DocumentObjectGroupPython] C_element081  label="C_element : 039"  # scripted group (container) (typed FeaturePython)
  n = 1
  ref = C_element
FEATURE [App::DocumentObjectGroupPython] H_element075  label="H_element : 037"  # scripted group (container) (typed FeaturePython)
  n = 2
  ref = H_element
FEATURE [App::DocumentObjectGroupPython] G4_POLYETHYLENE  # scripted group (container) (typed FeaturePython)
  Dunit = g/cm3
  Dvalue = 0.94
  Group = -> [C_element081,H_element075]
  conduct = 2
  density = 1
  expand = 3
  formula = G4_POLYETHYLENE
  name = G4_POLYETHYLENE
  specific = 4
FEATURE [App::DocumentObjectGroupPython] C_element082  label="C_element : 040"  # scripted group (container) (typed FeaturePython)
  n = 10
  ref = C_element
FEATURE [App::DocumentObjectGroupPython] H_element076  label="H_element : 038"  # scripted group (container) (typed FeaturePython)
  n = 8
  ref = H_element
FEATURE [App::DocumentObjectGroupPython] O_element078  label="O_element : 039"  # scripted group (container) (typed FeaturePython)
  n = 4
  ref = O_element
FEATURE [App::DocumentObjectGroupPython] G4_MYLAR  # scripted group (container) (typed FeaturePython)
  Dunit = g/cm3
  Dvalue = 1.4
  Group = -> [C_element082,H_element076,O_element078]
  conduct = 2
  density = 1
  expand = 3
  formula = G4_MYLAR
  name = G4_MYLAR
  specific = 4
FEATURE [App::DocumentObjectGroupPython] C_element083  label="C_element : 041"  # scripted group (container) (typed FeaturePython)
  n = 5
  ref = C_element
FEATURE [App::DocumentObjectGroupPython] H_element077  label="H_element : 039"  # scripted group (container) (typed FeaturePython)
  n = 8
  ref = H_element
FEATURE [App::DocumentObjectGroupPython] O_element079  label="O_element : 040"  # scripted group (container) (typed FeaturePython)
  n = 2
  ref = O_element
FEATURE [App::DocumentObjectGroupPython] G4_PLEXIGLASS  # scripted group (container) (typed FeaturePython)
  Dunit = g/cm3
  Dvalue = 1.19
  Group = -> [C_element083,H_element077,O_element079]
  conduct = 2
  density = 1
  expand = 3
  formula = G4_PLEXIGLASS
  name = G4_PLEXIGLASS
  specific = 4
FEATURE [App::DocumentObjectGroupPython] C_element084  label="C_element : 042"  # scripted group (container) (typed FeaturePython)
  n = 1
  ref = C_element
FEATURE [App::DocumentObjectGroupPython] H_element078  label="H_element : 040"  # scripted group (container) (typed FeaturePython)
  n = 2
  ref = H_element
FEATURE [App::DocumentObjectGroupPython] O_element080  label="O_element : 041"  # scripted group (container) (typed FeaturePython)
  n = 1
  ref = O_element
FEATURE [App::DocumentObjectGroupPython] G4_POLYOXYMETHYLENE  # scripted group (container) (typed FeaturePython)
  Dunit = g/cm3
  Dvalue = 1.425
  Group = -> [C_element084,H_element078,O_element080]
  conduct = 2
  density = 1
  expand = 3
  formula = G4_POLYOXYMETHYLENE
  name = G4_POLYOXYMETHYLENE
  specific = 4
FEATURE [App::DocumentObjectGroupPython] C_element085  label="C_element : 043"  # scripted group (container) (typed FeaturePython)
  n = 2
  ref = C_element
FEATURE [App::DocumentObjectGroupPython] H_element079  label="H_element : 041"  # scripted group (container) (typed FeaturePython)
  n = 4
  ref = H_element
FEATURE [App::DocumentObjectGroupPython] G4_POLYPROPYLENE  # scripted group (container) (typed FeaturePython)
  Dunit = g/cm3
  Dvalue = 0.9
  Group = -> [C_element085,H_element079]
  conduct = 2
  density = 1
  expand = 3
  formula = G4_POLYPROPYLENE
  name = G4_POLYPROPYLENE
  specific = 4
FEATURE [App::DocumentObjectGroupPython] C_element086  label="C_element : 044"  # scripted group (container) (typed FeaturePython)
  n = 8
  ref = C_element
FEATURE [App::DocumentObjectGroupPython] H_element080  label="H_element : 042"  # scripted group (container) (typed FeaturePython)
  n = 8
  ref = H_element
FEATURE [App::DocumentObjectGroupPython] G4_POLYSTYRENE  # scripted group (container) (typed FeaturePython)
  Dunit = g/cm3
  Dvalue = 1.06
  Group = -> [C_element086,H_element080]
  conduct = 2
  density = 1
  expand = 3
  formula = G4_POLYSTYRENE
  name = G4_POLYSTYRENE
  specific = 4
FEATURE [App::DocumentObjectGroupPython] C_element087  label="C_element : 045"  # scripted group (container) (typed FeaturePython)
  n = 2
  ref = C_element
FEATURE [App::DocumentObjectGroupPython] F_element014  label="F_element : 4"  # scripted group (container) (typed FeaturePython)
  n = 4
  ref = F_element
FEATURE [App::DocumentObjectGroupPython] G4_TEFLON  # scripted group (container) (typed FeaturePython)
  Dunit = g/cm3
  Dvalue = 2.2
  Group = -> [C_element087,F_element014]
  conduct = 2
  density = 1
  expand = 3
  formula = G4_TEFLON
  name = G4_TEFLON
  specific = 4
FEATURE [App::DocumentObjectGroupPython] C_element088  label="C_element : 046"  # scripted group (container) (typed FeaturePython)
  n = 2
  ref = C_element
FEATURE [App::DocumentObjectGroupPython] F_element015  label="F_element : 006"  # scripted group (container) (typed FeaturePython)
  n = 3
  ref = F_element
FEATURE [App::DocumentObjectGroupPython] Cl_element018  label="Cl_element : 008"  # scripted group (container) (typed FeaturePython)
  n = 1
  ref = Cl_element
FEATURE [App::DocumentObjectGroupPython] G4_POLYTRIFLUOROCHLOROETHYLENE  # scripted group (container) (typed FeaturePython)
  Dunit = g/cm3
  Dvalue = 2.1
  Group = -> [C_element088,F_element015,Cl_element018]
  conduct = 2
  density = 1
  expand = 3
  formula = G4_POLYTRIFLUOROCHLOROETHYLENE
  name = G4_POLYTRIFLUOROCHLOROETHYLENE
  specific = 4
FEATURE [App::DocumentObjectGroupPython] C_element089  label="C_element : 047"  # scripted group (container) (typed FeaturePython)
  n = 4
  ref = C_element
FEATURE [App::DocumentObjectGroupPython] H_element081  label="H_element : 043"  # scripted group (container) (typed FeaturePython)
  n = 6
  ref = H_element
FEATURE [App::DocumentObjectGroupPython] O_element081  label="O_element : 042"  # scripted group (container) (typed FeaturePython)
  n = 2
  ref = O_element
FEATURE [App::DocumentObjectGroupPython] G4_POLYVINYL_ACETATE  # scripted group (container) (typed FeaturePython)
  Dunit = g/cm3
  Dvalue = 1.19
  Group = -> [C_element089,H_element081,O_element081]
  conduct = 2
  density = 1
  expand = 3
  formula = G4_POLYVINYL_ACETATE
  name = G4_POLYVINYL_ACETATE
  specific = 4
FEATURE [App::DocumentObjectGroupPython] C_element090  label="C_element : 048"  # scripted group (container) (typed FeaturePython)
  n = 2
  ref = C_element
FEATURE [App::DocumentObjectGroupPython] H_element082  label="H_element : 044"  # scripted group (container) (typed FeaturePython)
  n = 4
  ref = H_element
FEATURE [App::DocumentObjectGroupPython] O_element082  label="O_element : 043"  # scripted group (container) (typed FeaturePython)
  n = 1
  ref = O_element
FEATURE [App::DocumentObjectGroupPython] G4_POLYVINYL_ALCOHOL  # scripted group (container) (typed FeaturePython)
  Dunit = g/cm3
  Dvalue = 1.3
  Group = -> [C_element090,H_element082,O_element082]
  conduct = 2
  density = 1
  expand = 3
  formula = G4_POLYVINYL_ALCOHOL
  name = G4_POLYVINYL_ALCOHOL
  specific = 4
FEATURE [App::DocumentObjectGroupPython] C_element091  label="C_element : 049"  # scripted group (container) (typed FeaturePython)
  n = 8
  ref = C_element
FEATURE [App::DocumentObjectGroupPython] H_element083  label="H_element : 045"  # scripted group (container) (typed FeaturePython)
  n = 14
  ref = H_element
FEATURE [App::DocumentObjectGroupPython] O_element083  label="O_element : 044"  # scripted group (container) (typed FeaturePython)
  n = 2
  ref = O_element
FEATURE [App::DocumentObjectGroupPython] G4_POLYVINYL_BUTYRAL  # scripted group (container) (typed FeaturePython)
  Dunit = g/cm3
  Dvalue = 1.12
  Group = -> [C_element091,H_element083,O_element083]
  conduct = 2
  density = 1
  expand = 3
  formula = G4_POLYVINYL_BUTYRAL
  name = G4_POLYVINYL_BUTYRAL
  specific = 4
FEATURE [App::DocumentObjectGroupPython] C_element092  label="C_element : 050"  # scripted group (container) (typed FeaturePython)
  n = 2
  ref = C_element
FEATURE [App::DocumentObjectGroupPython] H_element084  label="H_element : 046"  # scripted group (container) (typed FeaturePython)
  n = 3
  ref = H_element
FEATURE [App::DocumentObjectGroupPython] Cl_element019  label="Cl_element : 009"  # scripted group (container) (typed FeaturePython)
  n = 1
  ref = Cl_element
FEATURE [App::DocumentObjectGroupPython] G4_POLYVINYL_CHLORIDE  # scripted group (container) (typed FeaturePython)
  Dunit = g/cm3
  Dvalue = 1.3
  Group = -> [C_element092,H_element084,Cl_element019]
  conduct = 2
  density = 1
  expand = 3
  formula = G4_POLYVINYL_CHLORIDE
  name = G4_POLYVINYL_CHLORIDE
  specific = 4
FEATURE [App::DocumentObjectGroupPython] C_element093  label="C_element : 051"  # scripted group (container) (typed FeaturePython)
  n = 2
  ref = C_element
FEATURE [App::DocumentObjectGroupPython] H_element085  label="H_element : 047"  # scripted group (container) (typed FeaturePython)
  n = 2
  ref = H_element
FEATURE [App::DocumentObjectGroupPython] Cl_element020  label="Cl_element : 010"  # scripted group (container) (typed FeaturePython)
  n = 2
  ref = Cl_element
FEATURE [App::DocumentObjectGroupPython] G4_POLYVINYLIDENE_CHLORIDE  # scripted group (container) (typed FeaturePython)
  Dunit = g/cm3
  Dvalue = 1.7
  Group = -> [C_element093,H_element085,Cl_element020]
  conduct = 2
  density = 1
  expand = 3
  formula = G4_POLYVINYLIDENE_CHLORIDE
  name = G4_POLYVINYLIDENE_CHLORIDE
  specific = 4
FEATURE [App::DocumentObjectGroupPython] C_element094  label="C_element : 052"  # scripted group (container) (typed FeaturePython)
  n = 2
  ref = C_element
FEATURE [App::DocumentObjectGroupPython] H_element086  label="H_element : 048"  # scripted group (container) (typed FeaturePython)
  n = 2
  ref = H_element
FEATURE [App::DocumentObjectGroupPython] F_element016  label="F_element : 007"  # scripted group (container) (typed FeaturePython)
  n = 2
  ref = F_element
FEATURE [App::DocumentObjectGroupPython] G4_POLYVINYLIDENE_FLUORIDE  # scripted group (container) (typed FeaturePython)
  Dunit = g/cm3
  Dvalue = 1.76
  Group = -> [C_element094,H_element086,F_element016]
  conduct = 2
  density = 1
  expand = 3
  formula = G4_POLYVINYLIDENE_FLUORIDE
  name = G4_POLYVINYLIDENE_FLUORIDE
  specific = 4
FEATURE [App::DocumentObjectGroupPython] C_element095  label="C_element : 053"  # scripted group (container) (typed FeaturePython)
  n = 6
  ref = C_element
FEATURE [App::DocumentObjectGroupPython] H_element087  label="H_element : 9"  # scripted group (container) (typed FeaturePython)
  n = 9
  ref = H_element
FEATURE [App::DocumentObjectGroupPython] N_element037  label="N_element : 016"  # scripted group (container) (typed FeaturePython)
  n = 1
  ref = N_element
FEATURE [App::DocumentObjectGroupPython] O_element084  label="O_element : 045"  # scripted group (container) (typed FeaturePython)
  n = 1
  ref = O_element
FEATURE [App::DocumentObjectGroupPython] G4_POLYVINYL_PYRROLIDONE  # scripted group (container) (typed FeaturePython)
  Dunit = g/cm3
  Dvalue = 1.25
  Group = -> [C_element095,H_element087,N_element037,O_element084]
  conduct = 2
  density = 1
  expand = 3
  formula = G4_POLYVINYL_PYRROLIDONE
  name = G4_POLYVINYL_PYRROLIDONE
  specific = 4
FEATURE [App::DocumentObjectGroupPython] K_element008  label="K_element : 1"  # scripted group (container) (typed FeaturePython)
  n = 1
  ref = K_element
FEATURE [App::DocumentObjectGroupPython] I_element006  label="I_element : 003"  # scripted group (container) (typed FeaturePython)
  n = 1
  ref = I_element
FEATURE [App::DocumentObjectGroupPython] G4_POTASSIUM_IODIDE  # scripted group (container) (typed FeaturePython)
  Dunit = g/cm3
  Dvalue = 3.13
  Group = -> [K_element008,I_element006]
  conduct = 2
  density = 1
  expand = 3
  formula = G4_POTASSIUM_IODIDE
  name = G4_POTASSIUM_IODIDE
  specific = 4
FEATURE [App::DocumentObjectGroupPython] K_element009  label="K_element : 2"  # scripted group (container) (typed FeaturePython)
  n = 2
  ref = K_element
FEATURE [App::DocumentObjectGroupPython] O_element085  label="O_element : 046"  # scripted group (container) (typed FeaturePython)
  n = 1
  ref = O_element
FEATURE [App::DocumentObjectGroupPython] G4_POTASSIUM_OXIDE  # scripted group (container) (typed FeaturePython)
  Dunit = g/cm3
  Dvalue = 2.32
  Group = -> [K_element009,O_element085]
  conduct = 2
  density = 1
  expand = 3
  formula = G4_POTASSIUM_OXIDE
  name = G4_POTASSIUM_OXIDE
  specific = 4
FEATURE [App::DocumentObjectGroupPython] C_element096  label="C_element : 054"  # scripted group (container) (typed FeaturePython)
  n = 3
  ref = C_element
FEATURE [App::DocumentObjectGroupPython] H_element088  label="H_element : 049"  # scripted group (container) (typed FeaturePython)
  n = 8
  ref = H_element
FEATURE [App::DocumentObjectGroupPython] G4_PROPANE  # scripted group (container) (typed FeaturePython)
  Dunit = g/cm3
  Dvalue = 0.00187939
  Group = -> [C_element096,H_element088]
  conduct = 2
  density = 1
  expand = 3
  formula = G4_PROPANE
  name = G4_PROPANE
  specific = 4
FEATURE [App::DocumentObjectGroupPython] C_element097  label="C_element : 055"  # scripted group (container) (typed FeaturePython)
  n = 3
  ref = C_element
FEATURE [App::DocumentObjectGroupPython] H_element089  label="H_element : 050"  # scripted group (container) (typed FeaturePython)
  n = 8
  ref = H_element
FEATURE [App::DocumentObjectGroupPython] G4_lPROPANE  # scripted group (container) (typed FeaturePython)
  Dunit = g/cm3
  Dvalue = 0.43
  Group = -> [C_element097,H_element089]
  conduct = 2
  density = 1
  expand = 3
  formula = G4_lPROPANE
  name = G4_lPROPANE
  specific = 4
FEATURE [App::DocumentObjectGroupPython] C_element098  label="C_element : 056"  # scripted group (container) (typed FeaturePython)
  n = 3
  ref = C_element
FEATURE [App::DocumentObjectGroupPython] H_element090  label="H_element : 051"  # scripted group (container) (typed FeaturePython)
  n = 8
  ref = H_element
FEATURE [App::DocumentObjectGroupPython] O_element086  label="O_element : 047"  # scripted group (container) (typed FeaturePython)
  n = 1
  ref = O_element
FEATURE [App::DocumentObjectGroupPython] G4_N_PROPYL_ALCOHOL  label="G4_N-PROPYL_ALCOHOL"  # scripted group (container) (typed FeaturePython)
  Dunit = g/cm3
  Dvalue = 0.8035
  Group = -> [C_element098,H_element090,O_element086]
  conduct = 2
  density = 1
  expand = 3
  formula = G4_N-PROPYL_ALCOHOL
  name = G4_N-PROPYL_ALCOHOL
  specific = 4
FEATURE [App::DocumentObjectGroupPython] C_element099  label="C_element : 057"  # scripted group (container) (typed FeaturePython)
  n = 5
  ref = C_element
FEATURE [App::DocumentObjectGroupPython] H_element091  label="H_element : 052"  # scripted group (container) (typed FeaturePython)
  n = 5
  ref = H_element
FEATURE [App::DocumentObjectGroupPython] N_element038  label="N_element : 017"  # scripted group (container) (typed FeaturePython)
  n = 1
  ref = N_element
FEATURE [App::DocumentObjectGroupPython] G4_PYRIDINE  # scripted group (container) (typed FeaturePython)
  Dunit = g/cm3
  Dvalue = 0.9819
  Group = -> [C_element099,H_element091,N_element038]
  conduct = 2
  density = 1
  expand = 3
  formula = G4_PYRIDINE
  name = G4_PYRIDINE
  specific = 4
FEATURE [App::DocumentObjectGroupPython] H_element092  label="H_element : 0.144"  # scripted group (container) (typed FeaturePython)
  n = 0.143711
FEATURE [App::DocumentObjectGroupPython] C_element100  label="C_element : 0.856"  # scripted group (container) (typed FeaturePython)
  n = 0.856289
FEATURE [App::DocumentObjectGroupPython] G4_RUBBER_BUTYL  # scripted group (container) (typed FeaturePython)
  Dunit = g/cm3
  Dvalue = 0.92
  Group = -> [H_element092,C_element100]
  conduct = 2
  density = 1
  expand = 3
  formula = G4_RUBBER_BUTYL
  name = G4_RUBBER_BUTYL
  specific = 4
FEATURE [App::DocumentObjectGroupPython] H_element093  label="H_element : 0.118"  # scripted group (container) (typed FeaturePython)
  n = 0.118371
FEATURE [App::DocumentObjectGroupPython] C_element101  label="C_element : 0.882"  # scripted group (container) (typed FeaturePython)
  n = 0.881629
FEATURE [App::DocumentObjectGroupPython] G4_RUBBER_NATURAL  # scripted group (container) (typed FeaturePython)
  Dunit = g/cm3
  Dvalue = 0.92
  Group = -> [H_element093,C_element101]
  conduct = 2
  density = 1
  expand = 3
  formula = G4_RUBBER_NATURAL
  name = G4_RUBBER_NATURAL
  specific = 4
FEATURE [App::DocumentObjectGroupPython] H_element094  label="H_element : 0.145"  # scripted group (container) (typed FeaturePython)
  n = 0.05692
FEATURE [App::DocumentObjectGroupPython] C_element102  label="C_element : 0.543"  # scripted group (container) (typed FeaturePython)
  n = 0.542646
FEATURE [App::DocumentObjectGroupPython] Cl_element021  label="Cl_element : 0.400"  # scripted group (container) (typed FeaturePython)
  n = 0.400434
FEATURE [App::DocumentObjectGroupPython] G4_RUBBER_NEOPRENE  # scripted group (container) (typed FeaturePython)
  Dunit = g/cm3
  Dvalue = 1.23
  Group = -> [H_element094,C_element102,Cl_element021]
  conduct = 2
  density = 1
  expand = 3
  formula = G4_RUBBER_NEOPRENE
  name = G4_RUBBER_NEOPRENE
  specific = 4
FEATURE [App::DocumentObjectGroupPython] Si_element006  label="Si_element : 1"  # scripted group (container) (typed FeaturePython)
  n = 1
  ref = Si_element
FEATURE [App::DocumentObjectGroupPython] O_element087  label="O_element : 048"  # scripted group (container) (typed FeaturePython)
  n = 2
  ref = O_element
FEATURE [App::DocumentObjectGroupPython] G4_SILICON_DIOXIDE001  label="G4_SILICON_DIOXIDE"  # scripted group (container) (typed FeaturePython)
  Dunit = g/cm3
  Dvalue = 2.32
  Group = -> [Si_element006,O_element087]
  conduct = 2
  density = 1
  expand = 3
  formula = G4_SILICON_DIOXIDE
  name = G4_SILICON_DIOXIDE
  specific = 4
FEATURE [App::DocumentObjectGroupPython] Ag_element002  label="Ag_element : 1"  # scripted group (container) (typed FeaturePython)
  n = 1
  ref = Ag_element
FEATURE [App::DocumentObjectGroupPython] Br_element005  label="Br_element : 003"  # scripted group (container) (typed FeaturePython)
  n = 1
  ref = Br_element
FEATURE [App::DocumentObjectGroupPython] G4_SILVER_BROMIDE  # scripted group (container) (typed FeaturePython)
  Dunit = g/cm3
  Dvalue = 6.473
  Group = -> [Ag_element002,Br_element005]
  conduct = 2
  density = 1
  expand = 3
  formula = G4_SILVER_BROMIDE
  name = G4_SILVER_BROMIDE
  specific = 4
FEATURE [App::DocumentObjectGroupPython] Ag_element003  label="Ag_element : 002"  # scripted group (container) (typed FeaturePython)
  n = 1
  ref = Ag_element
FEATURE [App::DocumentObjectGroupPython] Cl_element022  label="Cl_element : 011"  # scripted group (container) (typed FeaturePython)
  n = 1
  ref = Cl_element
FEATURE [App::DocumentObjectGroupPython] G4_SILVER_CHLORIDE  # scripted group (container) (typed FeaturePython)
  Dunit = g/cm3
  Dvalue = 5.56
  Group = -> [Ag_element003,Cl_element022]
  conduct = 2
  density = 1
  expand = 3
  formula = G4_SILVER_CHLORIDE
  name = G4_SILVER_CHLORIDE
  specific = 4
FEATURE [App::DocumentObjectGroupPython] Br_element006  label="Br_element : 0.423"  # scripted group (container) (typed FeaturePython)
  n = 0.422895
FEATURE [App::DocumentObjectGroupPython] Ag_element004  label="Ag_element : 0.574"  # scripted group (container) (typed FeaturePython)
  n = 0.573748
FEATURE [App::DocumentObjectGroupPython] I_element007  label="I_element : 0.649"  # scripted group (container) (typed FeaturePython)
  n = 0.003357
FEATURE [App::DocumentObjectGroupPython] G4_SILVER_HALIDES  # scripted group (container) (typed FeaturePython)
  Dunit = g/cm3
  Dvalue = 6.47
  Group = -> [Br_element006,Ag_element004,I_element007]
  conduct = 2
  density = 1
  expand = 3
  formula = G4_SILVER_HALIDES
  name = G4_SILVER_HALIDES
  specific = 4
FEATURE [App::DocumentObjectGroupPython] Ag_element005  label="Ag_element : 003"  # scripted group (container) (typed FeaturePython)
  n = 1
  ref = Ag_element
FEATURE [App::DocumentObjectGroupPython] I_element008  label="I_element : 004"  # scripted group (container) (typed FeaturePython)
  n = 1
  ref = I_element
FEATURE [App::DocumentObjectGroupPython] G4_SILVER_IODIDE  # scripted group (container) (typed FeaturePython)
  Dunit = g/cm3
  Dvalue = 6.01
  Group = -> [Ag_element005,I_element008]
  conduct = 2
  density = 1
  expand = 3
  formula = G4_SILVER_IODIDE
  name = G4_SILVER_IODIDE
  specific = 4
FEATURE [App::DocumentObjectGroupPython] H_element095  label="H_element : 0.100"  # scripted group (container) (typed FeaturePython)
  n = 0.1
FEATURE [App::DocumentObjectGroupPython] C_element103  label="C_element : 0.204"  # scripted group (container) (typed FeaturePython)
  n = 0.204
FEATURE [App::DocumentObjectGroupPython] N_element039  label="N_element : 0.759"  # scripted group (container) (typed FeaturePython)
  n = 0.042
FEATURE [App::DocumentObjectGroupPython] O_element088  label="O_element : 0.645"  # scripted group (container) (typed FeaturePython)
  n = 0.645
FEATURE [App::DocumentObjectGroupPython] Na_element013  label="Na_element : 0.100"  # scripted group (container) (typed FeaturePython)
  n = 0.002
FEATURE [App::DocumentObjectGroupPython] P_element009  label="P_element : 0.107"  # scripted group (container) (typed FeaturePython)
  n = 0.001
FEATURE [App::DocumentObjectGroupPython] S_element020  label="S_element : 0.021"  # scripted group (container) (typed FeaturePython)
  n = 0.002
FEATURE [App::DocumentObjectGroupPython] Cl_element023  label="Cl_element : 0.590"  # scripted group (container) (typed FeaturePython)
  n = 0.003
FEATURE [App::DocumentObjectGroupPython] K_element010  label="K_element : 0.001"  # scripted group (container) (typed FeaturePython)
  n = 0.001
FEATURE [App::DocumentObjectGroupPython] G4_SKIN_ICRP  # scripted group (container) (typed FeaturePython)
  Dunit = g/cm3
  Dvalue = 1.09
  Group = -> [H_element095,C_element103,N_element039,O_element088,Na_element013,P_element009,S_element020,Cl_element023,K_element010]
  conduct = 2
  density = 1
  expand = 3
  formula = G4_SKIN_ICRP
  name = G4_SKIN_ICRP
  specific = 4
FEATURE [App::DocumentObjectGroupPython] Na_element014  label="Na_element : 2"  # scripted group (container) (typed FeaturePython)
  n = 2
  ref = Na_element
FEATURE [App::DocumentObjectGroupPython] C_element104  label="C_element : 058"  # scripted group (container) (typed FeaturePython)
  n = 1
  ref = C_element
FEATURE [App::DocumentObjectGroupPython] O_element089  label="O_element : 049"  # scripted group (container) (typed FeaturePython)
  n = 3
  ref = O_element
FEATURE [App::DocumentObjectGroupPython] G4_SODIUM_CARBONATE  # scripted group (container) (typed FeaturePython)
  Dunit = g/cm3
  Dvalue = 2.532
  Group = -> [Na_element014,C_element104,O_element089]
  conduct = 2
  density = 1
  expand = 3
  formula = G4_SODIUM_CARBONATE
  name = G4_SODIUM_CARBONATE
  specific = 4
FEATURE [App::DocumentObjectGroupPython] Na_element015  label="Na_element : 1"  # scripted group (container) (typed FeaturePython)
  n = 1
  ref = Na_element
FEATURE [App::DocumentObjectGroupPython] I_element009  label="I_element : 005"  # scripted group (container) (typed FeaturePython)
  n = 1
  ref = I_element
FEATURE [App::DocumentObjectGroupPython] G4_SODIUM_IODIDE  # scripted group (container) (typed FeaturePython)
  Dunit = g/cm3
  Dvalue = 3.667
  Group = -> [Na_element015,I_element009]
  conduct = 2
  density = 1
  expand = 3
  formula = G4_SODIUM_IODIDE
  name = G4_SODIUM_IODIDE
  specific = 4
FEATURE [App::DocumentObjectGroupPython] Na_element016  label="Na_element : 003"  # scripted group (container) (typed FeaturePython)
  n = 2
  ref = Na_element
FEATURE [App::DocumentObjectGroupPython] O_element090  label="O_element : 050"  # scripted group (container) (typed FeaturePython)
  n = 1
  ref = O_element
FEATURE [App::DocumentObjectGroupPython] G4_SODIUM_MONOXIDE  # scripted group (container) (typed FeaturePython)
  Dunit = g/cm3
  Dvalue = 2.27
  Group = -> [Na_element016,O_element090]
  conduct = 2
  density = 1
  expand = 3
  formula = G4_SODIUM_MONOXIDE
  name = G4_SODIUM_MONOXIDE
  specific = 4
FEATURE [App::DocumentObjectGroupPython] Na_element017  label="Na_element : 004"  # scripted group (container) (typed FeaturePython)
  n = 1
  ref = Na_element
FEATURE [App::DocumentObjectGroupPython] N_element040  label="N_element : 018"  # scripted group (container) (typed FeaturePython)
  n = 1
  ref = N_element
FEATURE [App::DocumentObjectGroupPython] O_element091  label="O_element : 051"  # scripted group (container) (typed FeaturePython)
  n = 3
  ref = O_element
FEATURE [App::DocumentObjectGroupPython] G4_SODIUM_NITRATE  # scripted group (container) (typed FeaturePython)
  Dunit = g/cm3
  Dvalue = 2.261
  Group = -> [Na_element017,N_element040,O_element091]
  conduct = 2
  density = 1
  expand = 3
  formula = G4_SODIUM_NITRATE
  name = G4_SODIUM_NITRATE
  specific = 4
FEATURE [App::DocumentObjectGroupPython] C_element105  label="C_element : 059"  # scripted group (container) (typed FeaturePython)
  n = 14
  ref = C_element
FEATURE [App::DocumentObjectGroupPython] H_element096  label="H_element : 053"  # scripted group (container) (typed FeaturePython)
  n = 12
  ref = H_element
FEATURE [App::DocumentObjectGroupPython] G4_STILBENE  # scripted group (container) (typed FeaturePython)
  Dunit = g/cm3
  Dvalue = 0.9707
  Group = -> [C_element105,H_element096]
  conduct = 2
  density = 1
  expand = 3
  formula = G4_STILBENE
  name = G4_STILBENE
  specific = 4
FEATURE [App::DocumentObjectGroupPython] C_element106  label="C_element : 12"  # scripted group (container) (typed FeaturePython)
  n = 12
  ref = C_element
FEATURE [App::DocumentObjectGroupPython] H_element097  label="H_element : 22"  # scripted group (container) (typed FeaturePython)
  n = 22
  ref = H_element
FEATURE [App::DocumentObjectGroupPython] O_element092  label="O_element : 11"  # scripted group (container) (typed FeaturePython)
  n = 11
  ref = O_element
FEATURE [App::DocumentObjectGroupPython] G4_SUCROSE  # scripted group (container) (typed FeaturePython)
  Dunit = g/cm3
  Dvalue = 1.5805
  Group = -> [C_element106,H_element097,O_element092]
  conduct = 2
  density = 1
  expand = 3
  formula = G4_SUCROSE
  name = G4_SUCROSE
  specific = 4
FEATURE [App::DocumentObjectGroupPython] C_element107  label="C_element : 18"  # scripted group (container) (typed FeaturePython)
  n = 18
  ref = C_element
FEATURE [App::DocumentObjectGroupPython] H_element098  label="H_element : 054"  # scripted group (container) (typed FeaturePython)
  n = 14
  ref = H_element
FEATURE [App::DocumentObjectGroupPython] G4_TERPHENYL  # scripted group (container) (typed FeaturePython)
  Dunit = g/cm3
  Dvalue = 1.24
  Group = -> [C_element107,H_element098]
  conduct = 2
  density = 1
  expand = 3
  formula = G4_TERPHENYL
  name = G4_TERPHENYL
  specific = 4
FEATURE [App::DocumentObjectGroupPython] H_element099  label="H_element : 0.146"  # scripted group (container) (typed FeaturePython)
  n = 0.106
FEATURE [App::DocumentObjectGroupPython] C_element108  label="C_element : 0.883"  # scripted group (container) (typed FeaturePython)
  n = 0.099
FEATURE [App::DocumentObjectGroupPython] N_element041  label="N_element : 0.020"  # scripted group (container) (typed FeaturePython)
  n = 0.02
FEATURE [App::DocumentObjectGroupPython] O_element093  label="O_element : 0.766"  # scripted group (container) (typed FeaturePython)
  n = 0.766
FEATURE [App::DocumentObjectGroupPython] Na_element018  label="Na_element : 0.101"  # scripted group (container) (typed FeaturePython)
  n = 0.002
FEATURE [App::DocumentObjectGroupPython] P_element010  label="P_element : 0.108"  # scripted group (container) (typed FeaturePython)
  n = 0.001
FEATURE [App::DocumentObjectGroupPython] S_element021  label="S_element : 0.022"  # scripted group (container) (typed FeaturePython)
  n = 0.002
FEATURE [App::DocumentObjectGroupPython] Cl_element024  label="Cl_element : 0.002"  # scripted group (container) (typed FeaturePython)
  n = 0.002
FEATURE [App::DocumentObjectGroupPython] K_element011  label="K_element : 0.017"  # scripted group (container) (typed FeaturePython)
  n = 0.002
FEATURE [App::DocumentObjectGroupPython] G4_TESTIS_ICRP  # scripted group (container) (typed FeaturePython)
  Dunit = g/cm3
  Dvalue = 1.04
  Group = -> [H_element099,C_element108,N_element041,O_element093,Na_element018,P_element010,S_element021,Cl_element024,K_element011]
  conduct = 2
  density = 1
  expand = 3
  formula = G4_TESTIS_ICRP
  name = G4_TESTIS_ICRP
  specific = 4
FEATURE [App::DocumentObjectGroupPython] C_element109  label="C_element : 060"  # scripted group (container) (typed FeaturePython)
  n = 2
  ref = C_element
FEATURE [App::DocumentObjectGroupPython] Cl_element025  label="Cl_element : 012"  # scripted group (container) (typed FeaturePython)
  n = 4
  ref = Cl_element
FEATURE [App::DocumentObjectGroupPython] G4_TETRACHLOROETHYLENE  # scripted group (container) (typed FeaturePython)
  Dunit = g/cm3
  Dvalue = 1.625
  Group = -> [C_element109,Cl_element025]
  conduct = 2
  density = 1
  expand = 3
  formula = G4_TETRACHLOROETHYLENE
  name = G4_TETRACHLOROETHYLENE
  specific = 4
FEATURE [App::DocumentObjectGroupPython] Tl_element001  label="Tl_element : 1"  # scripted group (container) (typed FeaturePython)
  n = 1
  ref = Tl_element
FEATURE [App::DocumentObjectGroupPython] Cl_element026  label="Cl_element : 013"  # scripted group (container) (typed FeaturePython)
  n = 1
  ref = Cl_element
FEATURE [App::DocumentObjectGroupPython] G4_THALLIUM_CHLORIDE  # scripted group (container) (typed FeaturePython)
  Dunit = g/cm3
  Dvalue = 7.004
  Group = -> [Tl_element001,Cl_element026]
  conduct = 2
  density = 1
  expand = 3
  formula = G4_THALLIUM_CHLORIDE
  name = G4_THALLIUM_CHLORIDE
  specific = 4
FEATURE [App::DocumentObjectGroupPython] H_element100  label="H_element : 0.147"  # scripted group (container) (typed FeaturePython)
  n = 0.105
FEATURE [App::DocumentObjectGroupPython] C_element110  label="C_element : 0.256"  # scripted group (container) (typed FeaturePython)
  n = 0.256
FEATURE [App::DocumentObjectGroupPython] N_element042  label="N_element : 0.760"  # scripted group (container) (typed FeaturePython)
  n = 0.027
FEATURE [App::DocumentObjectGroupPython] O_element094  label="O_element : 0.602"  # scripted group (container) (typed FeaturePython)
  n = 0.602
FEATURE [App::DocumentObjectGroupPython] Na_element019  label="Na_element : 0.102"  # scripted group (container) (typed FeaturePython)
  n = 0.001
FEATURE [App::DocumentObjectGroupPython] P_element011  label="P_element : 0.109"  # scripted group (container) (typed FeaturePython)
  n = 0.002
FEATURE [App::DocumentObjectGroupPython] S_element022  label="S_element : 0.023"  # scripted group (container) (typed FeaturePython)
  n = 0.003
FEATURE [App::DocumentObjectGroupPython] Cl_element027  label="Cl_element : 0.591"  # scripted group (container) (typed FeaturePython)
  n = 0.002
FEATURE [App::DocumentObjectGroupPython] K_element012  label="K_element : 0.018"  # scripted group (container) (typed FeaturePython)
  n = 0.002
FEATURE [App::DocumentObjectGroupPython] G4_TISSUE_SOFT_ICRP  # scripted group (container) (typed FeaturePython)
  Dunit = g/cm3
  Dvalue = 1.03
  Group = -> [H_element100,C_element110,N_element042,O_element094,Na_element019,P_element011,S_element022,Cl_element027,K_element012]
  conduct = 2
  density = 1
  expand = 3
  formula = G4_TISSUE_SOFT_ICRP
  name = G4_TISSUE_SOFT_ICRP
  specific = 4
FEATURE [App::DocumentObjectGroupPython] H_element101  label="H_element : 0.148"  # scripted group (container) (typed FeaturePython)
  n = 0.101
FEATURE [App::DocumentObjectGroupPython] C_element111  label="C_element : 0.111"  # scripted group (container) (typed FeaturePython)
  n = 0.111
FEATURE [App::DocumentObjectGroupPython] N_element043  label="N_element : 0.026"  # scripted group (container) (typed FeaturePython)
  n = 0.026
FEATURE [App::DocumentObjectGroupPython] O_element095  label="O_element : 0.762"  # scripted group (container) (typed FeaturePython)
  n = 0.762
FEATURE [App::DocumentObjectGroupPython] G4_TISSUE_SOFT_ICRU_4  label="G4_TISSUE_SOFT_ICRU-4"  # scripted group (container) (typed FeaturePython)
  Dunit = g/cm3
  Dvalue = 1
  Group = -> [H_element101,C_element111,N_element043,O_element095]
  conduct = 2
  density = 1
  expand = 3
  formula = G4_TISSUE_SOFT_ICRU-4
  name = G4_TISSUE_SOFT_ICRU-4
  specific = 4
FEATURE [App::DocumentObjectGroupPython] H_element102  label="H_element : 0.149"  # scripted group (container) (typed FeaturePython)
  n = 0.101869
FEATURE [App::DocumentObjectGroupPython] C_element112  label="C_element : 0.456"  # scripted group (container) (typed FeaturePython)
  n = 0.456179
FEATURE [App::DocumentObjectGroupPython] N_element044  label="N_element : 0.761"  # scripted group (container) (typed FeaturePython)
  n = 0.035172
FEATURE [App::DocumentObjectGroupPython] O_element096  label="O_element : 0.407"  # scripted group (container) (typed FeaturePython)
  n = 0.40678
FEATURE [App::DocumentObjectGroupPython] G4_TISSUE_METHANE  label="G4_TISSUE-METHANE"  # scripted group (container) (typed FeaturePython)
  Dunit = g/cm3
  Dvalue = 0.00106409
  Group = -> [H_element102,C_element112,N_element044,O_element096]
  conduct = 2
  density = 1
  expand = 3
  formula = G4_TISSUE-METHANE
  name = G4_TISSUE-METHANE
  specific = 4
FEATURE [App::DocumentObjectGroupPython] H_element103  label="H_element : 0.103"  # scripted group (container) (typed FeaturePython)
  n = 0.102672
FEATURE [App::DocumentObjectGroupPython] C_element113  label="C_element : 0.569"  # scripted group (container) (typed FeaturePython)
  n = 0.56894
FEATURE [App::DocumentObjectGroupPython] N_element045  label="N_element : 0.762"  # scripted group (container) (typed FeaturePython)
  n = 0.035022
FEATURE [App::DocumentObjectGroupPython] O_element097  label="O_element : 0.293"  # scripted group (container) (typed FeaturePython)
  n = 0.293366
FEATURE [App::DocumentObjectGroupPython] G4_TISSUE_PROPANE  label="G4_TISSUE-PROPANE"  # scripted group (container) (typed FeaturePython)
  Dunit = g/cm3
  Dvalue = 0.00182628
  Group = -> [H_element103,C_element113,N_element045,O_element097]
  conduct = 2
  density = 1
  expand = 3
  formula = G4_TISSUE-PROPANE
  name = G4_TISSUE-PROPANE
  specific = 4
FEATURE [App::DocumentObjectGroupPython] Ti_element003  label="Ti_element : 1"  # scripted group (container) (typed FeaturePython)
  n = 1
  ref = Ti_element
FEATURE [App::DocumentObjectGroupPython] O_element098  label="O_element : 052"  # scripted group (container) (typed FeaturePython)
  n = 2
  ref = O_element
FEATURE [App::DocumentObjectGroupPython] G4_TITANIUM_DIOXIDE  # scripted group (container) (typed FeaturePython)
  Dunit = g/cm3
  Dvalue = 4.26
  Group = -> [Ti_element003,O_element098]
  conduct = 2
  density = 1
  expand = 3
  formula = G4_TITANIUM_DIOXIDE
  name = G4_TITANIUM_DIOXIDE
  specific = 4
FEATURE [App::DocumentObjectGroupPython] C_element114  label="C_element : 061"  # scripted group (container) (typed FeaturePython)
  n = 7
  ref = C_element
FEATURE [App::DocumentObjectGroupPython] H_element104  label="H_element : 055"  # scripted group (container) (typed FeaturePython)
  n = 8
  ref = H_element
FEATURE [App::DocumentObjectGroupPython] G4_TOLUENE  # scripted group (container) (typed FeaturePython)
  Dunit = g/cm3
  Dvalue = 0.8669
  Group = -> [C_element114,H_element104]
  conduct = 2
  density = 1
  expand = 3
  formula = G4_TOLUENE
  name = G4_TOLUENE
  specific = 4
FEATURE [App::DocumentObjectGroupPython] C_element115  label="C_element : 062"  # scripted group (container) (typed FeaturePython)
  n = 2
  ref = C_element
FEATURE [App::DocumentObjectGroupPython] H_element105  label="H_element : 056"  # scripted group (container) (typed FeaturePython)
  n = 1
  ref = H_element
FEATURE [App::DocumentObjectGroupPython] Cl_element028  label="Cl_element : 014"  # scripted group (container) (typed FeaturePython)
  n = 3
  ref = Cl_element
FEATURE [App::DocumentObjectGroupPython] G4_TRICHLOROETHYLENE  # scripted group (container) (typed FeaturePython)
  Dunit = g/cm3
  Dvalue = 1.46
  Group = -> [C_element115,H_element105,Cl_element028]
  conduct = 2
  density = 1
  expand = 3
  formula = G4_TRICHLOROETHYLENE
  name = G4_TRICHLOROETHYLENE
  specific = 4
FEATURE [App::DocumentObjectGroupPython] C_element116  label="C_element : 063"  # scripted group (container) (typed FeaturePython)
  n = 6
  ref = C_element
FEATURE [App::DocumentObjectGroupPython] H_element106  label="H_element : 15"  # scripted group (container) (typed FeaturePython)
  n = 15
  ref = H_element
FEATURE [App::DocumentObjectGroupPython] O_element099  label="O_element : 053"  # scripted group (container) (typed FeaturePython)
  n = 4
  ref = O_element
FEATURE [App::DocumentObjectGroupPython] P_element012  label="P_element : 1"  # scripted group (container) (typed FeaturePython)
  n = 1
  ref = P_element
FEATURE [App::DocumentObjectGroupPython] G4_TRIETHYL_PHOSPHATE  # scripted group (container) (typed FeaturePython)
  Dunit = g/cm3
  Dvalue = 1.07
  Group = -> [C_element116,H_element106,O_element099,P_element012]
  conduct = 2
  density = 1
  expand = 3
  formula = G4_TRIETHYL_PHOSPHATE
  name = G4_TRIETHYL_PHOSPHATE
  specific = 4
FEATURE [App::DocumentObjectGroupPython] W_element003  label="W_element : 003"  # scripted group (container) (typed FeaturePython)
  n = 1
  ref = W_element
FEATURE [App::DocumentObjectGroupPython] F_element017  label="F_element : 6"  # scripted group (container) (typed FeaturePython)
  n = 6
  ref = F_element
FEATURE [App::DocumentObjectGroupPython] G4_TUNGSTEN_HEXAFLUORIDE  # scripted group (container) (typed FeaturePython)
  Dunit = g/cm3
  Dvalue = 2.4
  Group = -> [W_element003,F_element017]
  conduct = 2
  density = 1
  expand = 3
  formula = G4_TUNGSTEN_HEXAFLUORIDE
  name = G4_TUNGSTEN_HEXAFLUORIDE
  specific = 4
FEATURE [App::DocumentObjectGroupPython] U_element001  label="U_element : 1"  # scripted group (container) (typed FeaturePython)
  n = 1
  ref = U_element
FEATURE [App::DocumentObjectGroupPython] C_element117  label="C_element : 064"  # scripted group (container) (typed FeaturePython)
  n = 2
  ref = C_element
FEATURE [App::DocumentObjectGroupPython] G4_URANIUM_DICARBIDE  # scripted group (container) (typed FeaturePython)
  Dunit = g/cm3
  Dvalue = 11.28
  Group = -> [U_element001,C_element117]
  conduct = 2
  density = 1
  expand = 3
  formula = G4_URANIUM_DICARBIDE
  name = G4_URANIUM_DICARBIDE
  specific = 4
FEATURE [App::DocumentObjectGroupPython] U_element002  label="U_element : 002"  # scripted group (container) (typed FeaturePython)
  n = 1
  ref = U_element
FEATURE [App::DocumentObjectGroupPython] C_element118  label="C_element : 065"  # scripted group (container) (typed FeaturePython)
  n = 1
  ref = C_element
FEATURE [App::DocumentObjectGroupPython] G4_URANIUM_MONOCARBIDE  # scripted group (container) (typed FeaturePython)
  Dunit = g/cm3
  Dvalue = 13.63
  Group = -> [U_element002,C_element118]
  conduct = 2
  density = 1
  expand = 3
  formula = G4_URANIUM_MONOCARBIDE
  name = G4_URANIUM_MONOCARBIDE
  specific = 4
FEATURE [App::DocumentObjectGroupPython] U_element003  label="U_element : 003"  # scripted group (container) (typed FeaturePython)
  n = 1
  ref = U_element
FEATURE [App::DocumentObjectGroupPython] O_element100  label="O_element : 054"  # scripted group (container) (typed FeaturePython)
  n = 2
  ref = O_element
FEATURE [App::DocumentObjectGroupPython] G4_URANIUM_OXIDE  # scripted group (container) (typed FeaturePython)
  Dunit = g/cm3
  Dvalue = 10.96
  Group = -> [U_element003,O_element100]
  conduct = 2
  density = 1
  expand = 3
  formula = G4_URANIUM_OXIDE
  name = G4_URANIUM_OXIDE
  specific = 4
FEATURE [App::DocumentObjectGroupPython] C_element119  label="C_element : 066"  # scripted group (container) (typed FeaturePython)
  n = 1
  ref = C_element
FEATURE [App::DocumentObjectGroupPython] H_element107  label="H_element : 057"  # scripted group (container) (typed FeaturePython)
  n = 4
  ref = H_element
FEATURE [App::DocumentObjectGroupPython] N_element046  label="N_element : 019"  # scripted group (container) (typed FeaturePython)
  n = 2
  ref = N_element
FEATURE [App::DocumentObjectGroupPython] O_element101  label="O_element : 055"  # scripted group (container) (typed FeaturePython)
  n = 1
  ref = O_element
FEATURE [App::DocumentObjectGroupPython] G4_UREA  # scripted group (container) (typed FeaturePython)
  Dunit = g/cm3
  Dvalue = 1.323
  Group = -> [C_element119,H_element107,N_element046,O_element101]
  conduct = 2
  density = 1
  expand = 3
  formula = G4_UREA
  name = G4_UREA
  specific = 4
FEATURE [App::DocumentObjectGroupPython] C_element120  label="C_element : 067"  # scripted group (container) (typed FeaturePython)
  n = 5
  ref = C_element
FEATURE [App::DocumentObjectGroupPython] H_element108  label="H_element : 058"  # scripted group (container) (typed FeaturePython)
  n = 11
  ref = H_element
FEATURE [App::DocumentObjectGroupPython] N_element047  label="N_element : 020"  # scripted group (container) (typed FeaturePython)
  n = 1
  ref = N_element
FEATURE [App::DocumentObjectGroupPython] O_element102  label="O_element : 056"  # scripted group (container) (typed FeaturePython)
  n = 2
  ref = O_element
FEATURE [App::DocumentObjectGroupPython] G4_VALINE  # scripted group (container) (typed FeaturePython)
  Dunit = g/cm3
  Dvalue = 1.23
  Group = -> [C_element120,H_element108,N_element047,O_element102]
  conduct = 2
  density = 1
  expand = 3
  formula = G4_VALINE
  name = G4_VALINE
  specific = 4
FEATURE [App::DocumentObjectGroupPython] H_element109  label="H_element : 0.009"  # scripted group (container) (typed FeaturePython)
  n = 0.009417
FEATURE [App::DocumentObjectGroupPython] C_element121  label="C_element : 0.281"  # scripted group (container) (typed FeaturePython)
  n = 0.280555
FEATURE [App::DocumentObjectGroupPython] F_element018  label="F_element : 0.710"  # scripted group (container) (typed FeaturePython)
  n = 0.710028
FEATURE [App::DocumentObjectGroupPython] G4_VITON  # scripted group (container) (typed FeaturePython)
  Dunit = g/cm3
  Dvalue = 1.8
  Group = -> [H_element109,C_element121,F_element018]
  conduct = 2
  density = 1
  expand = 3
  formula = G4_VITON
  name = G4_VITON
  specific = 4
FEATURE [App::DocumentObjectGroupPython] H_element110  label="H_element : 059"  # scripted group (container) (typed FeaturePython)
  n = 2
  ref = H_element
FEATURE [App::DocumentObjectGroupPython] O_element103  label="O_element : 057"  # scripted group (container) (typed FeaturePython)
  n = 1
  ref = O_element
FEATURE [App::DocumentObjectGroupPython] G4_WATER  # scripted group (container) (typed FeaturePython)
  Dunit = g/cm3
  Dvalue = 1
  Group = -> [H_element110,O_element103]
  conduct = 2
  density = 1
  expand = 3
  formula = G4_WATER
  name = G4_WATER
  specific = 4
FEATURE [App::DocumentObjectGroupPython] H_element111  label="H_element : 060"  # scripted group (container) (typed FeaturePython)
  n = 2
  ref = H_element
FEATURE [App::DocumentObjectGroupPython] O_element104  label="O_element : 058"  # scripted group (container) (typed FeaturePython)
  n = 1
  ref = O_element
FEATURE [App::DocumentObjectGroupPython] G4_WATER_VAPOR  # scripted group (container) (typed FeaturePython)
  Dunit = g/cm3
  Dvalue = 0.000756182
  Group = -> [H_element111,O_element104]
  conduct = 2
  density = 1
  expand = 3
  formula = G4_WATER_VAPOR
  name = G4_WATER_VAPOR
  specific = 4
FEATURE [App::DocumentObjectGroupPython] C_element122  label="C_element : 068"  # scripted group (container) (typed FeaturePython)
  n = 8
  ref = C_element
FEATURE [App::DocumentObjectGroupPython] H_element112  label="H_element : 061"  # scripted group (container) (typed FeaturePython)
  n = 10
  ref = H_element
FEATURE [App::DocumentObjectGroupPython] G4_XYLENE  # scripted group (container) (typed FeaturePython)
  Dunit = g/cm3
  Dvalue = 0.87
  Group = -> [C_element122,H_element112]
  conduct = 2
  density = 1
  expand = 3
  formula = G4_XYLENE
  name = G4_XYLENE
  specific = 4
FEATURE [App::DocumentObjectGroupPython] C_element123  label="C_element : 069"  # scripted group (container) (typed FeaturePython)
  n = 1
  ref = C_element
FEATURE [App::DocumentObjectGroupPython] G4_GRAPHITE  # scripted group (container) (typed FeaturePython)
  Dunit = g/cm3
  Dvalue = 2.21
  Group = -> [C_element123]
  conduct = 2
  density = 1
  expand = 3
  formula = G4_GRAPHITE
  name = G4_GRAPHITE
  specific = 4
FEATURE [App::DocumentObjectGroupPython] NIST  # scripted group (container) (typed FeaturePython)
  Group = -> [G4_A_150_TISSUE,G4_ACETONE,G4_ACETYLENE,G4_ADENINE,G4_ADIPOSE_TISSUE_ICRP,G4_AIR001,G4_ALANINE,G4_ALUMINUM_OXIDE,G4_AMBER,G4_AMMONIA,G4_ANILINE,G4_ANTHRACENE,G4_B_100_BONE,G4_BAKELITE,G4_BARIUM_FLUORIDE,G4_BARIUM_SULFATE,G4_BENZENE,G4_BERYLLIUM_OXIDE,G4_BGO,G4_BLOOD_ICRP,G4_BONE_COMPACT_ICRU,G4_BONE_CORTICAL_ICRP,G4_BORON_CARBIDE,G4_BORON_OXIDE,G4_BRAIN_ICRP,G4_BUTANE,G4_N_BUTYL_ALCOHOL,G4_C_552,+152 more]
FEATURE [App::DocumentObjectGroupPython] H_element113  label="H_element : 062"  # scripted group (container) (typed FeaturePython)
  n = 1
  ref = H_element
FEATURE [App::DocumentObjectGroupPython] G4_H  # scripted group (container) (typed FeaturePython)
  Dunit = g/cm3
  Dvalue = 8.3748e-05
  Group = -> [H_element113]
  conduct = 2
  density = 1
  expand = 3
  formula = H
  name = G4_H
  specific = 4
FEATURE [App::DocumentObjectGroupPython] He_element001  label="He_element : 1"  # scripted group (container) (typed FeaturePython)
  n = 1
  ref = He_element
FEATURE [App::DocumentObjectGroupPython] G4_He  # scripted group (container) (typed FeaturePython)
  Dunit = g/cm3
  Dvalue = 0.000166322
  Group = -> [He_element001]
  conduct = 2
  density = 1
  expand = 3
  formula = He
  name = G4_He
  specific = 4
FEATURE [App::DocumentObjectGroupPython] Li_element008  label="Li_element : 008"  # scripted group (container) (typed FeaturePython)
  n = 1
  ref = Li_element
FEATURE [App::DocumentObjectGroupPython] G4_Li  # scripted group (container) (typed FeaturePython)
  Dunit = g/cm3
  Dvalue = 0.534
  Group = -> [Li_element008]
  conduct = 2
  density = 1
  expand = 3
  formula = Li
  name = G4_Li
  specific = 4
FEATURE [App::DocumentObjectGroupPython] Be_element002  label="Be_element : 002"  # scripted group (container) (typed FeaturePython)
  n = 1
  ref = Be_element
FEATURE [App::DocumentObjectGroupPython] G4_Be  # scripted group (container) (typed FeaturePython)
  Dunit = g/cm3
  Dvalue = 1.848
  Group = -> [Be_element002]
  conduct = 2
  density = 1
  expand = 3
  formula = Be
  name = G4_Be
  specific = 4
FEATURE [App::DocumentObjectGroupPython] B_element007  label="B_element : 007"  # scripted group (container) (typed FeaturePython)
  n = 1
  ref = B_element
FEATURE [App::DocumentObjectGroupPython] G4_B  # scripted group (container) (typed FeaturePython)
  Dunit = g/cm3
  Dvalue = 2.37
  Group = -> [B_element007]
  conduct = 2
  density = 1
  expand = 3
  formula = B
  name = G4_B
  specific = 4
FEATURE [App::DocumentObjectGroupPython] C_element124  label="C_element : 070"  # scripted group (container) (typed FeaturePython)
  n = 1
  ref = C_element
FEATURE [App::DocumentObjectGroupPython] G4_C  # scripted group (container) (typed FeaturePython)
  Dunit = g/cm3
  Dvalue = 2
  Group = -> [C_element124]
  conduct = 2
  density = 1
  expand = 3
  formula = C
  name = G4_C
  specific = 4
FEATURE [App::DocumentObjectGroupPython] N_element048  label="N_element : 021"  # scripted group (container) (typed FeaturePython)
  n = 1
  ref = N_element
FEATURE [App::DocumentObjectGroupPython] G4_N  # scripted group (container) (typed FeaturePython)
  Dunit = g/cm3
  Dvalue = 0.0011652
  Group = -> [N_element048]
  conduct = 2
  density = 1
  expand = 3
  formula = N
  name = G4_N
  specific = 4
FEATURE [App::DocumentObjectGroupPython] O_element105  label="O_element : 059"  # scripted group (container) (typed FeaturePython)
  n = 1
  ref = O_element
FEATURE [App::DocumentObjectGroupPython] G4_O  # scripted group (container) (typed FeaturePython)
  Dunit = g/cm3
  Dvalue = 0.00133151
  Group = -> [O_element105]
  conduct = 2
  density = 1
  expand = 3
  formula = O
  name = G4_O
  specific = 4
FEATURE [App::DocumentObjectGroupPython] F_element019  label="F_element : 008"  # scripted group (container) (typed FeaturePython)
  n = 1
  ref = F_element
FEATURE [App::DocumentObjectGroupPython] G4_F  # scripted group (container) (typed FeaturePython)
  Dunit = g/cm3
  Dvalue = 0.00158029
  Group = -> [F_element019]
  conduct = 2
  density = 1
  expand = 3
  formula = F
  name = G4_F
  specific = 4
FEATURE [App::DocumentObjectGroupPython] Ne_element001  label="Ne_element : 1"  # scripted group (container) (typed FeaturePython)
  n = 1
  ref = Ne_element
FEATURE [App::DocumentObjectGroupPython] G4_Ne  # scripted group (container) (typed FeaturePython)
  Dunit = g/cm3
  Dvalue = 0.000838505
  Group = -> [Ne_element001]
  conduct = 2
  density = 1
  expand = 3
  formula = Ne
  name = G4_Ne
  specific = 4
FEATURE [App::DocumentObjectGroupPython] Na_element020  label="Na_element : 005"  # scripted group (container) (typed FeaturePython)
  n = 1
  ref = Na_element
FEATURE [App::DocumentObjectGroupPython] G4_Na  # scripted group (container) (typed FeaturePython)
  Dunit = g/cm3
  Dvalue = 0.971
  Group = -> [Na_element020]
  conduct = 2
  density = 1
  expand = 3
  formula = Na
  name = G4_Na
  specific = 4
FEATURE [App::DocumentObjectGroupPython] Mg_element011  label="Mg_element : 005"  # scripted group (container) (typed FeaturePython)
  n = 1
  ref = Mg_element
FEATURE [App::DocumentObjectGroupPython] G4_Mg  # scripted group (container) (typed FeaturePython)
  Dunit = g/cm3
  Dvalue = 1.74
  Group = -> [Mg_element011]
  conduct = 2
  density = 1
  expand = 3
  formula = Mg
  name = G4_Mg
  specific = 4
FEATURE [App::DocumentObjectGroupPython] Al_element004  label="Al_element : 1"  # scripted group (container) (typed FeaturePython)
  n = 1
  ref = Al_element
FEATURE [App::DocumentObjectGroupPython] G4_Al  # scripted group (container) (typed FeaturePython)
  Dunit = g/cm3
  Dvalue = 2.699
  Group = -> [Al_element004]
  conduct = 2
  density = 1
  expand = 3
  formula = Al
  name = G4_Al
  specific = 4
FEATURE [App::DocumentObjectGroupPython] Si_element007  label="Si_element : 002"  # scripted group (container) (typed FeaturePython)
  n = 1
  ref = Si_element
FEATURE [App::DocumentObjectGroupPython] G4_Si  # scripted group (container) (typed FeaturePython)
  Dunit = g/cm3
  Dvalue = 2.33
  Group = -> [Si_element007]
  conduct = 2
  density = 1
  expand = 3
  formula = Si
  name = G4_Si
  specific = 4
FEATURE [App::DocumentObjectGroupPython] P_element013  label="P_element : 002"  # scripted group (container) (typed FeaturePython)
  n = 1
  ref = P_element
FEATURE [App::DocumentObjectGroupPython] G4_P  # scripted group (container) (typed FeaturePython)
  Dunit = g/cm3
  Dvalue = 2.2
  Group = -> [P_element013]
  conduct = 2
  density = 1
  expand = 3
  formula = P
  name = G4_P
  specific = 4
FEATURE [App::DocumentObjectGroupPython] S_element023  label="S_element : 007"  # scripted group (container) (typed FeaturePython)
  n = 1
  ref = S_element
FEATURE [App::DocumentObjectGroupPython] G4_S  # scripted group (container) (typed FeaturePython)
  Dunit = g/cm3
  Dvalue = 2
  Group = -> [S_element023]
  conduct = 2
  density = 1
  expand = 3
  formula = S
  name = G4_S
  specific = 4
FEATURE [App::DocumentObjectGroupPython] Cl_element029  label="Cl_element : 015"  # scripted group (container) (typed FeaturePython)
  n = 1
  ref = Cl_element
FEATURE [App::DocumentObjectGroupPython] G4_Cl  # scripted group (container) (typed FeaturePython)
  Dunit = g/cm3
  Dvalue = 0.00299473
  Group = -> [Cl_element029]
  conduct = 2
  density = 1
  expand = 3
  formula = Cl
  name = G4_Cl
  specific = 4
FEATURE [App::DocumentObjectGroupPython] Ar_element002  label="Ar_element : 1"  # scripted group (container) (typed FeaturePython)
  n = 1
  ref = Ar_element
FEATURE [App::DocumentObjectGroupPython] G4_Ar  # scripted group (container) (typed FeaturePython)
  Dunit = g/cm3
  Dvalue = 0.00166201
  Group = -> [Ar_element002]
  conduct = 2
  density = 1
  expand = 3
  formula = Ar
  name = G4_Ar
  specific = 4
FEATURE [App::DocumentObjectGroupPython] K_element013  label="K_element : 003"  # scripted group (container) (typed FeaturePython)
  n = 1
  ref = K_element
FEATURE [App::DocumentObjectGroupPython] G4_K  # scripted group (container) (typed FeaturePython)
  Dunit = g/cm3
  Dvalue = 0.862
  Group = -> [K_element013]
  conduct = 2
  density = 1
  expand = 3
  formula = K
  name = G4_K
  specific = 4
FEATURE [App::DocumentObjectGroupPython] Ca_element014  label="Ca_element : 007"  # scripted group (container) (typed FeaturePython)
  n = 1
  ref = Ca_element
FEATURE [App::DocumentObjectGroupPython] G4_Ca  # scripted group (container) (typed FeaturePython)
  Dunit = g/cm3
  Dvalue = 1.55
  Group = -> [Ca_element014]
  conduct = 2
  density = 1
  expand = 3
  formula = Ca
  name = G4_Ca
  specific = 4
FEATURE [App::DocumentObjectGroupPython] Sc_element001  label="Sc_element : 1"  # scripted group (container) (typed FeaturePython)
  n = 1
  ref = Sc_element
FEATURE [App::DocumentObjectGroupPython] G4_Sc  # scripted group (container) (typed FeaturePython)
  Dunit = g/cm3
  Dvalue = 2.989
  Group = -> [Sc_element001]
  conduct = 2
  density = 1
  expand = 3
  formula = Sc
  name = G4_Sc
  specific = 4
FEATURE [App::DocumentObjectGroupPython] Ti_element004  label="Ti_element : 002"  # scripted group (container) (typed FeaturePython)
  n = 1
  ref = Ti_element
FEATURE [App::DocumentObjectGroupPython] G4_Ti  # scripted group (container) (typed FeaturePython)
  Dunit = g/cm3
  Dvalue = 4.54
  Group = -> [Ti_element004]
  conduct = 2
  density = 1
  expand = 3
  formula = Ti
  name = G4_Ti
  specific = 4
FEATURE [App::DocumentObjectGroupPython] V_element001  label="V_element : 1"  # scripted group (container) (typed FeaturePython)
  n = 1
  ref = V_element
FEATURE [App::DocumentObjectGroupPython] G4_V  # scripted group (container) (typed FeaturePython)
  Dunit = g/cm3
  Dvalue = 6.11
  Group = -> [V_element001]
  conduct = 2
  density = 1
  expand = 3
  formula = V
  name = G4_V
  specific = 4
FEATURE [App::DocumentObjectGroupPython] Cr_element001  label="Cr_element : 1"  # scripted group (container) (typed FeaturePython)
  n = 1
  ref = Cr_element
FEATURE [App::DocumentObjectGroupPython] G4_Cr  # scripted group (container) (typed FeaturePython)
  Dunit = g/cm3
  Dvalue = 7.18
  Group = -> [Cr_element001]
  conduct = 2
  density = 1
  expand = 3
  formula = Cr
  name = G4_Cr
  specific = 4
FEATURE [App::DocumentObjectGroupPython] Mn_element001  label="Mn_element : 1"  # scripted group (container) (typed FeaturePython)
  n = 1
  ref = Mn_element
FEATURE [App::DocumentObjectGroupPython] G4_Mn  # scripted group (container) (typed FeaturePython)
  Dunit = g/cm3
  Dvalue = 7.44
  Group = -> [Mn_element001]
  conduct = 2
  density = 1
  expand = 3
  formula = Mn
  name = G4_Mn
  specific = 4
FEATURE [App::DocumentObjectGroupPython] Fe_element007  label="Fe_element : 004"  # scripted group (container) (typed FeaturePython)
  n = 1
  ref = Fe_element
FEATURE [App::DocumentObjectGroupPython] G4_Fe  # scripted group (container) (typed FeaturePython)
  Dunit = g/cm3
  Dvalue = 7.874
  Group = -> [Fe_element007]
  conduct = 2
  density = 1
  expand = 3
  formula = Fe
  name = G4_Fe
  specific = 4
FEATURE [App::DocumentObjectGroupPython] Co_element001  label="Co_element : 1"  # scripted group (container) (typed FeaturePython)
  n = 1
  ref = Co_element
FEATURE [App::DocumentObjectGroupPython] G4_Co  # scripted group (container) (typed FeaturePython)
  Dunit = g/cm3
  Dvalue = 8.9
  Group = -> [Co_element001]
  conduct = 2
  density = 1
  expand = 3
  formula = Co
  name = G4_Co
  specific = 4
FEATURE [App::DocumentObjectGroupPython] Ni_element001  label="Ni_element : 1"  # scripted group (container) (typed FeaturePython)
  n = 1
  ref = Ni_element
FEATURE [App::DocumentObjectGroupPython] G4_Ni  # scripted group (container) (typed FeaturePython)
  Dunit = g/cm3
  Dvalue = 8.902
  Group = -> [Ni_element001]
  conduct = 2
  density = 1
  expand = 3
  formula = Ni
  name = G4_Ni
  specific = 4
FEATURE [App::DocumentObjectGroupPython] Cu_element001  label="Cu_element : 1"  # scripted group (container) (typed FeaturePython)
  n = 1
  ref = Cu_element
FEATURE [App::DocumentObjectGroupPython] G4_Cu  # scripted group (container) (typed FeaturePython)
  Dunit = g/cm3
  Dvalue = 8.96
  Group = -> [Cu_element001]
  conduct = 2
  density = 1
  expand = 3
  formula = Cu
  name = G4_Cu
  specific = 4
FEATURE [App::DocumentObjectGroupPython] Zn_element001  label="Zn_element : 1"  # scripted group (container) (typed FeaturePython)
  n = 1
  ref = Zn_element
FEATURE [App::DocumentObjectGroupPython] G4_Zn  # scripted group (container) (typed FeaturePython)
  Dunit = g/cm3
  Dvalue = 7.133
  Group = -> [Zn_element001]
  conduct = 2
  density = 1
  expand = 3
  formula = Zn
  name = G4_Zn
  specific = 4
FEATURE [App::DocumentObjectGroupPython] Ga_element002  label="Ga_element : 002"  # scripted group (container) (typed FeaturePython)
  n = 1
  ref = Ga_element
FEATURE [App::DocumentObjectGroupPython] G4_Ga  # scripted group (container) (typed FeaturePython)
  Dunit = g/cm3
  Dvalue = 5.904
  Group = -> [Ga_element002]
  conduct = 2
  density = 1
  expand = 3
  formula = Ga
  name = G4_Ga
  specific = 4
FEATURE [App::DocumentObjectGroupPython] Ge_element002  label="Ge_element : 1"  # scripted group (container) (typed FeaturePython)
  n = 1
  ref = Ge_element
FEATURE [App::DocumentObjectGroupPython] G4_Ge  # scripted group (container) (typed FeaturePython)
  Dunit = g/cm3
  Dvalue = 5.323
  Group = -> [Ge_element002]
  conduct = 2
  density = 1
  expand = 3
  formula = Ge
  name = G4_Ge
  specific = 4
FEATURE [App::DocumentObjectGroupPython] As_element003  label="As_element : 002"  # scripted group (container) (typed FeaturePython)
  n = 1
  ref = As_element
FEATURE [App::DocumentObjectGroupPython] G4_As  # scripted group (container) (typed FeaturePython)
  Dunit = g/cm3
  Dvalue = 5.73
  Group = -> [As_element003]
  conduct = 2
  density = 1
  expand = 3
  formula = As
  name = G4_As
  specific = 4
FEATURE [App::DocumentObjectGroupPython] Se_element001  label="Se_element : 1"  # scripted group (container) (typed FeaturePython)
  n = 1
  ref = Se_element
FEATURE [App::DocumentObjectGroupPython] G4_Se  # scripted group (container) (typed FeaturePython)
  Dunit = g/cm3
  Dvalue = 4.5
  Group = -> [Se_element001]
  conduct = 2
  density = 1
  expand = 3
  formula = Se
  name = G4_Se
  specific = 4
FEATURE [App::DocumentObjectGroupPython] Br_element007  label="Br_element : 004"  # scripted group (container) (typed FeaturePython)
  n = 1
  ref = Br_element
FEATURE [App::DocumentObjectGroupPython] G4_Br  # scripted group (container) (typed FeaturePython)
  Dunit = g/cm3
  Dvalue = 0.0070721
  Group = -> [Br_element007]
  conduct = 2
  density = 1
  expand = 3
  formula = Br
  name = G4_Br
  specific = 4
FEATURE [App::DocumentObjectGroupPython] Kr_element001  label="Kr_element : 1"  # scripted group (container) (typed FeaturePython)
  n = 1
  ref = Kr_element
FEATURE [App::DocumentObjectGroupPython] G4_Kr  # scripted group (container) (typed FeaturePython)
  Dunit = g/cm3
  Dvalue = 0.00347832
  Group = -> [Kr_element001]
  conduct = 2
  density = 1
  expand = 3
  formula = Kr
  name = G4_Kr
  specific = 4
FEATURE [App::DocumentObjectGroupPython] Rb_element001  label="Rb_element : 1"  # scripted group (container) (typed FeaturePython)
  n = 1
  ref = Rb_element
FEATURE [App::DocumentObjectGroupPython] G4_Rb  # scripted group (container) (typed FeaturePython)
  Dunit = g/cm3
  Dvalue = 1.532
  Group = -> [Rb_element001]
  conduct = 2
  density = 1
  expand = 3
  formula = Rb
  name = G4_Rb
  specific = 4
FEATURE [App::DocumentObjectGroupPython] Sr_element001  label="Sr_element : 1"  # scripted group (container) (typed FeaturePython)
  n = 1
  ref = Sr_element
FEATURE [App::DocumentObjectGroupPython] G4_Sr  # scripted group (container) (typed FeaturePython)
  Dunit = g/cm3
  Dvalue = 2.54
  Group = -> [Sr_element001]
  conduct = 2
  density = 1
  expand = 3
  formula = Sr
  name = G4_Sr
  specific = 4
FEATURE [App::DocumentObjectGroupPython] Y_element001  label="Y_element : 1"  # scripted group (container) (typed FeaturePython)
  n = 1
  ref = Y_element
FEATURE [App::DocumentObjectGroupPython] G4_Y  # scripted group (container) (typed FeaturePython)
  Dunit = g/cm3
  Dvalue = 4.469
  Group = -> [Y_element001]
  conduct = 2
  density = 1
  expand = 3
  formula = Y
  name = G4_Y
  specific = 4
FEATURE [App::DocumentObjectGroupPython] Zr_element001  label="Zr_element : 1"  # scripted group (container) (typed FeaturePython)
  n = 1
  ref = Zr_element
FEATURE [App::DocumentObjectGroupPython] G4_Zr  # scripted group (container) (typed FeaturePython)
  Dunit = g/cm3
  Dvalue = 6.506
  Group = -> [Zr_element001]
  conduct = 2
  density = 1
  expand = 3
  formula = Zr
  name = G4_Zr
  specific = 4
FEATURE [App::DocumentObjectGroupPython] Nb_element001  label="Nb_element : 1"  # scripted group (container) (typed FeaturePython)
  n = 1
  ref = Nb_element
FEATURE [App::DocumentObjectGroupPython] G4_Nb  # scripted group (container) (typed FeaturePython)
  Dunit = g/cm3
  Dvalue = 8.57
  Group = -> [Nb_element001]
  conduct = 2
  density = 1
  expand = 3
  formula = Nb
  name = G4_Nb
  specific = 4
FEATURE [App::DocumentObjectGroupPython] Mo_element001  label="Mo_element : 1"  # scripted group (container) (typed FeaturePython)
  n = 1
  ref = Mo_element
FEATURE [App::DocumentObjectGroupPython] G4_Mo  # scripted group (container) (typed FeaturePython)
  Dunit = g/cm3
  Dvalue = 10.22
  Group = -> [Mo_element001]
  conduct = 2
  density = 1
  expand = 3
  formula = Mo
  name = G4_Mo
  specific = 4
FEATURE [App::DocumentObjectGroupPython] Tc_element001  label="Tc_element : 1"  # scripted group (container) (typed FeaturePython)
  n = 1
  ref = Tc_element
FEATURE [App::DocumentObjectGroupPython] G4_Tc  # scripted group (container) (typed FeaturePython)
  Dunit = g/cm3
  Dvalue = 11.5
  Group = -> [Tc_element001]
  conduct = 2
  density = 1
  expand = 3
  formula = Tc
  name = G4_Tc
  specific = 4
FEATURE [App::DocumentObjectGroupPython] Ru_element001  label="Ru_element : 1"  # scripted group (container) (typed FeaturePython)
  n = 1
  ref = Ru_element
FEATURE [App::DocumentObjectGroupPython] G4_Ru  # scripted group (container) (typed FeaturePython)
  Dunit = g/cm3
  Dvalue = 12.41
  Group = -> [Ru_element001]
  conduct = 2
  density = 1
  expand = 3
  formula = Ru
  name = G4_Ru
  specific = 4
FEATURE [App::DocumentObjectGroupPython] Rh_element001  label="Rh_element : 1"  # scripted group (container) (typed FeaturePython)
  n = 1
  ref = Rh_element
FEATURE [App::DocumentObjectGroupPython] G4_Rh  # scripted group (container) (typed FeaturePython)
  Dunit = g/cm3
  Dvalue = 12.41
  Group = -> [Rh_element001]
  conduct = 2
  density = 1
  expand = 3
  formula = Rh
  name = G4_Rh
  specific = 4
FEATURE [App::DocumentObjectGroupPython] Pd_element001  label="Pd_element : 1"  # scripted group (container) (typed FeaturePython)
  n = 1
  ref = Pd_element
FEATURE [App::DocumentObjectGroupPython] G4_Pd  # scripted group (container) (typed FeaturePython)
  Dunit = g/cm3
  Dvalue = 12.02
  Group = -> [Pd_element001]
  conduct = 2
  density = 1
  expand = 3
  formula = Pd
  name = G4_Pd
  specific = 4
FEATURE [App::DocumentObjectGroupPython] Ag_element006  label="Ag_element : 004"  # scripted group (container) (typed FeaturePython)
  n = 1
  ref = Ag_element
FEATURE [App::DocumentObjectGroupPython] G4_Ag  # scripted group (container) (typed FeaturePython)
  Dunit = g/cm3
  Dvalue = 10.5
  Group = -> [Ag_element006]
  conduct = 2
  density = 1
  expand = 3
  formula = Ag
  name = G4_Ag
  specific = 4
FEATURE [App::DocumentObjectGroupPython] Cd_element003  label="Cd_element : 003"  # scripted group (container) (typed FeaturePython)
  n = 1
  ref = Cd_element
FEATURE [App::DocumentObjectGroupPython] G4_Cd  # scripted group (container) (typed FeaturePython)
  Dunit = g/cm3
  Dvalue = 8.65
  Group = -> [Cd_element003]
  conduct = 2
  density = 1
  expand = 3
  formula = Cd
  name = G4_Cd
  specific = 4
FEATURE [App::DocumentObjectGroupPython] In_element001  label="In_element : 1"  # scripted group (container) (typed FeaturePython)
  n = 1
  ref = In_element
FEATURE [App::DocumentObjectGroupPython] G4_In  # scripted group (container) (typed FeaturePython)
  Dunit = g/cm3
  Dvalue = 7.31
  Group = -> [In_element001]
  conduct = 2
  density = 1
  expand = 3
  formula = In
  name = G4_In
  specific = 4
FEATURE [App::DocumentObjectGroupPython] Sn_element001  label="Sn_element : 1"  # scripted group (container) (typed FeaturePython)
  n = 1
  ref = Sn_element
FEATURE [App::DocumentObjectGroupPython] G4_Sn  # scripted group (container) (typed FeaturePython)
  Dunit = g/cm3
  Dvalue = 7.31
  Group = -> [Sn_element001]
  conduct = 2
  density = 1
  expand = 3
  formula = Sn
  name = G4_Sn
  specific = 4
FEATURE [App::DocumentObjectGroupPython] Sb_element001  label="Sb_element : 1"  # scripted group (container) (typed FeaturePython)
  n = 1
  ref = Sb_element
FEATURE [App::DocumentObjectGroupPython] G4_Sb  # scripted group (container) (typed FeaturePython)
  Dunit = g/cm3
  Dvalue = 6.691
  Group = -> [Sb_element001]
  conduct = 2
  density = 1
  expand = 3
  formula = Sb
  name = G4_Sb
  specific = 4
FEATURE [App::DocumentObjectGroupPython] Te_element002  label="Te_element : 002"  # scripted group (container) (typed FeaturePython)
  n = 1
  ref = Te_element
FEATURE [App::DocumentObjectGroupPython] G4_Te  # scripted group (container) (typed FeaturePython)
  Dunit = g/cm3
  Dvalue = 6.24
  Group = -> [Te_element002]
  conduct = 2
  density = 1
  expand = 3
  formula = Te
  name = G4_Te
  specific = 4
FEATURE [App::DocumentObjectGroupPython] I_element010  label="I_element : 006"  # scripted group (container) (typed FeaturePython)
  n = 1
  ref = I_element
FEATURE [App::DocumentObjectGroupPython] G4_I  # scripted group (container) (typed FeaturePython)
  Dunit = g/cm3
  Dvalue = 4.93
  Group = -> [I_element010]
  conduct = 2
  density = 1
  expand = 3
  formula = I
  name = G4_I
  specific = 4
FEATURE [App::DocumentObjectGroupPython] Xe_element001  label="Xe_element : 1"  # scripted group (container) (typed FeaturePython)
  n = 1
  ref = Xe_element
FEATURE [App::DocumentObjectGroupPython] G4_Xe  # scripted group (container) (typed FeaturePython)
  Dunit = g/cm3
  Dvalue = 0.00548536
  Group = -> [Xe_element001]
  conduct = 2
  density = 1
  expand = 3
  formula = Xe
  name = G4_Xe
  specific = 4
FEATURE [App::DocumentObjectGroupPython] Cs_element003  label="Cs_element : 003"  # scripted group (container) (typed FeaturePython)
  n = 1
  ref = Cs_element
FEATURE [App::DocumentObjectGroupPython] G4_Cs  # scripted group (container) (typed FeaturePython)
  Dunit = g/cm3
  Dvalue = 1.873
  Group = -> [Cs_element003]
  conduct = 2
  density = 1
  expand = 3
  formula = Cs
  name = G4_Cs
  specific = 4
FEATURE [App::DocumentObjectGroupPython] Ba_element003  label="Ba_element : 003"  # scripted group (container) (typed FeaturePython)
  n = 1
  ref = Ba_element
FEATURE [App::DocumentObjectGroupPython] G4_Ba  # scripted group (container) (typed FeaturePython)
  Dunit = g/cm3
  Dvalue = 3.5
  Group = -> [Ba_element003]
  conduct = 2
  density = 1
  expand = 3
  formula = Ba
  name = G4_Ba
  specific = 4
FEATURE [App::DocumentObjectGroupPython] La_element003  label="La_element : 003"  # scripted group (container) (typed FeaturePython)
  n = 1
  ref = La_element
FEATURE [App::DocumentObjectGroupPython] G4_La  # scripted group (container) (typed FeaturePython)
  Dunit = g/cm3
  Dvalue = 6.154
  Group = -> [La_element003]
  conduct = 2
  density = 1
  expand = 3
  formula = La
  name = G4_La
  specific = 4
FEATURE [App::DocumentObjectGroupPython] Ce_element002  label="Ce_element : 1"  # scripted group (container) (typed FeaturePython)
  n = 1
  ref = Ce_element
FEATURE [App::DocumentObjectGroupPython] G4_Ce  # scripted group (container) (typed FeaturePython)
  Dunit = g/cm3
  Dvalue = 6.657
  Group = -> [Ce_element002]
  conduct = 2
  density = 1
  expand = 3
  formula = Ce
  name = G4_Ce
  specific = 4
FEATURE [App::DocumentObjectGroupPython] Pr_element001  label="Pr_element : 1"  # scripted group (container) (typed FeaturePython)
  n = 1
  ref = Pr_element
FEATURE [App::DocumentObjectGroupPython] G4_Pr  # scripted group (container) (typed FeaturePython)
  Dunit = g/cm3
  Dvalue = 6.71
  Group = -> [Pr_element001]
  conduct = 2
  density = 1
  expand = 3
  formula = Pr
  name = G4_Pr
  specific = 4
FEATURE [App::DocumentObjectGroupPython] Nd_element001  label="Nd_element : 1"  # scripted group (container) (typed FeaturePython)
  n = 1
  ref = Nd_element
FEATURE [App::DocumentObjectGroupPython] G4_Nd  # scripted group (container) (typed FeaturePython)
  Dunit = g/cm3
  Dvalue = 6.9
  Group = -> [Nd_element001]
  conduct = 2
  density = 1
  expand = 3
  formula = Nd
  name = G4_Nd
  specific = 4
FEATURE [App::DocumentObjectGroupPython] Pm_element001  label="Pm_element : 1"  # scripted group (container) (typed FeaturePython)
  n = 1
  ref = Pm_element
FEATURE [App::DocumentObjectGroupPython] G4_Pm  # scripted group (container) (typed FeaturePython)
  Dunit = g/cm3
  Dvalue = 7.22
  Group = -> [Pm_element001]
  conduct = 2
  density = 1
  expand = 3
  formula = Pm
  name = G4_Pm
  specific = 4
FEATURE [App::DocumentObjectGroupPython] Sm_element001  label="Sm_element : 1"  # scripted group (container) (typed FeaturePython)
  n = 1
  ref = Sm_element
FEATURE [App::DocumentObjectGroupPython] G4_Sm  # scripted group (container) (typed FeaturePython)
  Dunit = g/cm3
  Dvalue = 7.46
  Group = -> [Sm_element001]
  conduct = 2
  density = 1
  expand = 3
  formula = Sm
  name = G4_Sm
  specific = 4
FEATURE [App::DocumentObjectGroupPython] Eu_element001  label="Eu_element : 1"  # scripted group (container) (typed FeaturePython)
  n = 1
  ref = Eu_element
FEATURE [App::DocumentObjectGroupPython] G4_Eu  # scripted group (container) (typed FeaturePython)
  Dunit = g/cm3
  Dvalue = 5.243
  Group = -> [Eu_element001]
  conduct = 2
  density = 1
  expand = 3
  formula = Eu
  name = G4_Eu
  specific = 4
FEATURE [App::DocumentObjectGroupPython] Gd_element002  label="Gd_element : 1"  # scripted group (container) (typed FeaturePython)
  n = 1
  ref = Gd_element
FEATURE [App::DocumentObjectGroupPython] G4_Gd  # scripted group (container) (typed FeaturePython)
  Dunit = g/cm3
  Dvalue = 7.9004
  Group = -> [Gd_element002]
  conduct = 2
  density = 1
  expand = 3
  formula = Gd
  name = G4_Gd
  specific = 4
FEATURE [App::DocumentObjectGroupPython] Tb_element001  label="Tb_element : 1"  # scripted group (container) (typed FeaturePython)
  n = 1
  ref = Tb_element
FEATURE [App::DocumentObjectGroupPython] G4_Tb  # scripted group (container) (typed FeaturePython)
  Dunit = g/cm3
  Dvalue = 8.229
  Group = -> [Tb_element001]
  conduct = 2
  density = 1
  expand = 3
  formula = Tb
  name = G4_Tb
  specific = 4
FEATURE [App::DocumentObjectGroupPython] Dy_element001  label="Dy_element : 1"  # scripted group (container) (typed FeaturePython)
  n = 1
  ref = Dy_element
FEATURE [App::DocumentObjectGroupPython] G4_Dy  # scripted group (container) (typed FeaturePython)
  Dunit = g/cm3
  Dvalue = 8.55
  Group = -> [Dy_element001]
  conduct = 2
  density = 1
  expand = 3
  formula = Dy
  name = G4_Dy
  specific = 4
FEATURE [App::DocumentObjectGroupPython] Ho_element001  label="Ho_element : 1"  # scripted group (container) (typed FeaturePython)
  n = 1
  ref = Ho_element
FEATURE [App::DocumentObjectGroupPython] G4_Ho  # scripted group (container) (typed FeaturePython)
  Dunit = g/cm3
  Dvalue = 8.795
  Group = -> [Ho_element001]
  conduct = 2
  density = 1
  expand = 3
  formula = Ho
  name = G4_Ho
  specific = 4
FEATURE [App::DocumentObjectGroupPython] Er_element001  label="Er_element : 1"  # scripted group (container) (typed FeaturePython)
  n = 1
  ref = Er_element
FEATURE [App::DocumentObjectGroupPython] G4_Er  # scripted group (container) (typed FeaturePython)
  Dunit = g/cm3
  Dvalue = 9.066
  Group = -> [Er_element001]
  conduct = 2
  density = 1
  expand = 3
  formula = Er
  name = G4_Er
  specific = 4
FEATURE [App::DocumentObjectGroupPython] Tm_element001  label="Tm_element : 1"  # scripted group (container) (typed FeaturePython)
  n = 1
  ref = Tm_element
FEATURE [App::DocumentObjectGroupPython] G4_Tm  # scripted group (container) (typed FeaturePython)
  Dunit = g/cm3
  Dvalue = 9.321
  Group = -> [Tm_element001]
  conduct = 2
  density = 1
  expand = 3
  formula = Tm
  name = G4_Tm
  specific = 4
FEATURE [App::DocumentObjectGroupPython] Yb_element001  label="Yb_element : 1"  # scripted group (container) (typed FeaturePython)
  n = 1
  ref = Yb_element
FEATURE [App::DocumentObjectGroupPython] G4_Yb  # scripted group (container) (typed FeaturePython)
  Dunit = g/cm3
  Dvalue = 6.73
  Group = -> [Yb_element001]
  conduct = 2
  density = 1
  expand = 3
  formula = Yb
  name = G4_Yb
  specific = 4
FEATURE [App::DocumentObjectGroupPython] Lu_element001  label="Lu_element : 1"  # scripted group (container) (typed FeaturePython)
  n = 1
  ref = Lu_element
FEATURE [App::DocumentObjectGroupPython] G4_Lu  # scripted group (container) (typed FeaturePython)
  Dunit = g/cm3
  Dvalue = 9.84
  Group = -> [Lu_element001]
  conduct = 2
  density = 1
  expand = 3
  formula = Lu
  name = G4_Lu
  specific = 4
FEATURE [App::DocumentObjectGroupPython] Hf_element001  label="Hf_element : 1"  # scripted group (container) (typed FeaturePython)
  n = 1
  ref = Hf_element
FEATURE [App::DocumentObjectGroupPython] G4_Hf  # scripted group (container) (typed FeaturePython)
  Dunit = g/cm3
  Dvalue = 13.31
  Group = -> [Hf_element001]
  conduct = 2
  density = 1
  expand = 3
  formula = Hf
  name = G4_Hf
  specific = 4
FEATURE [App::DocumentObjectGroupPython] Ta_element001  label="Ta_element : 1"  # scripted group (container) (typed FeaturePython)
  n = 1
  ref = Ta_element
FEATURE [App::DocumentObjectGroupPython] G4_Ta  # scripted group (container) (typed FeaturePython)
  Dunit = g/cm3
  Dvalue = 16.654
  Group = -> [Ta_element001]
  conduct = 2
  density = 1
  expand = 3
  formula = Ta
  name = G4_Ta
  specific = 4
FEATURE [App::DocumentObjectGroupPython] W_element004  label="W_element : 004"  # scripted group (container) (typed FeaturePython)
  n = 1
  ref = W_element
FEATURE [App::DocumentObjectGroupPython] G4_W  # scripted group (container) (typed FeaturePython)
  Dunit = g/cm3
  Dvalue = 19.3
  Group = -> [W_element004]
  conduct = 2
  density = 1
  expand = 3
  formula = W
  name = G4_W
  specific = 4
FEATURE [App::DocumentObjectGroupPython] Re_element001  label="Re_element : 1"  # scripted group (container) (typed FeaturePython)
  n = 1
  ref = Re_element
FEATURE [App::DocumentObjectGroupPython] G4_Re  # scripted group (container) (typed FeaturePython)
  Dunit = g/cm3
  Dvalue = 21.02
  Group = -> [Re_element001]
  conduct = 2
  density = 1
  expand = 3
  formula = Re
  name = G4_Re
  specific = 4
FEATURE [App::DocumentObjectGroupPython] Os_element001  label="Os_element : 1"  # scripted group (container) (typed FeaturePython)
  n = 1
  ref = Os_element
FEATURE [App::DocumentObjectGroupPython] G4_Os  # scripted group (container) (typed FeaturePython)
  Dunit = g/cm3
  Dvalue = 22.57
  Group = -> [Os_element001]
  conduct = 2
  density = 1
  expand = 3
  formula = Os
  name = G4_Os
  specific = 4
FEATURE [App::DocumentObjectGroupPython] Ir_element001  label="Ir_element : 1"  # scripted group (container) (typed FeaturePython)
  n = 1
  ref = Ir_element
FEATURE [App::DocumentObjectGroupPython] G4_Ir  # scripted group (container) (typed FeaturePython)
  Dunit = g/cm3
  Dvalue = 22.42
  Group = -> [Ir_element001]
  conduct = 2
  density = 1
  expand = 3
  formula = Ir
  name = G4_Ir
  specific = 4
FEATURE [App::DocumentObjectGroupPython] Pt_element001  label="Pt_element : 1"  # scripted group (container) (typed FeaturePython)
  n = 1
  ref = Pt_element
FEATURE [App::DocumentObjectGroupPython] G4_Pt  # scripted group (container) (typed FeaturePython)
  Dunit = g/cm3
  Dvalue = 21.45
  Group = -> [Pt_element001]
  conduct = 2
  density = 1
  expand = 3
  formula = Pt
  name = G4_Pt
  specific = 4
FEATURE [App::DocumentObjectGroupPython] Au_element001  label="Au_element : 1"  # scripted group (container) (typed FeaturePython)
  n = 1
  ref = Au_element
FEATURE [App::DocumentObjectGroupPython] G4_Au  # scripted group (container) (typed FeaturePython)
  Dunit = g/cm3
  Dvalue = 19.32
  Group = -> [Au_element001]
  conduct = 2
  density = 1
  expand = 3
  formula = Au
  name = G4_Au
  specific = 4
FEATURE [App::DocumentObjectGroupPython] Hg_element002  label="Hg_element : 002"  # scripted group (container) (typed FeaturePython)
  n = 1
  ref = Hg_element
FEATURE [App::DocumentObjectGroupPython] G4_Hg  # scripted group (container) (typed FeaturePython)
  Dunit = g/cm3
  Dvalue = 13.546
  Group = -> [Hg_element002]
  conduct = 2
  density = 1
  expand = 3
  formula = Hg
  name = G4_Hg
  specific = 4
FEATURE [App::DocumentObjectGroupPython] Tl_element002  label="Tl_element : 002"  # scripted group (container) (typed FeaturePython)
  n = 1
  ref = Tl_element
FEATURE [App::DocumentObjectGroupPython] G4_Tl  # scripted group (container) (typed FeaturePython)
  Dunit = g/cm3
  Dvalue = 11.72
  Group = -> [Tl_element002]
  conduct = 2
  density = 1
  expand = 3
  formula = Tl
  name = G4_Tl
  specific = 4
FEATURE [App::DocumentObjectGroupPython] Pb_element003  label="Pb_element : 1"  # scripted group (container) (typed FeaturePython)
  n = 1
  ref = Pb_element
FEATURE [App::DocumentObjectGroupPython] G4_Pb  # scripted group (container) (typed FeaturePython)
  Dunit = g/cm3
  Dvalue = 11.35
  Group = -> [Pb_element003]
  conduct = 2
  density = 1
  expand = 3
  formula = Pb
  name = G4_Pb
  specific = 4
FEATURE [App::DocumentObjectGroupPython] Bi_element002  label="Bi_element : 1"  # scripted group (container) (typed FeaturePython)
  n = 1
  ref = Bi_element
FEATURE [App::DocumentObjectGroupPython] G4_Bi  # scripted group (container) (typed FeaturePython)
  Dunit = g/cm3
  Dvalue = 9.747
  Group = -> [Bi_element002]
  conduct = 2
  density = 1
  expand = 3
  formula = Bi
  name = G4_Bi
  specific = 4
FEATURE [App::DocumentObjectGroupPython] Po_element001  label="Po_element : 1"  # scripted group (container) (typed FeaturePython)
  n = 1
  ref = Po_element
FEATURE [App::DocumentObjectGroupPython] G4_Po  # scripted group (container) (typed FeaturePython)
  Dunit = g/cm3
  Dvalue = 9.32
  Group = -> [Po_element001]
  conduct = 2
  density = 1
  expand = 3
  formula = Po
  name = G4_Po
  specific = 4
FEATURE [App::DocumentObjectGroupPython] At_element001  label="At_element : 1"  # scripted group (container) (typed FeaturePython)
  n = 1
  ref = At_element
FEATURE [App::DocumentObjectGroupPython] G4_At  # scripted group (container) (typed FeaturePython)
  Dunit = g/cm3
  Dvalue = 9.32
  Group = -> [At_element001]
  conduct = 2
  density = 1
  expand = 3
  formula = At
  name = G4_At
  specific = 4
FEATURE [App::DocumentObjectGroupPython] Rn_element001  label="Rn_element : 1"  # scripted group (container) (typed FeaturePython)
  n = 1
  ref = Rn_element
FEATURE [App::DocumentObjectGroupPython] G4_Rn  # scripted group (container) (typed FeaturePython)
  Dunit = g/cm3
  Dvalue = 0.00900662
  Group = -> [Rn_element001]
  conduct = 2
  density = 1
  expand = 3
  formula = Rn
  name = G4_Rn
  specific = 4
FEATURE [App::DocumentObjectGroupPython] Fr_element001  label="Fr_element : 1"  # scripted group (container) (typed FeaturePython)
  n = 1
  ref = Fr_element
FEATURE [App::DocumentObjectGroupPython] G4_Fr  # scripted group (container) (typed FeaturePython)
  Dunit = g/cm3
  Dvalue = 1
  Group = -> [Fr_element001]
  conduct = 2
  density = 1
  expand = 3
  formula = Fr
  name = G4_Fr
  specific = 4
FEATURE [App::DocumentObjectGroupPython] Ra_element001  label="Ra_element : 1"  # scripted group (container) (typed FeaturePython)
  n = 1
  ref = Ra_element
FEATURE [App::DocumentObjectGroupPython] G4_Ra  # scripted group (container) (typed FeaturePython)
  Dunit = g/cm3
  Dvalue = 5
  Group = -> [Ra_element001]
  conduct = 2
  density = 1
  expand = 3
  formula = Ra
  name = G4_Ra
  specific = 4
FEATURE [App::DocumentObjectGroupPython] Ac_element001  label="Ac_element : 1"  # scripted group (container) (typed FeaturePython)
  n = 1
  ref = Ac_element
FEATURE [App::DocumentObjectGroupPython] G4_Ac  # scripted group (container) (typed FeaturePython)
  Dunit = g/cm3
  Dvalue = 10.07
  Group = -> [Ac_element001]
  conduct = 2
  density = 1
  expand = 3
  formula = Ac
  name = G4_Ac
  specific = 4
FEATURE [App::DocumentObjectGroupPython] Th_element001  label="Th_element : 1"  # scripted group (container) (typed FeaturePython)
  n = 1
  ref = Th_element
FEATURE [App::DocumentObjectGroupPython] G4_Th  # scripted group (container) (typed FeaturePython)
  Dunit = g/cm3
  Dvalue = 11.72
  Group = -> [Th_element001]
  conduct = 2
  density = 1
  expand = 3
  formula = Th
  name = G4_Th
  specific = 4
FEATURE [App::DocumentObjectGroupPython] Pa_element001  label="Pa_element : 1"  # scripted group (container) (typed FeaturePython)
  n = 1
  ref = Pa_element
FEATURE [App::DocumentObjectGroupPython] G4_Pa  # scripted group (container) (typed FeaturePython)
  Dunit = g/cm3
  Dvalue = 15.37
  Group = -> [Pa_element001]
  conduct = 2
  density = 1
  expand = 3
  formula = Pa
  name = G4_Pa
  specific = 4
FEATURE [App::DocumentObjectGroupPython] U_element004  label="U_element : 004"  # scripted group (container) (typed FeaturePython)
  n = 1
  ref = U_element
FEATURE [App::DocumentObjectGroupPython] G4_U  # scripted group (container) (typed FeaturePython)
  Dunit = g/cm3
  Dvalue = 18.95
  Group = -> [U_element004]
  conduct = 2
  density = 1
  expand = 3
  formula = U
  name = G4_U
  specific = 4
FEATURE [App::DocumentObjectGroupPython] Np_element001  label="Np_element : 1"  # scripted group (container) (typed FeaturePython)
  n = 1
  ref = Np_element
FEATURE [App::DocumentObjectGroupPython] G4_Np  # scripted group (container) (typed FeaturePython)
  Dunit = g/cm3
  Dvalue = 20.25
  Group = -> [Np_element001]
  conduct = 2
  density = 1
  expand = 3
  formula = Np
  name = G4_Np
  specific = 4
FEATURE [App::DocumentObjectGroupPython] Pu_element002  label="Pu_element : 002"  # scripted group (container) (typed FeaturePython)
  n = 1
  ref = Pu_element
FEATURE [App::DocumentObjectGroupPython] G4_Pu  # scripted group (container) (typed FeaturePython)
  Dunit = g/cm3
  Dvalue = 19.84
  Group = -> [Pu_element002]
  conduct = 2
  density = 1
  expand = 3
  formula = Pu
  name = G4_Pu
  specific = 4
FEATURE [App::DocumentObjectGroupPython] Am_element001  label="Am_element : 1"  # scripted group (container) (typed FeaturePython)
  n = 1
  ref = Am_element
FEATURE [App::DocumentObjectGroupPython] G4_Am  # scripted group (container) (typed FeaturePython)
  Dunit = g/cm3
  Dvalue = 13.67
  Group = -> [Am_element001]
  conduct = 2
  density = 1
  expand = 3
  formula = Am
  name = G4_Am
  specific = 4
FEATURE [App::DocumentObjectGroupPython] Cm_element001  label="Cm_element : 1"  # scripted group (container) (typed FeaturePython)
  n = 1
  ref = Cm_element
FEATURE [App::DocumentObjectGroupPython] G4_Cm  # scripted group (container) (typed FeaturePython)
  Dunit = g/cm3
  Dvalue = 13.51
  Group = -> [Cm_element001]
  conduct = 2
  density = 1
  expand = 3
  formula = Cm
  name = G4_Cm
  specific = 4
FEATURE [App::DocumentObjectGroupPython] Bk_element001  label="Bk_element : 1"  # scripted group (container) (typed FeaturePython)
  n = 1
  ref = Bk_element
FEATURE [App::DocumentObjectGroupPython] G4_Bk  # scripted group (container) (typed FeaturePython)
  Dunit = g/cm3
  Dvalue = 14
  Group = -> [Bk_element001]
  conduct = 2
  density = 1
  expand = 3
  formula = Bk
  name = G4_Bk
  specific = 4
FEATURE [App::DocumentObjectGroupPython] Cf_element001  label="Cf_element : 1"  # scripted group (container) (typed FeaturePython)
  n = 1
  ref = Cf_element
FEATURE [App::DocumentObjectGroupPython] G4_Cf  # scripted group (container) (typed FeaturePython)
  Dunit = g/cm3
  Dvalue = 10
  Group = -> [Cf_element001]
  conduct = 2
  density = 1
  expand = 3
  formula = Cf
  name = G4_Cf
  specific = 4
FEATURE [App::DocumentObjectGroupPython] Element  # scripted group (container) (typed FeaturePython)
  Group = -> [G4_H,G4_He,G4_Li,G4_Be,G4_B,G4_C,G4_N,G4_O,G4_F,G4_Ne,G4_Na,G4_Mg,G4_Al,G4_Si,G4_P,G4_S,G4_Cl,G4_Ar,G4_K,G4_Ca,G4_Sc,G4_Ti,G4_V,G4_Cr,G4_Mn,G4_Fe,G4_Co,G4_Ni,G4_Cu,G4_Zn,G4_Ga,G4_Ge,G4_As,G4_Se,G4_Br,G4_Kr,G4_Rb,G4_Sr,G4_Y,G4_Zr,G4_Nb,G4_Mo,G4_Tc,G4_Ru,G4_Rh,G4_Pd,G4_Ag,G4_Cd,G4_In,G4_Sn,G4_Sb,G4_Te,G4_I,G4_Xe,G4_Cs,G4_Ba,G4_La,G4_Ce,G4_Pr,G4_Nd,G4_Pm,G4_Sm,G4_Eu,G4_Gd,G4_Tb,G4_Dy,G4_Ho,G4_Er,+30 more]
FEATURE [App::DocumentObjectGroupPython] H_element114  label="H_element : 063"  # scripted group (container) (typed FeaturePython)
  n = 2
  ref = H_element
FEATURE [App::DocumentObjectGroupPython] G4_lH2  # scripted group (container) (typed FeaturePython)
  Dunit = g/cm3
  Dvalue = 0.0708
  Group = -> [H_element114]
  conduct = 2
  density = 1
  expand = 3
  formula = G4_lH2
  name = G4_lH2
  specific = 4
FEATURE [App::DocumentObjectGroupPython] N_element049  label="N_element : 022"  # scripted group (container) (typed FeaturePython)
  n = 2
  ref = N_element
FEATURE [App::DocumentObjectGroupPython] G4_lN2  # scripted group (container) (typed FeaturePython)
  Dunit = g/cm3
  Dvalue = 0.807
  Group = -> [N_element049]
  conduct = 2
  density = 1
  expand = 3
  formula = G4_lN2
  name = G4_lN2
  specific = 4
FEATURE [App::DocumentObjectGroupPython] O_element106  label="O_element : 060"  # scripted group (container) (typed FeaturePython)
  n = 2
  ref = O_element
FEATURE [App::DocumentObjectGroupPython] G4_lO2  # scripted group (container) (typed FeaturePython)
  Dunit = g/cm3
  Dvalue = 1.141
  Group = -> [O_element106]
  conduct = 2
  density = 1
  expand = 3
  formula = G4_lO2
  name = G4_lO2
  specific = 4
FEATURE [App::DocumentObjectGroupPython] Ar  label="Ar : 1"  # scripted group (container) (typed FeaturePython)
  n = 1
  ref = Ar
FEATURE [App::DocumentObjectGroupPython] G4_lAr  # scripted group (container) (typed FeaturePython)
  Dunit = g/cm3
  Dvalue = 1.396
  Group = -> [Ar]
  conduct = 2
  density = 1
  expand = 3
  formula = G4_lAr
  name = G4_lAr
  specific = 4
FEATURE [App::DocumentObjectGroupPython] Br  label="Br : 1"  # scripted group (container) (typed FeaturePython)
  n = 1
  ref = Br
FEATURE [App::DocumentObjectGroupPython] G4_lBr  # scripted group (container) (typed FeaturePython)
  Dunit = g/cm3
  Dvalue = 3.1028
  Group = -> [Br]
  conduct = 2
  density = 1
  expand = 3
  formula = G4_lBr
  name = G4_lBr
  specific = 4
FEATURE [App::DocumentObjectGroupPython] Kr  label="Kr : 1"  # scripted group (container) (typed FeaturePython)
  n = 1
  ref = Kr
FEATURE [App::DocumentObjectGroupPython] G4_lKr  # scripted group (container) (typed FeaturePython)
  Dunit = g/cm3
  Dvalue = 2.418
  Group = -> [Kr]
  conduct = 2
  density = 1
  expand = 3
  formula = G4_lKr
  name = G4_lKr
  specific = 4
FEATURE [App::DocumentObjectGroupPython] Xe  label="Xe : 1"  # scripted group (container) (typed FeaturePython)
  n = 1
  ref = Xe
FEATURE [App::DocumentObjectGroupPython] G4_lXe  # scripted group (container) (typed FeaturePython)
  Dunit = g/cm3
  Dvalue = 2.953
  Group = -> [Xe]
  conduct = 2
  density = 1
  expand = 3
  formula = G4_lXe
  name = G4_lXe
  specific = 4
FEATURE [App::DocumentObjectGroupPython] O_element107  label="O_element : 061"  # scripted group (container) (typed FeaturePython)
  n = 4
  ref = O_element
FEATURE [App::DocumentObjectGroupPython] Pb_element004  label="Pb_element : 002"  # scripted group (container) (typed FeaturePython)
  n = 1
  ref = Pb_element
FEATURE [App::DocumentObjectGroupPython] W_element005  label="W_element : 005"  # scripted group (container) (typed FeaturePython)
  n = 1
  ref = W_element
FEATURE [App::DocumentObjectGroupPython] G4_PbWO4  # scripted group (container) (typed FeaturePython)
  Dunit = g/cm3
  Dvalue = 8.28
  Group = -> [O_element107,Pb_element004,W_element005]
  conduct = 2
  density = 1
  expand = 3
  formula = G4_PbWO4
  name = G4_PbWO4
  specific = 4
FEATURE [App::DocumentObjectGroupPython] alactic  label="alactic : 1"  # scripted group (container) (typed FeaturePython)
  n = 1
  ref = alactic
FEATURE [App::DocumentObjectGroupPython] G4_Galactic  # scripted group (container) (typed FeaturePython)
  Dunit = g/cm3
  Dvalue = 0
  Group = -> [alactic]
  conduct = 2
  density = 1
  expand = 3
  formula = G4_Galactic
  name = G4_Galactic
  specific = 4
FEATURE [App::DocumentObjectGroupPython] RAPHITE_POROUS  label="RAPHITE_POROUS : 1"  # scripted group (container) (typed FeaturePython)
  n = 1
  ref = RAPHITE_POROUS
FEATURE [App::DocumentObjectGroupPython] G4_GRAPHITE_POROUS  # scripted group (container) (typed FeaturePython)
  Dunit = g/cm3
  Dvalue = 1.7
  Group = -> [RAPHITE_POROUS]
  conduct = 2
  density = 1
  expand = 3
  formula = G4_GRAPHITE_POROUS
  name = G4_GRAPHITE_POROUS
  specific = 4
FEATURE [App::DocumentObjectGroupPython] H_element115  label="H_element : 0.150"  # scripted group (container) (typed FeaturePython)
  n = 0.080538
FEATURE [App::DocumentObjectGroupPython] C_element125  label="C_element : 0.600"  # scripted group (container) (typed FeaturePython)
  n = 0.599848
FEATURE [App::DocumentObjectGroupPython] O_element108  label="O_element : 0.320"  # scripted group (container) (typed FeaturePython)
  n = 0.319614
FEATURE [App::DocumentObjectGroupPython] G4_LUCITE  # scripted group (container) (typed FeaturePython)
  Dunit = g/cm3
  Dvalue = 1.19
  Group = -> [H_element115,C_element125,O_element108]
  conduct = 2
  density = 1
  expand = 3
  formula = G4_LUCITE
  name = G4_LUCITE
  specific = 4
FEATURE [App::DocumentObjectGroupPython] Cu_element002  label="Cu_element : 62"  # scripted group (container) (typed FeaturePython)
  n = 62
  ref = Cu_element
FEATURE [App::DocumentObjectGroupPython] Zn_element002  label="Zn_element : 35"  # scripted group (container) (typed FeaturePython)
  n = 35
  ref = Zn_element
FEATURE [App::DocumentObjectGroupPython] Pb_element005  label="Pb_element : 3"  # scripted group (container) (typed FeaturePython)
  n = 3
  ref = Pb_element
FEATURE [App::DocumentObjectGroupPython] G4_BRASS  # scripted group (container) (typed FeaturePython)
  Dunit = g/cm3
  Dvalue = 8.52
  Group = -> [Cu_element002,Zn_element002,Pb_element005]
  conduct = 2
  density = 1
  expand = 3
  formula = G4_BRASS
  name = G4_BRASS
  specific = 4
FEATURE [App::DocumentObjectGroupPython] Cu_element003  label="Cu_element : 89"  # scripted group (container) (typed FeaturePython)
  n = 89
  ref = Cu_element
FEATURE [App::DocumentObjectGroupPython] Zn_element003  label="Zn_element : 9"  # scripted group (container) (typed FeaturePython)
  n = 9
  ref = Zn_element
FEATURE [App::DocumentObjectGroupPython] Pb_element006  label="Pb_element : 2"  # scripted group (container) (typed FeaturePython)
  n = 2
  ref = Pb_element
FEATURE [App::DocumentObjectGroupPython] G4_BRONZE  # scripted group (container) (typed FeaturePython)
  Dunit = g/cm3
  Dvalue = 8.82
  Group = -> [Cu_element003,Zn_element003,Pb_element006]
  conduct = 2
  density = 1
  expand = 3
  formula = G4_BRONZE
  name = G4_BRONZE
  specific = 4
FEATURE [App::DocumentObjectGroupPython] Fe_element008  label="Fe_element : 74"  # scripted group (container) (typed FeaturePython)
  n = 74
  ref = Fe_element
FEATURE [App::DocumentObjectGroupPython] Cr_element002  label="Cr_element : 18"  # scripted group (container) (typed FeaturePython)
  n = 18
  ref = Cr_element
FEATURE [App::DocumentObjectGroupPython] Ni_element002  label="Ni_element : 8"  # scripted group (container) (typed FeaturePython)
  n = 8
  ref = Ni_element
FEATURE [App::DocumentObjectGroupPython] G4_STAINLESS_STEEL  label="G4_STAINLESS-STEEL"  # scripted group (container) (typed FeaturePython)
  Dunit = g/cm3
  Dvalue = 8
  Group = -> [Fe_element008,Cr_element002,Ni_element002]
  conduct = 2
  density = 1
  expand = 3
  formula = G4_STAINLESS-STEEL
  name = G4_STAINLESS-STEEL
  specific = 4
FEATURE [App::DocumentObjectGroupPython] H_element116  label="H_element : 064"  # scripted group (container) (typed FeaturePython)
  n = 18
  ref = H_element
FEATURE [App::DocumentObjectGroupPython] C_element126  label="C_element : 071"  # scripted group (container) (typed FeaturePython)
  n = 12
  ref = C_element
FEATURE [App::DocumentObjectGroupPython] O_element109  label="O_element : 062"  # scripted group (container) (typed FeaturePython)
  n = 7
  ref = O_element
FEATURE [App::DocumentObjectGroupPython] G4_CR39  # scripted group (container) (typed FeaturePython)
  Dunit = g/cm3
  Dvalue = 1.32
  Group = -> [H_element116,C_element126,O_element109]
  conduct = 2
  density = 1
  expand = 3
  formula = G4_CR39
  name = G4_CR39
  specific = 4
FEATURE [App::DocumentObjectGroupPython] H_element117  label="H_element : 38"  # scripted group (container) (typed FeaturePython)
  n = 38
  ref = H_element
FEATURE [App::DocumentObjectGroupPython] C_element127  label="C_element : 072"  # scripted group (container) (typed FeaturePython)
  n = 18
  ref = C_element
FEATURE [App::DocumentObjectGroupPython] O_element110  label="O_element : 063"  # scripted group (container) (typed FeaturePython)
  n = 1
  ref = O_element
FEATURE [App::DocumentObjectGroupPython] G4_OCTADECANOL  # scripted group (container) (typed FeaturePython)
  Dunit = g/cm3
  Dvalue = 0.812
  Group = -> [H_element117,C_element127,O_element110]
  conduct = 2
  density = 1
  expand = 3
  formula = G4_OCTADECANOL
  name = G4_OCTADECANOL
  specific = 4
FEATURE [App::DocumentObjectGroupPython] HEP  # scripted group (container) (typed FeaturePython)
  Group = -> [G4_lH2,G4_lN2,G4_lO2,G4_lAr,G4_lBr,G4_lKr,G4_lXe,G4_PbWO4,G4_Galactic,G4_GRAPHITE_POROUS,G4_LUCITE,G4_BRASS,G4_BRONZE,G4_STAINLESS_STEEL,G4_CR39,G4_OCTADECANOL]
FEATURE [App::DocumentObjectGroupPython] C_element128  label="C_element : 073"  # scripted group (container) (typed FeaturePython)
  n = 14
  ref = C_element
FEATURE [App::DocumentObjectGroupPython] H_element118  label="H_element : 065"  # scripted group (container) (typed FeaturePython)
  n = 10
  ref = H_element
FEATURE [App::DocumentObjectGroupPython] O_element111  label="O_element : 064"  # scripted group (container) (typed FeaturePython)
  n = 2
  ref = O_element
FEATURE [App::DocumentObjectGroupPython] N_element050  label="N_element : 023"  # scripted group (container) (typed FeaturePython)
  n = 2
  ref = N_element
FEATURE [App::DocumentObjectGroupPython] G4_KEVLAR  # scripted group (container) (typed FeaturePython)
  Dunit = g/cm3
  Dvalue = 1.44
  Group = -> [C_element128,H_element118,O_element111,N_element050]
  conduct = 2
  density = 1
  expand = 3
  formula = G4_KEVLAR
  name = G4_KEVLAR
  specific = 4
FEATURE [App::DocumentObjectGroupPython] C_element129  label="C_element : 074"  # scripted group (container) (typed FeaturePython)
  n = 10
  ref = C_element
FEATURE [App::DocumentObjectGroupPython] H_element119  label="H_element : 066"  # scripted group (container) (typed FeaturePython)
  n = 8
  ref = H_element
FEATURE [App::DocumentObjectGroupPython] O_element112  label="O_element : 065"  # scripted group (container) (typed FeaturePython)
  n = 4
  ref = O_element
FEATURE [App::DocumentObjectGroupPython] G4_DACRON  # scripted group (container) (typed FeaturePython)
  Dunit = g/cm3
  Dvalue = 1.4
  Group = -> [C_element129,H_element119,O_element112]
  conduct = 2
  density = 1
  expand = 3
  formula = G4_DACRON
  name = G4_DACRON
  specific = 4
FEATURE [App::DocumentObjectGroupPython] C_element130  label="C_element : 075"  # scripted group (container) (typed FeaturePython)
  n = 4
  ref = C_element
FEATURE [App::DocumentObjectGroupPython] H_element120  label="H_element : 067"  # scripted group (container) (typed FeaturePython)
  n = 5
  ref = H_element
FEATURE [App::DocumentObjectGroupPython] Cl_element030  label="Cl_element : 016"  # scripted group (container) (typed FeaturePython)
  n = 1
  ref = Cl_element
FEATURE [App::DocumentObjectGroupPython] G4_NEOPRENE  # scripted group (container) (typed FeaturePython)
  Dunit = g/cm3
  Dvalue = 1.23
  Group = -> [C_element130,H_element120,Cl_element030]
  conduct = 2
  density = 1
  expand = 3
  formula = G4_NEOPRENE
  name = G4_NEOPRENE
  specific = 4
FEATURE [App::DocumentObjectGroupPython] Space  # scripted group (container) (typed FeaturePython)
  Group = -> [G4_KEVLAR,G4_DACRON,G4_NEOPRENE]
FEATURE [App::DocumentObjectGroupPython] H_element121  label="H_element : 068"  # scripted group (container) (typed FeaturePython)
  n = 5
  ref = H_element
FEATURE [App::DocumentObjectGroupPython] C_element131  label="C_element : 076"  # scripted group (container) (typed FeaturePython)
  n = 4
  ref = C_element
FEATURE [App::DocumentObjectGroupPython] N_element051  label="N_element : 3"  # scripted group (container) (typed FeaturePython)
  n = 3
  ref = N_element
FEATURE [App::DocumentObjectGroupPython] O_element113  label="O_element : 066"  # scripted group (container) (typed FeaturePython)
  n = 1
  ref = O_element
FEATURE [App::DocumentObjectGroupPython] G4_CYTOSINE  # scripted group (container) (typed FeaturePython)
  Dunit = g/cm3
  Dvalue = 1.55
  Group = -> [H_element121,C_element131,N_element051,O_element113]
  conduct = 2
  density = 1
  expand = 3
  formula = G4_CYTOSINE
  name = G4_CYTOSINE
  specific = 4
FEATURE [App::DocumentObjectGroupPython] H_element122  label="H_element : 069"  # scripted group (container) (typed FeaturePython)
  n = 6
  ref = H_element
FEATURE [App::DocumentObjectGroupPython] C_element132  label="C_element : 077"  # scripted group (container) (typed FeaturePython)
  n = 5
  ref = C_element
FEATURE [App::DocumentObjectGroupPython] N_element052  label="N_element : 024"  # scripted group (container) (typed FeaturePython)
  n = 2
  ref = N_element
FEATURE [App::DocumentObjectGroupPython] O_element114  label="O_element : 067"  # scripted group (container) (typed FeaturePython)
  n = 2
  ref = O_element
FEATURE [App::DocumentObjectGroupPython] G4_THYMINE  # scripted group (container) (typed FeaturePython)
  Dunit = g/cm3
  Dvalue = 1.23
  Group = -> [H_element122,C_element132,N_element052,O_element114]
  conduct = 2
  density = 1
  expand = 3
  formula = G4_THYMINE
  name = G4_THYMINE
  specific = 4
FEATURE [App::DocumentObjectGroupPython] H_element123  label="H_element : 070"  # scripted group (container) (typed FeaturePython)
  n = 4
  ref = H_element
FEATURE [App::DocumentObjectGroupPython] C_element133  label="C_element : 078"  # scripted group (container) (typed FeaturePython)
  n = 4
  ref = C_element
FEATURE [App::DocumentObjectGroupPython] N_element053  label="N_element : 025"  # scripted group (container) (typed FeaturePython)
  n = 2
  ref = N_element
FEATURE [App::DocumentObjectGroupPython] O_element115  label="O_element : 068"  # scripted group (container) (typed FeaturePython)
  n = 2
  ref = O_element
FEATURE [App::DocumentObjectGroupPython] G4_URACIL  # scripted group (container) (typed FeaturePython)
  Dunit = g/cm3
  Dvalue = 1.32
  Group = -> [H_element123,C_element133,N_element053,O_element115]
  conduct = 2
  density = 1
  expand = 3
  formula = G4_URACIL
  name = G4_URACIL
  specific = 4
FEATURE [App::DocumentObjectGroupPython] H_element124  label="H_element : 071"  # scripted group (container) (typed FeaturePython)
  n = 4
  ref = H_element
FEATURE [App::DocumentObjectGroupPython] C_element134  label="C_element : 079"  # scripted group (container) (typed FeaturePython)
  n = 5
  ref = C_element
FEATURE [App::DocumentObjectGroupPython] N_element054  label="N_element : 026"  # scripted group (container) (typed FeaturePython)
  n = 5
  ref = N_element
FEATURE [App::DocumentObjectGroupPython] G4_DNA_ADENINE  # scripted group (container) (typed FeaturePython)
  Dunit = g/cm3
  Dvalue = 1
  Group = -> [H_element124,C_element134,N_element054]
  conduct = 2
  density = 1
  expand = 3
  formula = G4_DNA_ADENINE
  name = G4_DNA_ADENINE
  specific = 4
FEATURE [App::DocumentObjectGroupPython] H_element125  label="H_element : 072"  # scripted group (container) (typed FeaturePython)
  n = 4
  ref = H_element
FEATURE [App::DocumentObjectGroupPython] C_element135  label="C_element : 080"  # scripted group (container) (typed FeaturePython)
  n = 5
  ref = C_element
FEATURE [App::DocumentObjectGroupPython] N_element055  label="N_element : 027"  # scripted group (container) (typed FeaturePython)
  n = 5
  ref = N_element
FEATURE [App::DocumentObjectGroupPython] O_element116  label="O_element : 069"  # scripted group (container) (typed FeaturePython)
  n = 1
  ref = O_element
FEATURE [App::DocumentObjectGroupPython] G4_DNA_GUANINE  # scripted group (container) (typed FeaturePython)
  Dunit = g/cm3
  Dvalue = 1
  Group = -> [H_element125,C_element135,N_element055,O_element116]
  conduct = 2
  density = 1
  expand = 3
  formula = G4_DNA_GUANINE
  name = G4_DNA_GUANINE
  specific = 4
FEATURE [App::DocumentObjectGroupPython] H_element126  label="H_element : 073"  # scripted group (container) (typed FeaturePython)
  n = 4
  ref = H_element
FEATURE [App::DocumentObjectGroupPython] C_element136  label="C_element : 081"  # scripted group (container) (typed FeaturePython)
  n = 4
  ref = C_element
FEATURE [App::DocumentObjectGroupPython] N_element056  label="N_element : 028"  # scripted group (container) (typed FeaturePython)
  n = 3
  ref = N_element
FEATURE [App::DocumentObjectGroupPython] O_element117  label="O_element : 070"  # scripted group (container) (typed FeaturePython)
  n = 1
  ref = O_element
FEATURE [App::DocumentObjectGroupPython] G4_DNA_CYTOSINE  # scripted group (container) (typed FeaturePython)
  Dunit = g/cm3
  Dvalue = 1
  Group = -> [H_element126,C_element136,N_element056,O_element117]
  conduct = 2
  density = 1
  expand = 3
  formula = G4_DNA_CYTOSINE
  name = G4_DNA_CYTOSINE
  specific = 4
FEATURE [App::DocumentObjectGroupPython] H_element127  label="H_element : 074"  # scripted group (container) (typed FeaturePython)
  n = 5
  ref = H_element
FEATURE [App::DocumentObjectGroupPython] C_element137  label="C_element : 082"  # scripted group (container) (typed FeaturePython)
  n = 5
  ref = C_element
FEATURE [App::DocumentObjectGroupPython] N_element057  label="N_element : 029"  # scripted group (container) (typed FeaturePython)
  n = 2
  ref = N_element
FEATURE [App::DocumentObjectGroupPython] O_element118  label="O_element : 071"  # scripted group (container) (typed FeaturePython)
  n = 2
  ref = O_element
FEATURE [App::DocumentObjectGroupPython] G4_DNA_THYMINE  # scripted group (container) (typed FeaturePython)
  Dunit = g/cm3
  Dvalue = 1
  Group = -> [H_element127,C_element137,N_element057,O_element118]
  conduct = 2
  density = 1
  expand = 3
  formula = G4_DNA_THYMINE
  name = G4_DNA_THYMINE
  specific = 4
FEATURE [App::DocumentObjectGroupPython] H_element128  label="H_element : 075"  # scripted group (container) (typed FeaturePython)
  n = 3
  ref = H_element
FEATURE [App::DocumentObjectGroupPython] C_element138  label="C_element : 083"  # scripted group (container) (typed FeaturePython)
  n = 4
  ref = C_element
FEATURE [App::DocumentObjectGroupPython] N_element058  label="N_element : 030"  # scripted group (container) (typed FeaturePython)
  n = 2
  ref = N_element
FEATURE [App::DocumentObjectGroupPython] O_element119  label="O_element : 072"  # scripted group (container) (typed FeaturePython)
  n = 2
  ref = O_element
FEATURE [App::DocumentObjectGroupPython] G4_DNA_URACIL  # scripted group (container) (typed FeaturePython)
  Dunit = g/cm3
  Dvalue = 1
  Group = -> [H_element128,C_element138,N_element058,O_element119]
  conduct = 2
  density = 1
  expand = 3
  formula = G4_DNA_URACIL
  name = G4_DNA_URACIL
  specific = 4
FEATURE [App::DocumentObjectGroupPython] H_element129  label="H_element : 076"  # scripted group (container) (typed FeaturePython)
  n = 10
  ref = H_element
FEATURE [App::DocumentObjectGroupPython] C_element139  label="C_element : 084"  # scripted group (container) (typed FeaturePython)
  n = 10
  ref = C_element
FEATURE [App::DocumentObjectGroupPython] N_element059  label="N_element : 031"  # scripted group (container) (typed FeaturePython)
  n = 5
  ref = N_element
FEATURE [App::DocumentObjectGroupPython] O_element120  label="O_element : 073"  # scripted group (container) (typed FeaturePython)
  n = 4
  ref = O_element
FEATURE [App::DocumentObjectGroupPython] G4_DNA_ADENOSINE  # scripted group (container) (typed FeaturePython)
  Dunit = g/cm3
  Dvalue = 1
  Group = -> [H_element129,C_element139,N_element059,O_element120]
  conduct = 2
  density = 1
  expand = 3
  formula = G4_DNA_ADENOSINE
  name = G4_DNA_ADENOSINE
  specific = 4
FEATURE [App::DocumentObjectGroupPython] H_element130  label="H_element : 077"  # scripted group (container) (typed FeaturePython)
  n = 10
  ref = H_element
FEATURE [App::DocumentObjectGroupPython] C_element140  label="C_element : 085"  # scripted group (container) (typed FeaturePython)
  n = 10
  ref = C_element
FEATURE [App::DocumentObjectGroupPython] N_element060  label="N_element : 032"  # scripted group (container) (typed FeaturePython)
  n = 5
  ref = N_element
FEATURE [App::DocumentObjectGroupPython] O_element121  label="O_element : 074"  # scripted group (container) (typed FeaturePython)
  n = 5
  ref = O_element
FEATURE [App::DocumentObjectGroupPython] G4_DNA_GUANOSINE  # scripted group (container) (typed FeaturePython)
  Dunit = g/cm3
  Dvalue = 1
  Group = -> [H_element130,C_element140,N_element060,O_element121]
  conduct = 2
  density = 1
  expand = 3
  formula = G4_DNA_GUANOSINE
  name = G4_DNA_GUANOSINE
  specific = 4
FEATURE [App::DocumentObjectGroupPython] H_element131  label="H_element : 078"  # scripted group (container) (typed FeaturePython)
  n = 10
  ref = H_element
FEATURE [App::DocumentObjectGroupPython] C_element141  label="C_element : 086"  # scripted group (container) (typed FeaturePython)
  n = 9
  ref = C_element
FEATURE [App::DocumentObjectGroupPython] N_element061  label="N_element : 033"  # scripted group (container) (typed FeaturePython)
  n = 3
  ref = N_element
FEATURE [App::DocumentObjectGroupPython] O_element122  label="O_element : 075"  # scripted group (container) (typed FeaturePython)
  n = 5
  ref = O_element
FEATURE [App::DocumentObjectGroupPython] G4_DNA_CYTIDINE  # scripted group (container) (typed FeaturePython)
  Dunit = g/cm3
  Dvalue = 1
  Group = -> [H_element131,C_element141,N_element061,O_element122]
  conduct = 2
  density = 1
  expand = 3
  formula = G4_DNA_CYTIDINE
  name = G4_DNA_CYTIDINE
  specific = 4
FEATURE [App::DocumentObjectGroupPython] H_element132  label="H_element : 079"  # scripted group (container) (typed FeaturePython)
  n = 9
  ref = H_element
FEATURE [App::DocumentObjectGroupPython] C_element142  label="C_element : 087"  # scripted group (container) (typed FeaturePython)
  n = 9
  ref = C_element
FEATURE [App::DocumentObjectGroupPython] N_element062  label="N_element : 034"  # scripted group (container) (typed FeaturePython)
  n = 2
  ref = N_element
FEATURE [App::DocumentObjectGroupPython] O_element123  label="O_element : 076"  # scripted group (container) (typed FeaturePython)
  n = 6
  ref = O_element
FEATURE [App::DocumentObjectGroupPython] G4_DNA_URIDINE  # scripted group (container) (typed FeaturePython)
  Dunit = g/cm3
  Dvalue = 1
  Group = -> [H_element132,C_element142,N_element062,O_element123]
  conduct = 2
  density = 1
  expand = 3
  formula = G4_DNA_URIDINE
  name = G4_DNA_URIDINE
  specific = 4
FEATURE [App::DocumentObjectGroupPython] H_element133  label="H_element : 080"  # scripted group (container) (typed FeaturePython)
  n = 11
  ref = H_element
FEATURE [App::DocumentObjectGroupPython] C_element143  label="C_element : 088"  # scripted group (container) (typed FeaturePython)
  n = 10
  ref = C_element
FEATURE [App::DocumentObjectGroupPython] N_element063  label="N_element : 035"  # scripted group (container) (typed FeaturePython)
  n = 2
  ref = N_element
FEATURE [App::DocumentObjectGroupPython] O_element124  label="O_element : 077"  # scripted group (container) (typed FeaturePython)
  n = 6
  ref = O_element
FEATURE [App::DocumentObjectGroupPython] G4_DNA_METHYLURIDINE  # scripted group (container) (typed FeaturePython)
  Dunit = g/cm3
  Dvalue = 1
  Group = -> [H_element133,C_element143,N_element063,O_element124]
  conduct = 2
  density = 1
  expand = 3
  formula = G4_DNA_METHYLURIDINE
  name = G4_DNA_METHYLURIDINE
  specific = 4
FEATURE [App::DocumentObjectGroupPython] P_element014  label="P_element : 003"  # scripted group (container) (typed FeaturePython)
  n = 1
  ref = P_element
FEATURE [App::DocumentObjectGroupPython] O_element125  label="O_element : 078"  # scripted group (container) (typed FeaturePython)
  n = 3
  ref = O_element
FEATURE [App::DocumentObjectGroupPython] G4_DNA_MONOPHOSPHATE  # scripted group (container) (typed FeaturePython)
  Dunit = g/cm3
  Dvalue = 1
  Group = -> [P_element014,O_element125]
  conduct = 2
  density = 1
  expand = 3
  formula = G4_DNA_MONOPHOSPHATE
  name = G4_DNA_MONOPHOSPHATE
  specific = 4
FEATURE [App::DocumentObjectGroupPython] H_element134  label="H_element : 081"  # scripted group (container) (typed FeaturePython)
  n = 10
  ref = H_element
FEATURE [App::DocumentObjectGroupPython] C_element144  label="C_element : 089"  # scripted group (container) (typed FeaturePython)
  n = 10
  ref = C_element
FEATURE [App::DocumentObjectGroupPython] N_element064  label="N_element : 036"  # scripted group (container) (typed FeaturePython)
  n = 5
  ref = N_element
FEATURE [App::DocumentObjectGroupPython] O_element126  label="O_element : 079"  # scripted group (container) (typed FeaturePython)
  n = 7
  ref = O_element
FEATURE [App::DocumentObjectGroupPython] P_element015  label="P_element : 004"  # scripted group (container) (typed FeaturePython)
  n = 1
  ref = P_element
FEATURE [App::DocumentObjectGroupPython] G4_DNA_A  # scripted group (container) (typed FeaturePython)
  Dunit = g/cm3
  Dvalue = 1
  Group = -> [H_element134,C_element144,N_element064,O_element126,P_element015]
  conduct = 2
  density = 1
  expand = 3
  formula = G4_DNA_A
  name = G4_DNA_A
  specific = 4
FEATURE [App::DocumentObjectGroupPython] H_element135  label="H_element : 082"  # scripted group (container) (typed FeaturePython)
  n = 10
  ref = H_element
FEATURE [App::DocumentObjectGroupPython] C_element145  label="C_element : 090"  # scripted group (container) (typed FeaturePython)
  n = 10
  ref = C_element
FEATURE [App::DocumentObjectGroupPython] N_element065  label="N_element : 037"  # scripted group (container) (typed FeaturePython)
  n = 5
  ref = N_element
FEATURE [App::DocumentObjectGroupPython] O_element127  label="O_element : 8"  # scripted group (container) (typed FeaturePython)
  n = 8
  ref = O_element
FEATURE [App::DocumentObjectGroupPython] P_element016  label="P_element : 005"  # scripted group (container) (typed FeaturePython)
  n = 1
  ref = P_element
FEATURE [App::DocumentObjectGroupPython] G4_DNA_G  # scripted group (container) (typed FeaturePython)
  Dunit = g/cm3
  Dvalue = 1
  Group = -> [H_element135,C_element145,N_element065,O_element127,P_element016]
  conduct = 2
  density = 1
  expand = 3
  formula = G4_DNA_G
  name = G4_DNA_G
  specific = 4
FEATURE [App::DocumentObjectGroupPython] H_element136  label="H_element : 083"  # scripted group (container) (typed FeaturePython)
  n = 10
  ref = H_element
FEATURE [App::DocumentObjectGroupPython] C_element146  label="C_element : 091"  # scripted group (container) (typed FeaturePython)
  n = 9
  ref = C_element
FEATURE [App::DocumentObjectGroupPython] N_element066  label="N_element : 038"  # scripted group (container) (typed FeaturePython)
  n = 3
  ref = N_element
FEATURE [App::DocumentObjectGroupPython] O_element128  label="O_element : 080"  # scripted group (container) (typed FeaturePython)
  n = 8
  ref = O_element
FEATURE [App::DocumentObjectGroupPython] P_element017  label="P_element : 006"  # scripted group (container) (typed FeaturePython)
  n = 1
  ref = P_element
FEATURE [App::DocumentObjectGroupPython] G4_DNA_C  # scripted group (container) (typed FeaturePython)
  Dunit = g/cm3
  Dvalue = 1
  Group = -> [H_element136,C_element146,N_element066,O_element128,P_element017]
  conduct = 2
  density = 1
  expand = 3
  formula = G4_DNA_C
  name = G4_DNA_C
  specific = 4
FEATURE [App::DocumentObjectGroupPython] H_element137  label="H_element : 084"  # scripted group (container) (typed FeaturePython)
  n = 9
  ref = H_element
FEATURE [App::DocumentObjectGroupPython] C_element147  label="C_element : 092"  # scripted group (container) (typed FeaturePython)
  n = 9
  ref = C_element
FEATURE [App::DocumentObjectGroupPython] N_element067  label="N_element : 039"  # scripted group (container) (typed FeaturePython)
  n = 2
  ref = N_element
FEATURE [App::DocumentObjectGroupPython] O_element129  label="O_element : 9"  # scripted group (container) (typed FeaturePython)
  n = 9
  ref = O_element
FEATURE [App::DocumentObjectGroupPython] P_element018  label="P_element : 007"  # scripted group (container) (typed FeaturePython)
  n = 1
  ref = P_element
FEATURE [App::DocumentObjectGroupPython] G4_DNA_U  # scripted group (container) (typed FeaturePython)
  Dunit = g/cm3
  Dvalue = 1
  Group = -> [H_element137,C_element147,N_element067,O_element129,P_element018]
  conduct = 2
  density = 1
  expand = 3
  formula = G4_DNA_U
  name = G4_DNA_U
  specific = 4
FEATURE [App::DocumentObjectGroupPython] H_element138  label="H_element : 085"  # scripted group (container) (typed FeaturePython)
  n = 11
  ref = H_element
FEATURE [App::DocumentObjectGroupPython] C_element148  label="C_element : 093"  # scripted group (container) (typed FeaturePython)
  n = 10
  ref = C_element
FEATURE [App::DocumentObjectGroupPython] N_element068  label="N_element : 040"  # scripted group (container) (typed FeaturePython)
  n = 2
  ref = N_element
FEATURE [App::DocumentObjectGroupPython] O_element130  label="O_element : 081"  # scripted group (container) (typed FeaturePython)
  n = 9
  ref = O_element
FEATURE [App::DocumentObjectGroupPython] P_element019  label="P_element : 008"  # scripted group (container) (typed FeaturePython)
  n = 1
  ref = P_element
FEATURE [App::DocumentObjectGroupPython] G4_DNA_MU  # scripted group (container) (typed FeaturePython)
  Dunit = g/cm3
  Dvalue = 1
  Group = -> [H_element138,C_element148,N_element068,O_element130,P_element019]
  conduct = 2
  density = 1
  expand = 3
  formula = G4_DNA_MU
  name = G4_DNA_MU
  specific = 4
FEATURE [App::DocumentObjectGroupPython] BioChemical  # scripted group (container) (typed FeaturePython)
  Group = -> [G4_CYTOSINE,G4_THYMINE,G4_URACIL,G4_DNA_ADENINE,G4_DNA_GUANINE,G4_DNA_CYTOSINE,G4_DNA_THYMINE,G4_DNA_URACIL,G4_DNA_ADENOSINE,G4_DNA_GUANOSINE,G4_DNA_CYTIDINE,G4_DNA_URIDINE,G4_DNA_METHYLURIDINE,G4_DNA_MONOPHOSPHATE,G4_DNA_A,G4_DNA_G,G4_DNA_C,G4_DNA_U,G4_DNA_MU]
FEATURE [App::DocumentObjectGroupPython] G4Materials  # scripted group (container) (typed FeaturePython)
  Group = -> [NIST,Element,HEP,Space,BioChemical]
  version = 1
FEATURE [App::DocumentObjectGroupPython] Geant4  # scripted group (container) (typed FeaturePython)
  Group = -> [G4Isotopes,G4Elements,G4Materials]
FEATURE [App::DocumentObjectGroupPython] Materials  # scripted group (container) (typed FeaturePython)
  Group = -> [LYSO,Air,Glass,Geant4]
FEATURE [Part::FeaturePython] GDMLBox_World  # WARN: FeaturePython — macro-defined, semantics opaque (R4)
  lunit = 2
  material = 1
  x = 50
  y = 50
  z = 50
FEATURE [Part::FeaturePython] GDMLBox_Obj001  # WARN: FeaturePython — macro-defined, semantics opaque (R4)
  lunit = 2
  material = 0
  x = 2
  y = 2
  z = 15
FEATURE [Part::FeaturePython] GDMLBox_GlassPlate001  # WARN: FeaturePython — macro-defined, semantics opaque (R4)
  lunit = 2
  material = 2
  x = 2
  y = 2
  z = 2
FEATURE [App::Part] Det001
  Group = -> [GDMLBox_GlassPlate001]
  Origin = -> Origin005
  Placement = pos=(0,0,8.5) rot=(0,0,1;0rad)
FEATURE [App::FeaturePython] ScintWrap001  # WARN: FeaturePython — macro-defined, semantics opaque (R4)
  PV1 = Obj001
  PV2 = Det001
  Surface = ScintWrap
FEATURE [App::Part] Obj001
  Group = -> [GDMLBox_Obj001,Det001,ScintWrap001]
  Origin = -> Origin004
FEATURE [App::Link] GDMLBox_Obj001001
  LinkedObject = -> GDMLBox_Obj001
FEATURE [App::Link] GDMLBox_GlassPlate001001
  LinkedObject = -> GDMLBox_GlassPlate001
FEATURE [App::Part] Det001001
  Group = -> [GDMLBox_GlassPlate001001]
  Origin = -> Origin007
  Placement = pos=(0,0,8.5) rot=(0,0,1;0rad)
FEATURE [App::FeaturePython] ScintWrap002  # WARN: FeaturePython — macro-defined, semantics opaque (R4)
  PV1 = Obj001001
  PV2 = Det001001
  Surface = ScintWrap
FEATURE [App::Part] Obj001001
  CopyNumber = 1
  Group = -> [GDMLBox_Obj001001,Det001001,ScintWrap002]
  Origin = -> Origin006
  Placement = pos=(0,3,0) rot=(0,0,1;0rad)
FEATURE [App::Link] GDMLBox_Obj001002
  LinkedObject = -> GDMLBox_Obj001
FEATURE [App::Link] GDMLBox_GlassPlate001002
  LinkedObject = -> GDMLBox_GlassPlate001
FEATURE [App::Part] Det001002
  Group = -> [GDMLBox_GlassPlate001002]
  Origin = -> Origin009
  Placement = pos=(0,0,8.5) rot=(0,0,1;0rad)
FEATURE [App::FeaturePython] ScintWrap003  # WARN: FeaturePython — macro-defined, semantics opaque (R4)
  PV1 = Obj001002
  PV2 = Det001002
  Surface = ScintWrap
FEATURE [App::Part] Obj001002
  CopyNumber = 2
  Group = -> [GDMLBox_Obj001002,Det001002,ScintWrap003]
  Origin = -> Origin008
  Placement = pos=(3,0,0) rot=(0,0,1;0rad)
FEATURE [App::Link] GDMLBox_Obj001003
  LinkedObject = -> GDMLBox_Obj001
FEATURE [App::Link] GDMLBox_GlassPlate001003
  LinkedObject = -> GDMLBox_GlassPlate001
FEATURE [App::Part] Det001003
  Group = -> [GDMLBox_GlassPlate001003]
  Origin = -> Origin011
  Placement = pos=(0,0,8.5) rot=(0,0,1;0rad)
FEATURE [App::FeaturePython] ScintWrap004  # WARN: FeaturePython — macro-defined, semantics opaque (R4)
  PV1 = Obj001003
  PV2 = Det001003
  Surface = ScintWrap
FEATURE [App::Part] Obj001003
  CopyNumber = 3
  Group = -> [GDMLBox_Obj001003,Det001003,ScintWrap004]
  Origin = -> Origin010
  Placement = pos=(3,3,0) rot=(0,0,1;0rad)
FEATURE [App::Part] Array001
  Group = -> [Obj001,Obj001001,Obj001002,Obj001003]
  Origin = -> Origin003
FEATURE [App::Part] World
  Group = -> [GDMLBox_World,Array001]
  Origin = -> Origin
